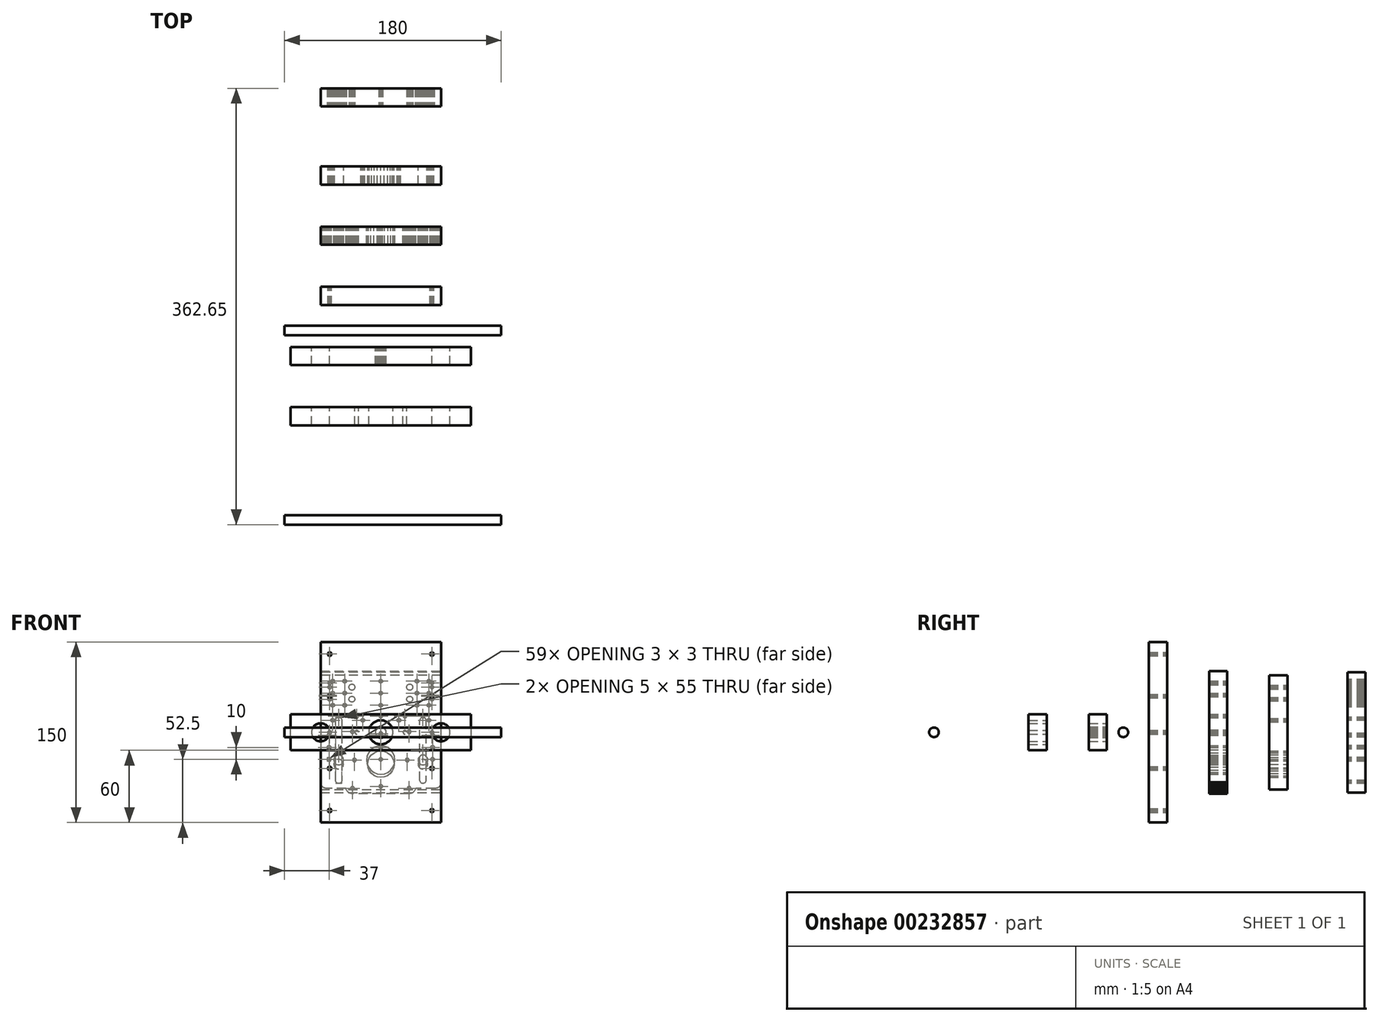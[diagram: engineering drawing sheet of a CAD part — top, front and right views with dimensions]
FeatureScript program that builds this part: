
annotation { "Feature Type Name" : "Feature", "Feature Type Description" : "" }
export const myFeature = defineFeature(function(context is Context, id is Id, definition is map)
    precondition{}
    {
        {
            var Q0;
            Q0=qCreatedBy(makeId("Front.planeOp"),FACE);
            var sketch = newSketch(context, id + "F0", { "sketchPlane" : qUnion([Q0])});
            skLineSegment(sketch, "E0", {"start": v(23.55, -51) * mm, "end": v(-23.55, -51) * mm});
            skLineSegment(sketch, "E1", {"start": v(-23.55, -51) * mm, "end": v(-24.18, -50.96) * mm});
            skLineSegment(sketch, "E2", {"start": v(-24.18, -50.96) * mm, "end": v(-24.8, -50.86) * mm});
            skLineSegment(sketch, "E3", {"start": v(-24.8, -50.86) * mm, "end": v(-25.42, -50.68) * mm});
            skLineSegment(sketch, "E4", {"start": v(-25.42, -50.68) * mm, "end": v(-26, -50.43) * mm});
            skLineSegment(sketch, "E5", {"start": v(-26, -50.43) * mm, "end": v(-26.55, -50.12) * mm});
            skLineSegment(sketch, "E6", {"start": v(-26.55, -50.12) * mm, "end": v(-27.07, -49.75) * mm});
            skLineSegment(sketch, "E7", {"start": v(-27.07, -49.75) * mm, "end": v(-27.54, -49.32) * mm});
            skLineSegment(sketch, "E8", {"start": v(-27.54, -49.32) * mm, "end": v(-27.95, -48.84) * mm});
            skLineSegment(sketch, "E9", {"start": v(-27.95, -48.84) * mm, "end": v(-28.31, -48.32) * mm});
            skLineSegment(sketch, "E10", {"start": v(-28.31, -48.32) * mm, "end": v(-28.6, -47.75) * mm});
            skLineSegment(sketch, "E11", {"start": v(-28.6, -47.75) * mm, "end": v(-28.84, -47.16) * mm});
            skLineSegment(sketch, "E12", {"start": v(-28.84, -47.16) * mm, "end": v(-29, -46.55) * mm});
            skLineSegment(sketch, "E13", {"start": v(-29, -46.55) * mm, "end": v(-45, -46.55) * mm});
            skLineSegment(sketch, "E14", {"start": v(-45, -46.55) * mm, "end": v(-45.65, -46.5) * mm});
            skLineSegment(sketch, "E15", {"start": v(-45.65, -46.5) * mm, "end": v(-46.3, -46.38) * mm});
            skLineSegment(sketch, "E16", {"start": v(-46.3, -46.38) * mm, "end": v(-46.91, -46.17) * mm});
            skLineSegment(sketch, "E17", {"start": v(-46.91, -46.17) * mm, "end": v(-47.5, -45.88) * mm});
            skLineSegment(sketch, "E18", {"start": v(-47.5, -45.88) * mm, "end": v(-48.04, -45.52) * mm});
            skLineSegment(sketch, "E19", {"start": v(-48.04, -45.52) * mm, "end": v(-48.54, -45.09) * mm});
            skLineSegment(sketch, "E20", {"start": v(-48.54, -45.09) * mm, "end": v(-48.97, -44.6) * mm});
            skLineSegment(sketch, "E21", {"start": v(-48.97, -44.6) * mm, "end": v(-49.33, -44.05) * mm});
            skLineSegment(sketch, "E22", {"start": v(-49.33, -44.05) * mm, "end": v(-49.62, -43.46) * mm});
            skLineSegment(sketch, "E23", {"start": v(-49.62, -43.46) * mm, "end": v(-49.83, -42.84) * mm});
            skLineSegment(sketch, "E24", {"start": v(-49.83, -42.84) * mm, "end": v(-49.96, -42.2) * mm});
            skLineSegment(sketch, "E25", {"start": v(-49.96, -42.2) * mm, "end": v(-50, -41.55) * mm});
            skLineSegment(sketch, "E26", {"start": v(-50, -41.55) * mm, "end": v(-50, 51) * mm});
            skLineSegment(sketch, "E27", {"start": v(-50, 51) * mm, "end": v(50, 51) * mm});
            skLineSegment(sketch, "E28", {"start": v(50, 51) * mm, "end": v(50, -41.55) * mm});
            skLineSegment(sketch, "E29", {"start": v(50, -41.55) * mm, "end": v(49.96, -42.2) * mm});
            skLineSegment(sketch, "E30", {"start": v(49.96, -42.2) * mm, "end": v(49.83, -42.84) * mm});
            skLineSegment(sketch, "E31", {"start": v(49.83, -42.84) * mm, "end": v(49.62, -43.46) * mm});
            skLineSegment(sketch, "E32", {"start": v(49.62, -43.46) * mm, "end": v(49.33, -44.05) * mm});
            skLineSegment(sketch, "E33", {"start": v(49.33, -44.05) * mm, "end": v(48.97, -44.6) * mm});
            skLineSegment(sketch, "E34", {"start": v(48.97, -44.6) * mm, "end": v(48.54, -45.09) * mm});
            skLineSegment(sketch, "E35", {"start": v(48.54, -45.09) * mm, "end": v(48.04, -45.52) * mm});
            skLineSegment(sketch, "E36", {"start": v(48.04, -45.52) * mm, "end": v(47.5, -45.88) * mm});
            skLineSegment(sketch, "E37", {"start": v(47.5, -45.88) * mm, "end": v(46.91, -46.17) * mm});
            skLineSegment(sketch, "E38", {"start": v(46.91, -46.17) * mm, "end": v(46.3, -46.38) * mm});
            skLineSegment(sketch, "E39", {"start": v(46.3, -46.38) * mm, "end": v(45.65, -46.5) * mm});
            skLineSegment(sketch, "E40", {"start": v(45.65, -46.5) * mm, "end": v(45, -46.55) * mm});
            skLineSegment(sketch, "E41", {"start": v(45, -46.55) * mm, "end": v(29, -46.55) * mm});
            skLineSegment(sketch, "E42", {"start": v(29, -46.55) * mm, "end": v(28.84, -47.16) * mm});
            skLineSegment(sketch, "E43", {"start": v(28.84, -47.16) * mm, "end": v(28.6, -47.75) * mm});
            skLineSegment(sketch, "E44", {"start": v(28.6, -47.75) * mm, "end": v(28.31, -48.32) * mm});
            skLineSegment(sketch, "E45", {"start": v(28.31, -48.32) * mm, "end": v(27.95, -48.84) * mm});
            skLineSegment(sketch, "E46", {"start": v(27.95, -48.84) * mm, "end": v(27.54, -49.32) * mm});
            skLineSegment(sketch, "E47", {"start": v(27.54, -49.32) * mm, "end": v(27.07, -49.75) * mm});
            skLineSegment(sketch, "E48", {"start": v(27.07, -49.75) * mm, "end": v(26.55, -50.12) * mm});
            skLineSegment(sketch, "E49", {"start": v(26.55, -50.12) * mm, "end": v(26, -50.43) * mm});
            skLineSegment(sketch, "E50", {"start": v(26, -50.43) * mm, "end": v(25.42, -50.68) * mm});
            skLineSegment(sketch, "E51", {"start": v(25.42, -50.68) * mm, "end": v(24.8, -50.86) * mm});
            skLineSegment(sketch, "E52", {"start": v(24.8, -50.86) * mm, "end": v(24.18, -50.96) * mm});
            skLineSegment(sketch, "E53", {"start": v(24.18, -50.96) * mm, "end": v(23.55, -51) * mm});
            skLineSegment(sketch, "E54", {"start": v(3.05, -34.4) * mm, "end": v(5.9, -33.22) * mm});
            skLineSegment(sketch, "E55", {"start": v(5.9, -33.22) * mm, "end": v(8.34, -31.34) * mm});
            skLineSegment(sketch, "E56", {"start": v(8.34, -31.34) * mm, "end": v(10.22, -28.9) * mm});
            skLineSegment(sketch, "E57", {"start": v(10.22, -28.9) * mm, "end": v(11.4, -26.05) * mm});
            skLineSegment(sketch, "E58", {"start": v(11.4, -26.05) * mm, "end": v(11.8, -23) * mm});
            skLineSegment(sketch, "E59", {"start": v(11.8, -23) * mm, "end": v(11.4, -19.95) * mm});
            skLineSegment(sketch, "E60", {"start": v(11.4, -19.95) * mm, "end": v(10.22, -17.1) * mm});
            skLineSegment(sketch, "E61", {"start": v(10.22, -17.1) * mm, "end": v(8.34, -14.66) * mm});
            skLineSegment(sketch, "E62", {"start": v(8.34, -14.66) * mm, "end": v(5.9, -12.78) * mm});
            skLineSegment(sketch, "E63", {"start": v(5.9, -12.78) * mm, "end": v(3.05, -11.6) * mm});
            skLineSegment(sketch, "E64", {"start": v(3.05, -11.6) * mm, "end": v(0, -11.2) * mm});
            skLineSegment(sketch, "E65", {"start": v(0, -11.2) * mm, "end": v(-3.05, -11.6) * mm});
            skLineSegment(sketch, "E66", {"start": v(-3.05, -11.6) * mm, "end": v(-5.9, -12.78) * mm});
            skLineSegment(sketch, "E67", {"start": v(-5.9, -12.78) * mm, "end": v(-8.34, -14.66) * mm});
            skLineSegment(sketch, "E68", {"start": v(-8.34, -14.66) * mm, "end": v(-10.22, -17.1) * mm});
            skLineSegment(sketch, "E69", {"start": v(-10.22, -17.1) * mm, "end": v(-11.4, -19.95) * mm});
            skLineSegment(sketch, "E70", {"start": v(-11.4, -19.95) * mm, "end": v(-11.8, -23) * mm});
            skLineSegment(sketch, "E71", {"start": v(-11.8, -23) * mm, "end": v(-11.4, -26.05) * mm});
            skLineSegment(sketch, "E72", {"start": v(-11.4, -26.05) * mm, "end": v(-10.22, -28.9) * mm});
            skLineSegment(sketch, "E73", {"start": v(-10.22, -28.9) * mm, "end": v(-8.34, -31.34) * mm});
            skLineSegment(sketch, "E74", {"start": v(-8.34, -31.34) * mm, "end": v(-5.9, -33.22) * mm});
            skLineSegment(sketch, "E75", {"start": v(-5.9, -33.22) * mm, "end": v(-3.05, -34.4) * mm});
            skLineSegment(sketch, "E76", {"start": v(-3.05, -34.4) * mm, "end": v(0, -34.8) * mm});
            skLineSegment(sketch, "E77", {"start": v(0, -34.8) * mm, "end": v(3.05, -34.4) * mm});
            skLineSegment(sketch, "E78", {"start": v(-22.25, -47.3) * mm, "end": v(-22.1, -46.94) * mm});
            skLineSegment(sketch, "E79", {"start": v(-22.1, -46.94) * mm, "end": v(-22.05, -46.55) * mm});
            skLineSegment(sketch, "E80", {"start": v(-22.05, -46.55) * mm, "end": v(-22.1, -46.16) * mm});
            skLineSegment(sketch, "E81", {"start": v(-22.1, -46.16) * mm, "end": v(-22.25, -45.8) * mm});
            skLineSegment(sketch, "E82", {"start": v(-22.25, -45.8) * mm, "end": v(-22.49, -45.49) * mm});
            skLineSegment(sketch, "E83", {"start": v(-22.49, -45.49) * mm, "end": v(-22.8, -45.25) * mm});
            skLineSegment(sketch, "E84", {"start": v(-22.8, -45.25) * mm, "end": v(-23.16, -45.1) * mm});
            skLineSegment(sketch, "E85", {"start": v(-23.16, -45.1) * mm, "end": v(-23.55, -45.05) * mm});
            skLineSegment(sketch, "E86", {"start": v(-23.55, -45.05) * mm, "end": v(-23.94, -45.1) * mm});
            skLineSegment(sketch, "E87", {"start": v(-23.94, -45.1) * mm, "end": v(-24.3, -45.25) * mm});
            skLineSegment(sketch, "E88", {"start": v(-24.3, -45.25) * mm, "end": v(-24.61, -45.49) * mm});
            skLineSegment(sketch, "E89", {"start": v(-24.61, -45.49) * mm, "end": v(-24.85, -45.8) * mm});
            skLineSegment(sketch, "E90", {"start": v(-24.85, -45.8) * mm, "end": v(-25, -46.16) * mm});
            skLineSegment(sketch, "E91", {"start": v(-25, -46.16) * mm, "end": v(-25.05, -46.55) * mm});
            skLineSegment(sketch, "E92", {"start": v(-25.05, -46.55) * mm, "end": v(-25, -46.94) * mm});
            skLineSegment(sketch, "E93", {"start": v(-25, -46.94) * mm, "end": v(-24.85, -47.3) * mm});
            skLineSegment(sketch, "E94", {"start": v(-24.85, -47.3) * mm, "end": v(-24.61, -47.61) * mm});
            skLineSegment(sketch, "E95", {"start": v(-24.61, -47.61) * mm, "end": v(-24.3, -47.85) * mm});
            skLineSegment(sketch, "E96", {"start": v(-24.3, -47.85) * mm, "end": v(-23.94, -48) * mm});
            skLineSegment(sketch, "E97", {"start": v(-23.94, -48) * mm, "end": v(-23.55, -48.05) * mm});
            skLineSegment(sketch, "E98", {"start": v(-23.55, -48.05) * mm, "end": v(-23.16, -48) * mm});
            skLineSegment(sketch, "E99", {"start": v(-23.16, -48) * mm, "end": v(-22.8, -47.85) * mm});
            skLineSegment(sketch, "E100", {"start": v(-22.8, -47.85) * mm, "end": v(-22.49, -47.61) * mm});
            skLineSegment(sketch, "E101", {"start": v(-22.49, -47.61) * mm, "end": v(-22.25, -47.3) * mm});
            skLineSegment(sketch, "E102", {"start": v(22.8, -45.25) * mm, "end": v(22.49, -45.49) * mm});
            skLineSegment(sketch, "E103", {"start": v(22.49, -45.49) * mm, "end": v(22.25, -45.8) * mm});
            skLineSegment(sketch, "E104", {"start": v(22.25, -45.8) * mm, "end": v(22.1, -46.16) * mm});
            skLineSegment(sketch, "E105", {"start": v(22.1, -46.16) * mm, "end": v(22.05, -46.55) * mm});
            skLineSegment(sketch, "E106", {"start": v(22.05, -46.55) * mm, "end": v(22.1, -46.94) * mm});
            skLineSegment(sketch, "E107", {"start": v(22.1, -46.94) * mm, "end": v(22.25, -47.3) * mm});
            skLineSegment(sketch, "E108", {"start": v(22.25, -47.3) * mm, "end": v(22.49, -47.61) * mm});
            skLineSegment(sketch, "E109", {"start": v(22.49, -47.61) * mm, "end": v(22.8, -47.85) * mm});
            skLineSegment(sketch, "E110", {"start": v(22.8, -47.85) * mm, "end": v(23.16, -48) * mm});
            skLineSegment(sketch, "E111", {"start": v(23.16, -48) * mm, "end": v(23.55, -48.05) * mm});
            skLineSegment(sketch, "E112", {"start": v(23.55, -48.05) * mm, "end": v(23.94, -48) * mm});
            skLineSegment(sketch, "E113", {"start": v(23.94, -48) * mm, "end": v(24.3, -47.85) * mm});
            skLineSegment(sketch, "E114", {"start": v(24.3, -47.85) * mm, "end": v(24.61, -47.61) * mm});
            skLineSegment(sketch, "E115", {"start": v(24.61, -47.61) * mm, "end": v(24.85, -47.3) * mm});
            skLineSegment(sketch, "E116", {"start": v(24.85, -47.3) * mm, "end": v(25, -46.94) * mm});
            skLineSegment(sketch, "E117", {"start": v(25, -46.94) * mm, "end": v(25.05, -46.55) * mm});
            skLineSegment(sketch, "E118", {"start": v(25.05, -46.55) * mm, "end": v(25, -46.16) * mm});
            skLineSegment(sketch, "E119", {"start": v(25, -46.16) * mm, "end": v(24.85, -45.8) * mm});
            skLineSegment(sketch, "E120", {"start": v(24.85, -45.8) * mm, "end": v(24.61, -45.49) * mm});
            skLineSegment(sketch, "E121", {"start": v(24.61, -45.49) * mm, "end": v(24.3, -45.25) * mm});
            skLineSegment(sketch, "E122", {"start": v(24.3, -45.25) * mm, "end": v(23.94, -45.1) * mm});
            skLineSegment(sketch, "E123", {"start": v(23.94, -45.1) * mm, "end": v(23.55, -45.05) * mm});
            skLineSegment(sketch, "E124", {"start": v(23.55, -45.05) * mm, "end": v(23.16, -45.1) * mm});
            skLineSegment(sketch, "E125", {"start": v(23.16, -45.1) * mm, "end": v(22.8, -45.25) * mm});
            skLineSegment(sketch, "E126", {"start": v(24.85, -0.2) * mm, "end": v(25, 0.16) * mm});
            skLineSegment(sketch, "E127", {"start": v(25, 0.16) * mm, "end": v(25.05, 0.55) * mm});
            skLineSegment(sketch, "E128", {"start": v(25.05, 0.55) * mm, "end": v(25, 0.94) * mm});
            skLineSegment(sketch, "E129", {"start": v(25, 0.94) * mm, "end": v(24.85, 1.3) * mm});
            skLineSegment(sketch, "E130", {"start": v(24.85, 1.3) * mm, "end": v(24.61, 1.61) * mm});
            skLineSegment(sketch, "E131", {"start": v(24.61, 1.61) * mm, "end": v(24.3, 1.85) * mm});
            skLineSegment(sketch, "E132", {"start": v(24.3, 1.85) * mm, "end": v(23.94, 2) * mm});
            skLineSegment(sketch, "E133", {"start": v(23.94, 2) * mm, "end": v(23.55, 2.05) * mm});
            skLineSegment(sketch, "E134", {"start": v(23.55, 2.05) * mm, "end": v(23.16, 2) * mm});
            skLineSegment(sketch, "E135", {"start": v(23.16, 2) * mm, "end": v(22.8, 1.85) * mm});
            skLineSegment(sketch, "E136", {"start": v(22.8, 1.85) * mm, "end": v(22.49, 1.61) * mm});
            skLineSegment(sketch, "E137", {"start": v(22.49, 1.61) * mm, "end": v(22.25, 1.3) * mm});
            skLineSegment(sketch, "E138", {"start": v(22.25, 1.3) * mm, "end": v(22.1, 0.94) * mm});
            skLineSegment(sketch, "E139", {"start": v(22.1, 0.94) * mm, "end": v(22.05, 0.55) * mm});
            skLineSegment(sketch, "E140", {"start": v(22.05, 0.55) * mm, "end": v(22.1, 0.16) * mm});
            skLineSegment(sketch, "E141", {"start": v(22.1, 0.16) * mm, "end": v(22.25, -0.2) * mm});
            skLineSegment(sketch, "E142", {"start": v(22.25, -0.2) * mm, "end": v(22.49, -0.51) * mm});
            skLineSegment(sketch, "E143", {"start": v(22.49, -0.51) * mm, "end": v(22.8, -0.75) * mm});
            skLineSegment(sketch, "E144", {"start": v(22.8, -0.75) * mm, "end": v(23.16, -0.9) * mm});
            skLineSegment(sketch, "E145", {"start": v(23.16, -0.9) * mm, "end": v(23.55, -0.95) * mm});
            skLineSegment(sketch, "E146", {"start": v(23.55, -0.95) * mm, "end": v(23.94, -0.9) * mm});
            skLineSegment(sketch, "E147", {"start": v(23.94, -0.9) * mm, "end": v(24.3, -0.75) * mm});
            skLineSegment(sketch, "E148", {"start": v(24.3, -0.75) * mm, "end": v(24.61, -0.51) * mm});
            skLineSegment(sketch, "E149", {"start": v(24.61, -0.51) * mm, "end": v(24.85, -0.2) * mm});
            skLineSegment(sketch, "E150", {"start": v(-25, 0.16) * mm, "end": v(-24.85, -0.2) * mm});
            skLineSegment(sketch, "E151", {"start": v(-24.85, -0.2) * mm, "end": v(-24.61, -0.51) * mm});
            skLineSegment(sketch, "E152", {"start": v(-24.61, -0.51) * mm, "end": v(-24.3, -0.75) * mm});
            skLineSegment(sketch, "E153", {"start": v(-24.3, -0.75) * mm, "end": v(-23.94, -0.9) * mm});
            skLineSegment(sketch, "E154", {"start": v(-23.94, -0.9) * mm, "end": v(-23.55, -0.95) * mm});
            skLineSegment(sketch, "E155", {"start": v(-23.55, -0.95) * mm, "end": v(-23.16, -0.9) * mm});
            skLineSegment(sketch, "E156", {"start": v(-23.16, -0.9) * mm, "end": v(-22.8, -0.75) * mm});
            skLineSegment(sketch, "E157", {"start": v(-22.8, -0.75) * mm, "end": v(-22.49, -0.51) * mm});
            skLineSegment(sketch, "E158", {"start": v(-22.49, -0.51) * mm, "end": v(-22.25, -0.2) * mm});
            skLineSegment(sketch, "E159", {"start": v(-22.25, -0.2) * mm, "end": v(-22.1, 0.16) * mm});
            skLineSegment(sketch, "E160", {"start": v(-22.1, 0.16) * mm, "end": v(-22.05, 0.55) * mm});
            skLineSegment(sketch, "E161", {"start": v(-22.05, 0.55) * mm, "end": v(-22.1, 0.94) * mm});
            skLineSegment(sketch, "E162", {"start": v(-22.1, 0.94) * mm, "end": v(-22.25, 1.3) * mm});
            skLineSegment(sketch, "E163", {"start": v(-22.25, 1.3) * mm, "end": v(-22.49, 1.61) * mm});
            skLineSegment(sketch, "E164", {"start": v(-22.49, 1.61) * mm, "end": v(-22.8, 1.85) * mm});
            skLineSegment(sketch, "E165", {"start": v(-22.8, 1.85) * mm, "end": v(-23.16, 2) * mm});
            skLineSegment(sketch, "E166", {"start": v(-23.16, 2) * mm, "end": v(-23.55, 2.05) * mm});
            skLineSegment(sketch, "E167", {"start": v(-23.55, 2.05) * mm, "end": v(-23.94, 2) * mm});
            skLineSegment(sketch, "E168", {"start": v(-23.94, 2) * mm, "end": v(-24.3, 1.85) * mm});
            skLineSegment(sketch, "E169", {"start": v(-24.3, 1.85) * mm, "end": v(-24.61, 1.61) * mm});
            skLineSegment(sketch, "E170", {"start": v(-24.61, 1.61) * mm, "end": v(-24.85, 1.3) * mm});
            skLineSegment(sketch, "E171", {"start": v(-24.85, 1.3) * mm, "end": v(-25, 0.94) * mm});
            skLineSegment(sketch, "E172", {"start": v(-25, 0.94) * mm, "end": v(-25.05, 0.55) * mm});
            skLineSegment(sketch, "E173", {"start": v(-25.05, 0.55) * mm, "end": v(-25, 0.16) * mm});
            skLineSegment(sketch, "E174", {"start": v(-1.45, -44.53) * mm, "end": v(-1.5, -44.92) * mm});
            skLineSegment(sketch, "E175", {"start": v(-1.5, -44.92) * mm, "end": v(-1.45, -45.3) * mm});
            skLineSegment(sketch, "E176", {"start": v(-1.45, -45.3) * mm, "end": v(-1.3, -45.67) * mm});
            skLineSegment(sketch, "E177", {"start": v(-1.3, -45.67) * mm, "end": v(-1.06, -45.98) * mm});
            skLineSegment(sketch, "E178", {"start": v(-1.06, -45.98) * mm, "end": v(-0.75, -46.22) * mm});
            skLineSegment(sketch, "E179", {"start": v(-0.75, -46.22) * mm, "end": v(-0.39, -46.37) * mm});
            skLineSegment(sketch, "E180", {"start": v(-0.39, -46.37) * mm, "end": v(0, -46.42) * mm});
            skLineSegment(sketch, "E181", {"start": v(0, -46.42) * mm, "end": v(0.39, -46.37) * mm});
            skLineSegment(sketch, "E182", {"start": v(0.39, -46.37) * mm, "end": v(0.75, -46.22) * mm});
            skLineSegment(sketch, "E183", {"start": v(0.75, -46.22) * mm, "end": v(1.06, -45.98) * mm});
            skLineSegment(sketch, "E184", {"start": v(1.06, -45.98) * mm, "end": v(1.3, -45.67) * mm});
            skLineSegment(sketch, "E185", {"start": v(1.3, -45.67) * mm, "end": v(1.45, -45.3) * mm});
            skLineSegment(sketch, "E186", {"start": v(1.45, -45.3) * mm, "end": v(1.5, -44.92) * mm});
            skLineSegment(sketch, "E187", {"start": v(1.5, -44.92) * mm, "end": v(1.45, -44.53) * mm});
            skLineSegment(sketch, "E188", {"start": v(1.45, -44.53) * mm, "end": v(1.3, -44.17) * mm});
            skLineSegment(sketch, "E189", {"start": v(1.3, -44.17) * mm, "end": v(1.06, -43.86) * mm});
            skLineSegment(sketch, "E190", {"start": v(1.06, -43.86) * mm, "end": v(0.75, -43.62) * mm});
            skLineSegment(sketch, "E191", {"start": v(0.75, -43.62) * mm, "end": v(0.39, -43.47) * mm});
            skLineSegment(sketch, "E192", {"start": v(0.39, -43.47) * mm, "end": v(0, -43.42) * mm});
            skLineSegment(sketch, "E193", {"start": v(0, -43.42) * mm, "end": v(-0.39, -43.47) * mm});
            skLineSegment(sketch, "E194", {"start": v(-0.39, -43.47) * mm, "end": v(-0.75, -43.62) * mm});
            skLineSegment(sketch, "E195", {"start": v(-0.75, -43.62) * mm, "end": v(-1.06, -43.86) * mm});
            skLineSegment(sketch, "E196", {"start": v(-1.06, -43.86) * mm, "end": v(-1.3, -44.17) * mm});
            skLineSegment(sketch, "E197", {"start": v(-1.3, -44.17) * mm, "end": v(-1.45, -44.53) * mm});
            skLineSegment(sketch, "E198", {"start": v(-21.53, -24.45) * mm, "end": v(-21.17, -24.3) * mm});
            skLineSegment(sketch, "E199", {"start": v(-21.17, -24.3) * mm, "end": v(-20.86, -24.06) * mm});
            skLineSegment(sketch, "E200", {"start": v(-20.86, -24.06) * mm, "end": v(-20.62, -23.75) * mm});
            skLineSegment(sketch, "E201", {"start": v(-20.62, -23.75) * mm, "end": v(-20.47, -23.39) * mm});
            skLineSegment(sketch, "E202", {"start": v(-20.47, -23.39) * mm, "end": v(-20.42, -23) * mm});
            skLineSegment(sketch, "E203", {"start": v(-20.42, -23) * mm, "end": v(-20.47, -22.61) * mm});
            skLineSegment(sketch, "E204", {"start": v(-20.47, -22.61) * mm, "end": v(-20.62, -22.25) * mm});
            skLineSegment(sketch, "E205", {"start": v(-20.62, -22.25) * mm, "end": v(-20.86, -21.94) * mm});
            skLineSegment(sketch, "E206", {"start": v(-20.86, -21.94) * mm, "end": v(-21.17, -21.7) * mm});
            skLineSegment(sketch, "E207", {"start": v(-21.17, -21.7) * mm, "end": v(-21.53, -21.55) * mm});
            skLineSegment(sketch, "E208", {"start": v(-21.53, -21.55) * mm, "end": v(-21.92, -21.5) * mm});
            skLineSegment(sketch, "E209", {"start": v(-21.92, -21.5) * mm, "end": v(-22.3, -21.55) * mm});
            skLineSegment(sketch, "E210", {"start": v(-22.3, -21.55) * mm, "end": v(-22.67, -21.7) * mm});
            skLineSegment(sketch, "E211", {"start": v(-22.67, -21.7) * mm, "end": v(-22.98, -21.94) * mm});
            skLineSegment(sketch, "E212", {"start": v(-22.98, -21.94) * mm, "end": v(-23.22, -22.25) * mm});
            skLineSegment(sketch, "E213", {"start": v(-23.22, -22.25) * mm, "end": v(-23.37, -22.61) * mm});
            skLineSegment(sketch, "E214", {"start": v(-23.37, -22.61) * mm, "end": v(-23.42, -23) * mm});
            skLineSegment(sketch, "E215", {"start": v(-23.42, -23) * mm, "end": v(-23.37, -23.39) * mm});
            skLineSegment(sketch, "E216", {"start": v(-23.37, -23.39) * mm, "end": v(-23.22, -23.75) * mm});
            skLineSegment(sketch, "E217", {"start": v(-23.22, -23.75) * mm, "end": v(-22.98, -24.06) * mm});
            skLineSegment(sketch, "E218", {"start": v(-22.98, -24.06) * mm, "end": v(-22.67, -24.3) * mm});
            skLineSegment(sketch, "E219", {"start": v(-22.67, -24.3) * mm, "end": v(-22.3, -24.45) * mm});
            skLineSegment(sketch, "E220", {"start": v(-22.3, -24.45) * mm, "end": v(-21.92, -24.5) * mm});
            skLineSegment(sketch, "E221", {"start": v(-21.92, -24.5) * mm, "end": v(-21.53, -24.45) * mm});
            skLineSegment(sketch, "E222", {"start": v(-1.3, -0.33) * mm, "end": v(-1.45, -0.7) * mm});
            skLineSegment(sketch, "E223", {"start": v(-1.45, -0.7) * mm, "end": v(-1.5, -1.08) * mm});
            skLineSegment(sketch, "E224", {"start": v(-1.5, -1.08) * mm, "end": v(-1.45, -1.47) * mm});
            skLineSegment(sketch, "E225", {"start": v(-1.45, -1.47) * mm, "end": v(-1.3, -1.83) * mm});
            skLineSegment(sketch, "E226", {"start": v(-1.3, -1.83) * mm, "end": v(-1.06, -2.14) * mm});
            skLineSegment(sketch, "E227", {"start": v(-1.06, -2.14) * mm, "end": v(-0.75, -2.38) * mm});
            skLineSegment(sketch, "E228", {"start": v(-0.75, -2.38) * mm, "end": v(-0.39, -2.53) * mm});
            skLineSegment(sketch, "E229", {"start": v(-0.39, -2.53) * mm, "end": v(0, -2.58) * mm});
            skLineSegment(sketch, "E230", {"start": v(0, -2.58) * mm, "end": v(0.39, -2.53) * mm});
            skLineSegment(sketch, "E231", {"start": v(0.39, -2.53) * mm, "end": v(0.75, -2.38) * mm});
            skLineSegment(sketch, "E232", {"start": v(0.75, -2.38) * mm, "end": v(1.06, -2.14) * mm});
            skLineSegment(sketch, "E233", {"start": v(1.06, -2.14) * mm, "end": v(1.3, -1.83) * mm});
            skLineSegment(sketch, "E234", {"start": v(1.3, -1.83) * mm, "end": v(1.45, -1.47) * mm});
            skLineSegment(sketch, "E235", {"start": v(1.45, -1.47) * mm, "end": v(1.5, -1.08) * mm});
            skLineSegment(sketch, "E236", {"start": v(1.5, -1.08) * mm, "end": v(1.45, -0.7) * mm});
            skLineSegment(sketch, "E237", {"start": v(1.45, -0.7) * mm, "end": v(1.3, -0.33) * mm});
            skLineSegment(sketch, "E238", {"start": v(1.3, -0.33) * mm, "end": v(1.06, -0.02) * mm});
            skLineSegment(sketch, "E239", {"start": v(1.06, -0.02) * mm, "end": v(0.75, 0.22) * mm});
            skLineSegment(sketch, "E240", {"start": v(0.75, 0.22) * mm, "end": v(0.39, 0.37) * mm});
            skLineSegment(sketch, "E241", {"start": v(0.39, 0.37) * mm, "end": v(0, 0.42) * mm});
            skLineSegment(sketch, "E242", {"start": v(0, 0.42) * mm, "end": v(-0.39, 0.37) * mm});
            skLineSegment(sketch, "E243", {"start": v(-0.39, 0.37) * mm, "end": v(-0.75, 0.22) * mm});
            skLineSegment(sketch, "E244", {"start": v(-0.75, 0.22) * mm, "end": v(-1.06, -0.02) * mm});
            skLineSegment(sketch, "E245", {"start": v(-1.06, -0.02) * mm, "end": v(-1.3, -0.33) * mm});
            skLineSegment(sketch, "E246", {"start": v(21.17, -21.7) * mm, "end": v(20.86, -21.94) * mm});
            skLineSegment(sketch, "E247", {"start": v(20.86, -21.94) * mm, "end": v(20.62, -22.25) * mm});
            skLineSegment(sketch, "E248", {"start": v(20.62, -22.25) * mm, "end": v(20.47, -22.61) * mm});
            skLineSegment(sketch, "E249", {"start": v(20.47, -22.61) * mm, "end": v(20.42, -23) * mm});
            skLineSegment(sketch, "E250", {"start": v(20.42, -23) * mm, "end": v(20.47, -23.39) * mm});
            skLineSegment(sketch, "E251", {"start": v(20.47, -23.39) * mm, "end": v(20.62, -23.75) * mm});
            skLineSegment(sketch, "E252", {"start": v(20.62, -23.75) * mm, "end": v(20.86, -24.06) * mm});
            skLineSegment(sketch, "E253", {"start": v(20.86, -24.06) * mm, "end": v(21.17, -24.3) * mm});
            skLineSegment(sketch, "E254", {"start": v(21.17, -24.3) * mm, "end": v(21.53, -24.45) * mm});
            skLineSegment(sketch, "E255", {"start": v(21.53, -24.45) * mm, "end": v(21.92, -24.5) * mm});
            skLineSegment(sketch, "E256", {"start": v(21.92, -24.5) * mm, "end": v(22.3, -24.45) * mm});
            skLineSegment(sketch, "E257", {"start": v(22.3, -24.45) * mm, "end": v(22.67, -24.3) * mm});
            skLineSegment(sketch, "E258", {"start": v(22.67, -24.3) * mm, "end": v(22.98, -24.06) * mm});
            skLineSegment(sketch, "E259", {"start": v(22.98, -24.06) * mm, "end": v(23.22, -23.75) * mm});
            skLineSegment(sketch, "E260", {"start": v(23.22, -23.75) * mm, "end": v(23.37, -23.39) * mm});
            skLineSegment(sketch, "E261", {"start": v(23.37, -23.39) * mm, "end": v(23.42, -23) * mm});
            skLineSegment(sketch, "E262", {"start": v(23.42, -23) * mm, "end": v(23.37, -22.61) * mm});
            skLineSegment(sketch, "E263", {"start": v(23.37, -22.61) * mm, "end": v(23.22, -22.25) * mm});
            skLineSegment(sketch, "E264", {"start": v(23.22, -22.25) * mm, "end": v(22.98, -21.94) * mm});
            skLineSegment(sketch, "E265", {"start": v(22.98, -21.94) * mm, "end": v(22.67, -21.7) * mm});
            skLineSegment(sketch, "E266", {"start": v(22.67, -21.7) * mm, "end": v(22.3, -21.55) * mm});
            skLineSegment(sketch, "E267", {"start": v(22.3, -21.55) * mm, "end": v(21.92, -21.5) * mm});
            skLineSegment(sketch, "E268", {"start": v(21.92, -21.5) * mm, "end": v(21.53, -21.55) * mm});
            skLineSegment(sketch, "E269", {"start": v(21.53, -21.55) * mm, "end": v(21.17, -21.7) * mm});
            skLineSegment(sketch, "E270", {"start": v(35.75, 12.2) * mm, "end": v(36.06, 12.44) * mm});
            skLineSegment(sketch, "E271", {"start": v(36.06, 12.44) * mm, "end": v(36.3, 12.75) * mm});
            skLineSegment(sketch, "E272", {"start": v(36.3, 12.75) * mm, "end": v(36.45, 13.11) * mm});
            skLineSegment(sketch, "E273", {"start": v(36.45, 13.11) * mm, "end": v(36.5, 13.5) * mm});
            skLineSegment(sketch, "E274", {"start": v(36.5, 13.5) * mm, "end": v(36.45, 13.89) * mm});
            skLineSegment(sketch, "E275", {"start": v(36.45, 13.89) * mm, "end": v(36.3, 14.25) * mm});
            skLineSegment(sketch, "E276", {"start": v(36.3, 14.25) * mm, "end": v(36.06, 14.56) * mm});
            skLineSegment(sketch, "E277", {"start": v(36.06, 14.56) * mm, "end": v(35.75, 14.8) * mm});
            skLineSegment(sketch, "E278", {"start": v(35.75, 14.8) * mm, "end": v(35.39, 14.95) * mm});
            skLineSegment(sketch, "E279", {"start": v(35.39, 14.95) * mm, "end": v(35, 15) * mm});
            skLineSegment(sketch, "E280", {"start": v(35, 15) * mm, "end": v(34.61, 14.95) * mm});
            skLineSegment(sketch, "E281", {"start": v(34.61, 14.95) * mm, "end": v(34.25, 14.8) * mm});
            skLineSegment(sketch, "E282", {"start": v(34.25, 14.8) * mm, "end": v(33.94, 14.56) * mm});
            skLineSegment(sketch, "E283", {"start": v(33.94, 14.56) * mm, "end": v(33.7, 14.25) * mm});
            skLineSegment(sketch, "E284", {"start": v(33.7, 14.25) * mm, "end": v(33.55, 13.89) * mm});
            skLineSegment(sketch, "E285", {"start": v(33.55, 13.89) * mm, "end": v(33.5, 13.5) * mm});
            skLineSegment(sketch, "E286", {"start": v(33.5, 13.5) * mm, "end": v(33.55, 13.11) * mm});
            skLineSegment(sketch, "E287", {"start": v(33.55, 13.11) * mm, "end": v(33.7, 12.75) * mm});
            skLineSegment(sketch, "E288", {"start": v(33.7, 12.75) * mm, "end": v(33.94, 12.44) * mm});
            skLineSegment(sketch, "E289", {"start": v(33.94, 12.44) * mm, "end": v(34.25, 12.2) * mm});
            skLineSegment(sketch, "E290", {"start": v(34.25, 12.2) * mm, "end": v(34.61, 12.05) * mm});
            skLineSegment(sketch, "E291", {"start": v(34.61, 12.05) * mm, "end": v(35, 12) * mm});
            skLineSegment(sketch, "E292", {"start": v(35, 12) * mm, "end": v(35.39, 12.05) * mm});
            skLineSegment(sketch, "E293", {"start": v(35.39, 12.05) * mm, "end": v(35.75, 12.2) * mm});
            skLineSegment(sketch, "E294", {"start": v(18.7, 14.25) * mm, "end": v(18.55, 13.89) * mm});
            skLineSegment(sketch, "E295", {"start": v(18.55, 13.89) * mm, "end": v(18.5, 13.5) * mm});
            skLineSegment(sketch, "E296", {"start": v(18.5, 13.5) * mm, "end": v(18.55, 13.11) * mm});
            skLineSegment(sketch, "E297", {"start": v(18.55, 13.11) * mm, "end": v(18.7, 12.75) * mm});
            skLineSegment(sketch, "E298", {"start": v(18.7, 12.75) * mm, "end": v(18.94, 12.44) * mm});
            skLineSegment(sketch, "E299", {"start": v(18.94, 12.44) * mm, "end": v(19.25, 12.2) * mm});
            skLineSegment(sketch, "E300", {"start": v(19.25, 12.2) * mm, "end": v(19.61, 12.05) * mm});
            skLineSegment(sketch, "E301", {"start": v(19.61, 12.05) * mm, "end": v(20, 12) * mm});
            skLineSegment(sketch, "E302", {"start": v(20, 12) * mm, "end": v(20.39, 12.05) * mm});
            skLineSegment(sketch, "E303", {"start": v(20.39, 12.05) * mm, "end": v(20.75, 12.2) * mm});
            skLineSegment(sketch, "E304", {"start": v(20.75, 12.2) * mm, "end": v(21.06, 12.44) * mm});
            skLineSegment(sketch, "E305", {"start": v(21.06, 12.44) * mm, "end": v(21.3, 12.75) * mm});
            skLineSegment(sketch, "E306", {"start": v(21.3, 12.75) * mm, "end": v(21.45, 13.11) * mm});
            skLineSegment(sketch, "E307", {"start": v(21.45, 13.11) * mm, "end": v(21.5, 13.5) * mm});
            skLineSegment(sketch, "E308", {"start": v(21.5, 13.5) * mm, "end": v(21.45, 13.89) * mm});
            skLineSegment(sketch, "E309", {"start": v(21.45, 13.89) * mm, "end": v(21.3, 14.25) * mm});
            skLineSegment(sketch, "E310", {"start": v(21.3, 14.25) * mm, "end": v(21.06, 14.56) * mm});
            skLineSegment(sketch, "E311", {"start": v(21.06, 14.56) * mm, "end": v(20.75, 14.8) * mm});
            skLineSegment(sketch, "E312", {"start": v(20.75, 14.8) * mm, "end": v(20.39, 14.95) * mm});
            skLineSegment(sketch, "E313", {"start": v(20.39, 14.95) * mm, "end": v(20, 15) * mm});
            skLineSegment(sketch, "E314", {"start": v(20, 15) * mm, "end": v(19.61, 14.95) * mm});
            skLineSegment(sketch, "E315", {"start": v(19.61, 14.95) * mm, "end": v(19.25, 14.8) * mm});
            skLineSegment(sketch, "E316", {"start": v(19.25, 14.8) * mm, "end": v(18.94, 14.56) * mm});
            skLineSegment(sketch, "E317", {"start": v(18.94, 14.56) * mm, "end": v(18.7, 14.25) * mm});
            skLineSegment(sketch, "E318", {"start": v(1.5, 13.5) * mm, "end": v(1.45, 13.89) * mm});
            skLineSegment(sketch, "E319", {"start": v(1.45, 13.89) * mm, "end": v(1.3, 14.25) * mm});
            skLineSegment(sketch, "E320", {"start": v(1.3, 14.25) * mm, "end": v(1.06, 14.56) * mm});
            skLineSegment(sketch, "E321", {"start": v(1.06, 14.56) * mm, "end": v(0.75, 14.8) * mm});
            skLineSegment(sketch, "E322", {"start": v(0.75, 14.8) * mm, "end": v(0.39, 14.95) * mm});
            skLineSegment(sketch, "E323", {"start": v(0.39, 14.95) * mm, "end": v(0, 15) * mm});
            skLineSegment(sketch, "E324", {"start": v(0, 15) * mm, "end": v(-0.39, 14.95) * mm});
            skLineSegment(sketch, "E325", {"start": v(-0.39, 14.95) * mm, "end": v(-0.75, 14.8) * mm});
            skLineSegment(sketch, "E326", {"start": v(-0.75, 14.8) * mm, "end": v(-1.06, 14.56) * mm});
            skLineSegment(sketch, "E327", {"start": v(-1.06, 14.56) * mm, "end": v(-1.3, 14.25) * mm});
            skLineSegment(sketch, "E328", {"start": v(-1.3, 14.25) * mm, "end": v(-1.45, 13.89) * mm});
            skLineSegment(sketch, "E329", {"start": v(-1.45, 13.89) * mm, "end": v(-1.5, 13.5) * mm});
            skLineSegment(sketch, "E330", {"start": v(-1.5, 13.5) * mm, "end": v(-1.45, 13.11) * mm});
            skLineSegment(sketch, "E331", {"start": v(-1.45, 13.11) * mm, "end": v(-1.3, 12.75) * mm});
            skLineSegment(sketch, "E332", {"start": v(-1.3, 12.75) * mm, "end": v(-1.06, 12.44) * mm});
            skLineSegment(sketch, "E333", {"start": v(-1.06, 12.44) * mm, "end": v(-0.75, 12.2) * mm});
            skLineSegment(sketch, "E334", {"start": v(-0.75, 12.2) * mm, "end": v(-0.39, 12.05) * mm});
            skLineSegment(sketch, "E335", {"start": v(-0.39, 12.05) * mm, "end": v(0, 12) * mm});
            skLineSegment(sketch, "E336", {"start": v(0, 12) * mm, "end": v(0.39, 12.05) * mm});
            skLineSegment(sketch, "E337", {"start": v(0.39, 12.05) * mm, "end": v(0.75, 12.2) * mm});
            skLineSegment(sketch, "E338", {"start": v(0.75, 12.2) * mm, "end": v(1.06, 12.44) * mm});
            skLineSegment(sketch, "E339", {"start": v(1.06, 12.44) * mm, "end": v(1.3, 12.75) * mm});
            skLineSegment(sketch, "E340", {"start": v(1.3, 12.75) * mm, "end": v(1.45, 13.11) * mm});
            skLineSegment(sketch, "E341", {"start": v(1.45, 13.11) * mm, "end": v(1.5, 13.5) * mm});
            skLineSegment(sketch, "E342", {"start": v(-19.25, 14.8) * mm, "end": v(-19.61, 14.95) * mm});
            skLineSegment(sketch, "E343", {"start": v(-19.61, 14.95) * mm, "end": v(-20, 15) * mm});
            skLineSegment(sketch, "E344", {"start": v(-20, 15) * mm, "end": v(-20.39, 14.95) * mm});
            skLineSegment(sketch, "E345", {"start": v(-20.39, 14.95) * mm, "end": v(-20.75, 14.8) * mm});
            skLineSegment(sketch, "E346", {"start": v(-20.75, 14.8) * mm, "end": v(-21.06, 14.56) * mm});
            skLineSegment(sketch, "E347", {"start": v(-21.06, 14.56) * mm, "end": v(-21.3, 14.25) * mm});
            skLineSegment(sketch, "E348", {"start": v(-21.3, 14.25) * mm, "end": v(-21.45, 13.89) * mm});
            skLineSegment(sketch, "E349", {"start": v(-21.45, 13.89) * mm, "end": v(-21.5, 13.5) * mm});
            skLineSegment(sketch, "E350", {"start": v(-21.5, 13.5) * mm, "end": v(-21.45, 13.11) * mm});
            skLineSegment(sketch, "E351", {"start": v(-21.45, 13.11) * mm, "end": v(-21.3, 12.75) * mm});
            skLineSegment(sketch, "E352", {"start": v(-21.3, 12.75) * mm, "end": v(-21.06, 12.44) * mm});
            skLineSegment(sketch, "E353", {"start": v(-21.06, 12.44) * mm, "end": v(-20.75, 12.2) * mm});
            skLineSegment(sketch, "E354", {"start": v(-20.75, 12.2) * mm, "end": v(-20.39, 12.05) * mm});
            skLineSegment(sketch, "E355", {"start": v(-20.39, 12.05) * mm, "end": v(-20, 12) * mm});
            skLineSegment(sketch, "E356", {"start": v(-20, 12) * mm, "end": v(-19.61, 12.05) * mm});
            skLineSegment(sketch, "E357", {"start": v(-19.61, 12.05) * mm, "end": v(-19.25, 12.2) * mm});
            skLineSegment(sketch, "E358", {"start": v(-19.25, 12.2) * mm, "end": v(-18.94, 12.44) * mm});
            skLineSegment(sketch, "E359", {"start": v(-18.94, 12.44) * mm, "end": v(-18.7, 12.75) * mm});
            skLineSegment(sketch, "E360", {"start": v(-18.7, 12.75) * mm, "end": v(-18.55, 13.11) * mm});
            skLineSegment(sketch, "E361", {"start": v(-18.55, 13.11) * mm, "end": v(-18.5, 13.5) * mm});
            skLineSegment(sketch, "E362", {"start": v(-18.5, 13.5) * mm, "end": v(-18.55, 13.89) * mm});
            skLineSegment(sketch, "E363", {"start": v(-18.55, 13.89) * mm, "end": v(-18.7, 14.25) * mm});
            skLineSegment(sketch, "E364", {"start": v(-18.7, 14.25) * mm, "end": v(-18.94, 14.56) * mm});
            skLineSegment(sketch, "E365", {"start": v(-18.94, 14.56) * mm, "end": v(-19.25, 14.8) * mm});
            skLineSegment(sketch, "E366", {"start": v(-35.39, 14.95) * mm, "end": v(-35.75, 14.8) * mm});
            skLineSegment(sketch, "E367", {"start": v(-35.75, 14.8) * mm, "end": v(-36.06, 14.56) * mm});
            skLineSegment(sketch, "E368", {"start": v(-36.06, 14.56) * mm, "end": v(-36.3, 14.25) * mm});
            skLineSegment(sketch, "E369", {"start": v(-36.3, 14.25) * mm, "end": v(-36.45, 13.89) * mm});
            skLineSegment(sketch, "E370", {"start": v(-36.45, 13.89) * mm, "end": v(-36.5, 13.5) * mm});
            skLineSegment(sketch, "E371", {"start": v(-36.5, 13.5) * mm, "end": v(-36.45, 13.11) * mm});
            skLineSegment(sketch, "E372", {"start": v(-36.45, 13.11) * mm, "end": v(-36.3, 12.75) * mm});
            skLineSegment(sketch, "E373", {"start": v(-36.3, 12.75) * mm, "end": v(-36.06, 12.44) * mm});
            skLineSegment(sketch, "E374", {"start": v(-36.06, 12.44) * mm, "end": v(-35.75, 12.2) * mm});
            skLineSegment(sketch, "E375", {"start": v(-35.75, 12.2) * mm, "end": v(-35.39, 12.05) * mm});
            skLineSegment(sketch, "E376", {"start": v(-35.39, 12.05) * mm, "end": v(-35, 12) * mm});
            skLineSegment(sketch, "E377", {"start": v(-35, 12) * mm, "end": v(-34.61, 12.05) * mm});
            skLineSegment(sketch, "E378", {"start": v(-34.61, 12.05) * mm, "end": v(-34.25, 12.2) * mm});
            skLineSegment(sketch, "E379", {"start": v(-34.25, 12.2) * mm, "end": v(-33.94, 12.44) * mm});
            skLineSegment(sketch, "E380", {"start": v(-33.94, 12.44) * mm, "end": v(-33.7, 12.75) * mm});
            skLineSegment(sketch, "E381", {"start": v(-33.7, 12.75) * mm, "end": v(-33.55, 13.11) * mm});
            skLineSegment(sketch, "E382", {"start": v(-33.55, 13.11) * mm, "end": v(-33.5, 13.5) * mm});
            skLineSegment(sketch, "E383", {"start": v(-33.5, 13.5) * mm, "end": v(-33.55, 13.89) * mm});
            skLineSegment(sketch, "E384", {"start": v(-33.55, 13.89) * mm, "end": v(-33.7, 14.25) * mm});
            skLineSegment(sketch, "E385", {"start": v(-33.7, 14.25) * mm, "end": v(-33.94, 14.56) * mm});
            skLineSegment(sketch, "E386", {"start": v(-33.94, 14.56) * mm, "end": v(-34.25, 14.8) * mm});
            skLineSegment(sketch, "E387", {"start": v(-34.25, 14.8) * mm, "end": v(-34.61, 14.95) * mm});
            skLineSegment(sketch, "E388", {"start": v(-34.61, 14.95) * mm, "end": v(-35, 15) * mm});
            skLineSegment(sketch, "E389", {"start": v(-35, 15) * mm, "end": v(-35.39, 14.95) * mm});
            skLineSegment(sketch, "E390", {"start": v(-41.2, 31.75) * mm, "end": v(-41.44, 32.06) * mm});
            skLineSegment(sketch, "E391", {"start": v(-41.44, 32.06) * mm, "end": v(-41.75, 32.3) * mm});
            skLineSegment(sketch, "E392", {"start": v(-41.75, 32.3) * mm, "end": v(-42.11, 32.45) * mm});
            skLineSegment(sketch, "E393", {"start": v(-42.11, 32.45) * mm, "end": v(-42.5, 32.5) * mm});
            skLineSegment(sketch, "E394", {"start": v(-42.5, 32.5) * mm, "end": v(-42.89, 32.45) * mm});
            skLineSegment(sketch, "E395", {"start": v(-42.89, 32.45) * mm, "end": v(-43.25, 32.3) * mm});
            skLineSegment(sketch, "E396", {"start": v(-43.25, 32.3) * mm, "end": v(-43.56, 32.06) * mm});
            skLineSegment(sketch, "E397", {"start": v(-43.56, 32.06) * mm, "end": v(-43.8, 31.75) * mm});
            skLineSegment(sketch, "E398", {"start": v(-43.8, 31.75) * mm, "end": v(-43.95, 31.39) * mm});
            skLineSegment(sketch, "E399", {"start": v(-43.95, 31.39) * mm, "end": v(-44, 31) * mm});
            skLineSegment(sketch, "E400", {"start": v(-44, 31) * mm, "end": v(-43.95, 30.61) * mm});
            skLineSegment(sketch, "E401", {"start": v(-43.95, 30.61) * mm, "end": v(-43.8, 30.25) * mm});
            skLineSegment(sketch, "E402", {"start": v(-43.8, 30.25) * mm, "end": v(-43.56, 29.94) * mm});
            skLineSegment(sketch, "E403", {"start": v(-43.56, 29.94) * mm, "end": v(-43.25, 29.7) * mm});
            skLineSegment(sketch, "E404", {"start": v(-43.25, 29.7) * mm, "end": v(-42.89, 29.55) * mm});
            skLineSegment(sketch, "E405", {"start": v(-42.89, 29.55) * mm, "end": v(-42.5, 29.5) * mm});
            skLineSegment(sketch, "E406", {"start": v(-42.5, 29.5) * mm, "end": v(-42.11, 29.55) * mm});
            skLineSegment(sketch, "E407", {"start": v(-42.11, 29.55) * mm, "end": v(-41.75, 29.7) * mm});
            skLineSegment(sketch, "E408", {"start": v(-41.75, 29.7) * mm, "end": v(-41.44, 29.94) * mm});
            skLineSegment(sketch, "E409", {"start": v(-41.44, 29.94) * mm, "end": v(-41.2, 30.25) * mm});
            skLineSegment(sketch, "E410", {"start": v(-41.2, 30.25) * mm, "end": v(-41.05, 30.61) * mm});
            skLineSegment(sketch, "E411", {"start": v(-41.05, 30.61) * mm, "end": v(-41, 31) * mm});
            skLineSegment(sketch, "E412", {"start": v(-41, 31) * mm, "end": v(-41.05, 31.39) * mm});
            skLineSegment(sketch, "E413", {"start": v(-41.05, 31.39) * mm, "end": v(-41.2, 31.75) * mm});
            skLineSegment(sketch, "E414", {"start": v(-41.83, 39.66) * mm, "end": v(-41.5, 39.88) * mm});
            skLineSegment(sketch, "E415", {"start": v(-41.5, 39.88) * mm, "end": v(-41.25, 40.18) * mm});
            skLineSegment(sketch, "E416", {"start": v(-41.25, 40.18) * mm, "end": v(-41.08, 40.53) * mm});
            skLineSegment(sketch, "E417", {"start": v(-41.08, 40.53) * mm, "end": v(-41, 40.91) * mm});
            skLineSegment(sketch, "E418", {"start": v(-41, 40.91) * mm, "end": v(-41.03, 41.3) * mm});
            skLineSegment(sketch, "E419", {"start": v(-41.03, 41.3) * mm, "end": v(-41.16, 41.67) * mm});
            skLineSegment(sketch, "E420", {"start": v(-41.16, 41.67) * mm, "end": v(-41.38, 42) * mm});
            skLineSegment(sketch, "E421", {"start": v(-41.38, 42) * mm, "end": v(-41.68, 42.25) * mm});
            skLineSegment(sketch, "E422", {"start": v(-41.68, 42.25) * mm, "end": v(-42.03, 42.42) * mm});
            skLineSegment(sketch, "E423", {"start": v(-42.03, 42.42) * mm, "end": v(-42.41, 42.5) * mm});
            skLineSegment(sketch, "E424", {"start": v(-42.41, 42.5) * mm, "end": v(-42.8, 42.47) * mm});
            skLineSegment(sketch, "E425", {"start": v(-42.8, 42.47) * mm, "end": v(-43.17, 42.34) * mm});
            skLineSegment(sketch, "E426", {"start": v(-43.17, 42.34) * mm, "end": v(-43.5, 42.12) * mm});
            skLineSegment(sketch, "E427", {"start": v(-43.5, 42.12) * mm, "end": v(-43.75, 41.82) * mm});
            skLineSegment(sketch, "E428", {"start": v(-43.75, 41.82) * mm, "end": v(-43.92, 41.47) * mm});
            skLineSegment(sketch, "E429", {"start": v(-43.92, 41.47) * mm, "end": v(-44, 41.09) * mm});
            skLineSegment(sketch, "E430", {"start": v(-44, 41.09) * mm, "end": v(-43.97, 40.7) * mm});
            skLineSegment(sketch, "E431", {"start": v(-43.97, 40.7) * mm, "end": v(-43.84, 40.33) * mm});
            skLineSegment(sketch, "E432", {"start": v(-43.84, 40.33) * mm, "end": v(-43.62, 40) * mm});
            skLineSegment(sketch, "E433", {"start": v(-43.62, 40) * mm, "end": v(-43.32, 39.75) * mm});
            skLineSegment(sketch, "E434", {"start": v(-43.32, 39.75) * mm, "end": v(-42.97, 39.58) * mm});
            skLineSegment(sketch, "E435", {"start": v(-42.97, 39.58) * mm, "end": v(-42.59, 39.5) * mm});
            skLineSegment(sketch, "E436", {"start": v(-42.59, 39.5) * mm, "end": v(-42.2, 39.53) * mm});
            skLineSegment(sketch, "E437", {"start": v(-42.2, 39.53) * mm, "end": v(-41.83, 39.66) * mm});
            skLineSegment(sketch, "E438", {"start": v(42.89, 32.45) * mm, "end": v(42.5, 32.5) * mm});
            skLineSegment(sketch, "E439", {"start": v(42.5, 32.5) * mm, "end": v(42.11, 32.45) * mm});
            skLineSegment(sketch, "E440", {"start": v(42.11, 32.45) * mm, "end": v(41.75, 32.3) * mm});
            skLineSegment(sketch, "E441", {"start": v(41.75, 32.3) * mm, "end": v(41.44, 32.06) * mm});
            skLineSegment(sketch, "E442", {"start": v(41.44, 32.06) * mm, "end": v(41.2, 31.75) * mm});
            skLineSegment(sketch, "E443", {"start": v(41.2, 31.75) * mm, "end": v(41.05, 31.39) * mm});
            skLineSegment(sketch, "E444", {"start": v(41.05, 31.39) * mm, "end": v(41, 31) * mm});
            skLineSegment(sketch, "E445", {"start": v(41, 31) * mm, "end": v(41.05, 30.61) * mm});
            skLineSegment(sketch, "E446", {"start": v(41.05, 30.61) * mm, "end": v(41.2, 30.25) * mm});
            skLineSegment(sketch, "E447", {"start": v(41.2, 30.25) * mm, "end": v(41.44, 29.94) * mm});
            skLineSegment(sketch, "E448", {"start": v(41.44, 29.94) * mm, "end": v(41.75, 29.7) * mm});
            skLineSegment(sketch, "E449", {"start": v(41.75, 29.7) * mm, "end": v(42.11, 29.55) * mm});
            skLineSegment(sketch, "E450", {"start": v(42.11, 29.55) * mm, "end": v(42.5, 29.5) * mm});
            skLineSegment(sketch, "E451", {"start": v(42.5, 29.5) * mm, "end": v(42.89, 29.55) * mm});
            skLineSegment(sketch, "E452", {"start": v(42.89, 29.55) * mm, "end": v(43.25, 29.7) * mm});
            skLineSegment(sketch, "E453", {"start": v(43.25, 29.7) * mm, "end": v(43.56, 29.94) * mm});
            skLineSegment(sketch, "E454", {"start": v(43.56, 29.94) * mm, "end": v(43.8, 30.25) * mm});
            skLineSegment(sketch, "E455", {"start": v(43.8, 30.25) * mm, "end": v(43.95, 30.61) * mm});
            skLineSegment(sketch, "E456", {"start": v(43.95, 30.61) * mm, "end": v(44, 31) * mm});
            skLineSegment(sketch, "E457", {"start": v(44, 31) * mm, "end": v(43.95, 31.39) * mm});
            skLineSegment(sketch, "E458", {"start": v(43.95, 31.39) * mm, "end": v(43.8, 31.75) * mm});
            skLineSegment(sketch, "E459", {"start": v(43.8, 31.75) * mm, "end": v(43.56, 32.06) * mm});
            skLineSegment(sketch, "E460", {"start": v(43.56, 32.06) * mm, "end": v(43.25, 32.3) * mm});
            skLineSegment(sketch, "E461", {"start": v(43.25, 32.3) * mm, "end": v(42.89, 32.45) * mm});
            skLineSegment(sketch, "E462", {"start": v(41.75, 42.3) * mm, "end": v(41.44, 42.06) * mm});
            skLineSegment(sketch, "E463", {"start": v(41.44, 42.06) * mm, "end": v(41.2, 41.75) * mm});
            skLineSegment(sketch, "E464", {"start": v(41.2, 41.75) * mm, "end": v(41.05, 41.39) * mm});
            skLineSegment(sketch, "E465", {"start": v(41.05, 41.39) * mm, "end": v(41, 41) * mm});
            skLineSegment(sketch, "E466", {"start": v(41, 41) * mm, "end": v(41.05, 40.61) * mm});
            skLineSegment(sketch, "E467", {"start": v(41.05, 40.61) * mm, "end": v(41.2, 40.25) * mm});
            skLineSegment(sketch, "E468", {"start": v(41.2, 40.25) * mm, "end": v(41.44, 39.94) * mm});
            skLineSegment(sketch, "E469", {"start": v(41.44, 39.94) * mm, "end": v(41.75, 39.7) * mm});
            skLineSegment(sketch, "E470", {"start": v(41.75, 39.7) * mm, "end": v(42.11, 39.55) * mm});
            skLineSegment(sketch, "E471", {"start": v(42.11, 39.55) * mm, "end": v(42.5, 39.5) * mm});
            skLineSegment(sketch, "E472", {"start": v(42.5, 39.5) * mm, "end": v(42.89, 39.55) * mm});
            skLineSegment(sketch, "E473", {"start": v(42.89, 39.55) * mm, "end": v(43.25, 39.7) * mm});
            skLineSegment(sketch, "E474", {"start": v(43.25, 39.7) * mm, "end": v(43.56, 39.94) * mm});
            skLineSegment(sketch, "E475", {"start": v(43.56, 39.94) * mm, "end": v(43.8, 40.25) * mm});
            skLineSegment(sketch, "E476", {"start": v(43.8, 40.25) * mm, "end": v(43.95, 40.61) * mm});
            skLineSegment(sketch, "E477", {"start": v(43.95, 40.61) * mm, "end": v(44, 41) * mm});
            skLineSegment(sketch, "E478", {"start": v(44, 41) * mm, "end": v(43.95, 41.39) * mm});
            skLineSegment(sketch, "E479", {"start": v(43.95, 41.39) * mm, "end": v(43.8, 41.75) * mm});
            skLineSegment(sketch, "E480", {"start": v(43.8, 41.75) * mm, "end": v(43.56, 42.06) * mm});
            skLineSegment(sketch, "E481", {"start": v(43.56, 42.06) * mm, "end": v(43.25, 42.3) * mm});
            skLineSegment(sketch, "E482", {"start": v(43.25, 42.3) * mm, "end": v(42.89, 42.45) * mm});
            skLineSegment(sketch, "E483", {"start": v(42.89, 42.45) * mm, "end": v(42.5, 42.5) * mm});
            skLineSegment(sketch, "E484", {"start": v(42.5, 42.5) * mm, "end": v(42.11, 42.45) * mm});
            skLineSegment(sketch, "E485", {"start": v(42.11, 42.45) * mm, "end": v(41.75, 42.3) * mm});
            skLineSegment(sketch, "E486", {"start": v(-36.04, -26.86) * mm, "end": v(-35, -27) * mm});
            skLineSegment(sketch, "E487", {"start": v(-35, -27) * mm, "end": v(-33.96, -26.86) * mm});
            skLineSegment(sketch, "E488", {"start": v(-33.96, -26.86) * mm, "end": v(-33, -26.46) * mm});
            skLineSegment(sketch, "E489", {"start": v(-33, -26.46) * mm, "end": v(-32.17, -25.83) * mm});
            skLineSegment(sketch, "E490", {"start": v(-32.17, -25.83) * mm, "end": v(-31.54, -25) * mm});
            skLineSegment(sketch, "E491", {"start": v(-31.54, -25) * mm, "end": v(-31.14, -24.04) * mm});
            skLineSegment(sketch, "E492", {"start": v(-31.14, -24.04) * mm, "end": v(-31, -23) * mm});
            skLineSegment(sketch, "E493", {"start": v(-31, -23) * mm, "end": v(-31.14, -21.96) * mm});
            skLineSegment(sketch, "E494", {"start": v(-31.14, -21.96) * mm, "end": v(-31.54, -21) * mm});
            skLineSegment(sketch, "E495", {"start": v(-31.54, -21) * mm, "end": v(-32.17, -20.17) * mm});
            skLineSegment(sketch, "E496", {"start": v(-32.17, -20.17) * mm, "end": v(-33, -19.54) * mm});
            skLineSegment(sketch, "E497", {"start": v(-33, -19.54) * mm, "end": v(-33.96, -19.14) * mm});
            skLineSegment(sketch, "E498", {"start": v(-33.96, -19.14) * mm, "end": v(-35, -19) * mm});
            skLineSegment(sketch, "E499", {"start": v(-35, -19) * mm, "end": v(-36.04, -19.14) * mm});
            skLineSegment(sketch, "E500", {"start": v(-36.04, -19.14) * mm, "end": v(-37, -19.54) * mm});
            skLineSegment(sketch, "E501", {"start": v(-37, -19.54) * mm, "end": v(-37.83, -20.17) * mm});
            skLineSegment(sketch, "E502", {"start": v(-37.83, -20.17) * mm, "end": v(-38.46, -21) * mm});
            skLineSegment(sketch, "E503", {"start": v(-38.46, -21) * mm, "end": v(-38.86, -21.96) * mm});
            skLineSegment(sketch, "E504", {"start": v(-38.86, -21.96) * mm, "end": v(-39, -23) * mm});
            skLineSegment(sketch, "E505", {"start": v(-39, -23) * mm, "end": v(-38.86, -24.04) * mm});
            skLineSegment(sketch, "E506", {"start": v(-38.86, -24.04) * mm, "end": v(-38.46, -25) * mm});
            skLineSegment(sketch, "E507", {"start": v(-38.46, -25) * mm, "end": v(-37.83, -25.83) * mm});
            skLineSegment(sketch, "E508", {"start": v(-37.83, -25.83) * mm, "end": v(-37, -26.46) * mm});
            skLineSegment(sketch, "E509", {"start": v(-37, -26.46) * mm, "end": v(-36.04, -26.86) * mm});
            skLineSegment(sketch, "E510", {"start": v(32.17, -25.83) * mm, "end": v(33, -26.46) * mm});
            skLineSegment(sketch, "E511", {"start": v(33, -26.46) * mm, "end": v(33.96, -26.86) * mm});
            skLineSegment(sketch, "E512", {"start": v(33.96, -26.86) * mm, "end": v(35, -27) * mm});
            skLineSegment(sketch, "E513", {"start": v(35, -27) * mm, "end": v(36.04, -26.86) * mm});
            skLineSegment(sketch, "E514", {"start": v(36.04, -26.86) * mm, "end": v(37, -26.46) * mm});
            skLineSegment(sketch, "E515", {"start": v(37, -26.46) * mm, "end": v(37.83, -25.83) * mm});
            skLineSegment(sketch, "E516", {"start": v(37.83, -25.83) * mm, "end": v(38.46, -25) * mm});
            skLineSegment(sketch, "E517", {"start": v(38.46, -25) * mm, "end": v(38.86, -24.04) * mm});
            skLineSegment(sketch, "E518", {"start": v(38.86, -24.04) * mm, "end": v(39, -23) * mm});
            skLineSegment(sketch, "E519", {"start": v(39, -23) * mm, "end": v(38.86, -21.96) * mm});
            skLineSegment(sketch, "E520", {"start": v(38.86, -21.96) * mm, "end": v(38.46, -21) * mm});
            skLineSegment(sketch, "E521", {"start": v(38.46, -21) * mm, "end": v(37.83, -20.17) * mm});
            skLineSegment(sketch, "E522", {"start": v(37.83, -20.17) * mm, "end": v(37, -19.54) * mm});
            skLineSegment(sketch, "E523", {"start": v(37, -19.54) * mm, "end": v(36.04, -19.14) * mm});
            skLineSegment(sketch, "E524", {"start": v(36.04, -19.14) * mm, "end": v(35, -19) * mm});
            skLineSegment(sketch, "E525", {"start": v(35, -19) * mm, "end": v(33.96, -19.14) * mm});
            skLineSegment(sketch, "E526", {"start": v(33.96, -19.14) * mm, "end": v(33, -19.54) * mm});
            skLineSegment(sketch, "E527", {"start": v(33, -19.54) * mm, "end": v(32.17, -20.17) * mm});
            skLineSegment(sketch, "E528", {"start": v(32.17, -20.17) * mm, "end": v(31.54, -21) * mm});
            skLineSegment(sketch, "E529", {"start": v(31.54, -21) * mm, "end": v(31.14, -21.96) * mm});
            skLineSegment(sketch, "E530", {"start": v(31.14, -21.96) * mm, "end": v(31, -23) * mm});
            skLineSegment(sketch, "E531", {"start": v(31, -23) * mm, "end": v(31.14, -24.04) * mm});
            skLineSegment(sketch, "E532", {"start": v(31.14, -24.04) * mm, "end": v(31.54, -25) * mm});
            skLineSegment(sketch, "E533", {"start": v(31.54, -25) * mm, "end": v(32.17, -25.83) * mm});
            skSolve(sketch);
        }
        {
            var Q0;
            Q0=qCreatedBy(makeId("Front.planeOp"),FACE);
            cPlane(context, id + "F1", {"entities" : qUnion([Q0]), "cplaneType" : CPlaneType.OFFSET, "offset" : 50 * mm, "width" : 150 * mm, "height" : 150 * mm});
        }
        {
            var Q0;
            Q0=qCreatedBy(id+"F1.planeOp",FACE);
            var sketch = newSketch(context, id + "F2", { "sketchPlane" : qUnion([Q0])});
            skLineSegment(sketch, "E534", {"start": v(50, -75) * mm, "end": v(50, 75) * mm});
            skLineSegment(sketch, "E535", {"start": v(50, 75) * mm, "end": v(-50, 75) * mm});
            skLineSegment(sketch, "E536", {"start": v(-50, 75) * mm, "end": v(-50, -75) * mm});
            skLineSegment(sketch, "E537", {"start": v(-50, -75) * mm, "end": v(50, -75) * mm});
            skLineSegment(sketch, "E538", {"start": v(42.5, 31.5) * mm, "end": v(42.89, 31.45) * mm});
            skLineSegment(sketch, "E539", {"start": v(42.89, 31.45) * mm, "end": v(43.25, 31.3) * mm});
            skLineSegment(sketch, "E540", {"start": v(43.25, 31.3) * mm, "end": v(43.56, 31.06) * mm});
            skLineSegment(sketch, "E541", {"start": v(43.56, 31.06) * mm, "end": v(43.8, 30.75) * mm});
            skLineSegment(sketch, "E542", {"start": v(43.8, 30.75) * mm, "end": v(43.95, 30.39) * mm});
            skLineSegment(sketch, "E543", {"start": v(43.95, 30.39) * mm, "end": v(44, 30) * mm});
            skLineSegment(sketch, "E544", {"start": v(44, 30) * mm, "end": v(43.95, 29.61) * mm});
            skLineSegment(sketch, "E545", {"start": v(43.95, 29.61) * mm, "end": v(43.8, 29.25) * mm});
            skLineSegment(sketch, "E546", {"start": v(43.8, 29.25) * mm, "end": v(43.56, 28.94) * mm});
            skLineSegment(sketch, "E547", {"start": v(43.56, 28.94) * mm, "end": v(43.25, 28.7) * mm});
            skLineSegment(sketch, "E548", {"start": v(43.25, 28.7) * mm, "end": v(42.89, 28.55) * mm});
            skLineSegment(sketch, "E549", {"start": v(42.89, 28.55) * mm, "end": v(42.5, 28.5) * mm});
            skLineSegment(sketch, "E550", {"start": v(42.5, 28.5) * mm, "end": v(42.11, 28.55) * mm});
            skLineSegment(sketch, "E551", {"start": v(42.11, 28.55) * mm, "end": v(41.75, 28.7) * mm});
            skLineSegment(sketch, "E552", {"start": v(41.75, 28.7) * mm, "end": v(41.44, 28.94) * mm});
            skLineSegment(sketch, "E553", {"start": v(41.44, 28.94) * mm, "end": v(41.2, 29.25) * mm});
            skLineSegment(sketch, "E554", {"start": v(41.2, 29.25) * mm, "end": v(41.05, 29.61) * mm});
            skLineSegment(sketch, "E555", {"start": v(41.05, 29.61) * mm, "end": v(41, 30) * mm});
            skLineSegment(sketch, "E556", {"start": v(41, 30) * mm, "end": v(41.05, 30.39) * mm});
            skLineSegment(sketch, "E557", {"start": v(41.05, 30.39) * mm, "end": v(41.2, 30.75) * mm});
            skLineSegment(sketch, "E558", {"start": v(41.2, 30.75) * mm, "end": v(41.44, 31.06) * mm});
            skLineSegment(sketch, "E559", {"start": v(41.44, 31.06) * mm, "end": v(41.75, 31.3) * mm});
            skLineSegment(sketch, "E560", {"start": v(41.75, 31.3) * mm, "end": v(42.11, 31.45) * mm});
            skLineSegment(sketch, "E561", {"start": v(42.11, 31.45) * mm, "end": v(42.5, 31.5) * mm});
            skLineSegment(sketch, "E562", {"start": v(42.5, -1.5) * mm, "end": v(42.11, -1.45) * mm});
            skLineSegment(sketch, "E563", {"start": v(42.11, -1.45) * mm, "end": v(41.75, -1.3) * mm});
            skLineSegment(sketch, "E564", {"start": v(41.75, -1.3) * mm, "end": v(41.44, -1.06) * mm});
            skLineSegment(sketch, "E565", {"start": v(41.44, -1.06) * mm, "end": v(41.2, -0.75) * mm});
            skLineSegment(sketch, "E566", {"start": v(41.2, -0.75) * mm, "end": v(41.05, -0.39) * mm});
            skLineSegment(sketch, "E567", {"start": v(41.05, -0.39) * mm, "end": v(41, 0) * mm});
            skLineSegment(sketch, "E568", {"start": v(41, 0) * mm, "end": v(41.05, 0.39) * mm});
            skLineSegment(sketch, "E569", {"start": v(41.05, 0.39) * mm, "end": v(41.2, 0.75) * mm});
            skLineSegment(sketch, "E570", {"start": v(41.2, 0.75) * mm, "end": v(41.44, 1.06) * mm});
            skLineSegment(sketch, "E571", {"start": v(41.44, 1.06) * mm, "end": v(41.75, 1.3) * mm});
            skLineSegment(sketch, "E572", {"start": v(41.75, 1.3) * mm, "end": v(42.11, 1.45) * mm});
            skLineSegment(sketch, "E573", {"start": v(42.11, 1.45) * mm, "end": v(42.5, 1.5) * mm});
            skLineSegment(sketch, "E574", {"start": v(42.5, 1.5) * mm, "end": v(42.89, 1.45) * mm});
            skLineSegment(sketch, "E575", {"start": v(42.89, 1.45) * mm, "end": v(43.25, 1.3) * mm});
            skLineSegment(sketch, "E576", {"start": v(43.25, 1.3) * mm, "end": v(43.56, 1.06) * mm});
            skLineSegment(sketch, "E577", {"start": v(43.56, 1.06) * mm, "end": v(43.8, 0.75) * mm});
            skLineSegment(sketch, "E578", {"start": v(43.8, 0.75) * mm, "end": v(43.95, 0.39) * mm});
            skLineSegment(sketch, "E579", {"start": v(43.95, 0.39) * mm, "end": v(44, 0) * mm});
            skLineSegment(sketch, "E580", {"start": v(44, 0) * mm, "end": v(43.95, -0.39) * mm});
            skLineSegment(sketch, "E581", {"start": v(43.95, -0.39) * mm, "end": v(43.8, -0.75) * mm});
            skLineSegment(sketch, "E582", {"start": v(43.8, -0.75) * mm, "end": v(43.56, -1.06) * mm});
            skLineSegment(sketch, "E583", {"start": v(43.56, -1.06) * mm, "end": v(43.25, -1.3) * mm});
            skLineSegment(sketch, "E584", {"start": v(43.25, -1.3) * mm, "end": v(42.89, -1.45) * mm});
            skLineSegment(sketch, "E585", {"start": v(42.89, -1.45) * mm, "end": v(42.5, -1.5) * mm});
            skLineSegment(sketch, "E586", {"start": v(42.5, -31.5) * mm, "end": v(42.11, -31.45) * mm});
            skLineSegment(sketch, "E587", {"start": v(42.11, -31.45) * mm, "end": v(41.75, -31.3) * mm});
            skLineSegment(sketch, "E588", {"start": v(41.75, -31.3) * mm, "end": v(41.44, -31.06) * mm});
            skLineSegment(sketch, "E589", {"start": v(41.44, -31.06) * mm, "end": v(41.2, -30.75) * mm});
            skLineSegment(sketch, "E590", {"start": v(41.2, -30.75) * mm, "end": v(41.05, -30.39) * mm});
            skLineSegment(sketch, "E591", {"start": v(41.05, -30.39) * mm, "end": v(41, -30) * mm});
            skLineSegment(sketch, "E592", {"start": v(41, -30) * mm, "end": v(41.05, -29.61) * mm});
            skLineSegment(sketch, "E593", {"start": v(41.05, -29.61) * mm, "end": v(41.2, -29.25) * mm});
            skLineSegment(sketch, "E594", {"start": v(41.2, -29.25) * mm, "end": v(41.44, -28.94) * mm});
            skLineSegment(sketch, "E595", {"start": v(41.44, -28.94) * mm, "end": v(41.75, -28.7) * mm});
            skLineSegment(sketch, "E596", {"start": v(41.75, -28.7) * mm, "end": v(42.11, -28.55) * mm});
            skLineSegment(sketch, "E597", {"start": v(42.11, -28.55) * mm, "end": v(42.5, -28.5) * mm});
            skLineSegment(sketch, "E598", {"start": v(42.5, -28.5) * mm, "end": v(42.89, -28.55) * mm});
            skLineSegment(sketch, "E599", {"start": v(42.89, -28.55) * mm, "end": v(43.25, -28.7) * mm});
            skLineSegment(sketch, "E600", {"start": v(43.25, -28.7) * mm, "end": v(43.56, -28.94) * mm});
            skLineSegment(sketch, "E601", {"start": v(43.56, -28.94) * mm, "end": v(43.8, -29.25) * mm});
            skLineSegment(sketch, "E602", {"start": v(43.8, -29.25) * mm, "end": v(43.95, -29.61) * mm});
            skLineSegment(sketch, "E603", {"start": v(43.95, -29.61) * mm, "end": v(44, -30) * mm});
            skLineSegment(sketch, "E604", {"start": v(44, -30) * mm, "end": v(43.95, -30.39) * mm});
            skLineSegment(sketch, "E605", {"start": v(43.95, -30.39) * mm, "end": v(43.8, -30.75) * mm});
            skLineSegment(sketch, "E606", {"start": v(43.8, -30.75) * mm, "end": v(43.56, -31.06) * mm});
            skLineSegment(sketch, "E607", {"start": v(43.56, -31.06) * mm, "end": v(43.25, -31.3) * mm});
            skLineSegment(sketch, "E608", {"start": v(43.25, -31.3) * mm, "end": v(42.89, -31.45) * mm});
            skLineSegment(sketch, "E609", {"start": v(42.89, -31.45) * mm, "end": v(42.5, -31.5) * mm});
            skLineSegment(sketch, "E610", {"start": v(41.75, -66.3) * mm, "end": v(41.44, -66.06) * mm});
            skLineSegment(sketch, "E611", {"start": v(41.44, -66.06) * mm, "end": v(41.2, -65.75) * mm});
            skLineSegment(sketch, "E612", {"start": v(41.2, -65.75) * mm, "end": v(41.05, -65.39) * mm});
            skLineSegment(sketch, "E613", {"start": v(41.05, -65.39) * mm, "end": v(41, -65) * mm});
            skLineSegment(sketch, "E614", {"start": v(41, -65) * mm, "end": v(41.05, -64.61) * mm});
            skLineSegment(sketch, "E615", {"start": v(41.05, -64.61) * mm, "end": v(41.2, -64.25) * mm});
            skLineSegment(sketch, "E616", {"start": v(41.2, -64.25) * mm, "end": v(41.44, -63.94) * mm});
            skLineSegment(sketch, "E617", {"start": v(41.44, -63.94) * mm, "end": v(41.75, -63.7) * mm});
            skLineSegment(sketch, "E618", {"start": v(41.75, -63.7) * mm, "end": v(42.11, -63.55) * mm});
            skLineSegment(sketch, "E619", {"start": v(42.11, -63.55) * mm, "end": v(42.5, -63.5) * mm});
            skLineSegment(sketch, "E620", {"start": v(42.5, -63.5) * mm, "end": v(42.89, -63.55) * mm});
            skLineSegment(sketch, "E621", {"start": v(42.89, -63.55) * mm, "end": v(43.25, -63.7) * mm});
            skLineSegment(sketch, "E622", {"start": v(43.25, -63.7) * mm, "end": v(43.56, -63.94) * mm});
            skLineSegment(sketch, "E623", {"start": v(43.56, -63.94) * mm, "end": v(43.8, -64.25) * mm});
            skLineSegment(sketch, "E624", {"start": v(43.8, -64.25) * mm, "end": v(43.95, -64.61) * mm});
            skLineSegment(sketch, "E625", {"start": v(43.95, -64.61) * mm, "end": v(44, -65) * mm});
            skLineSegment(sketch, "E626", {"start": v(44, -65) * mm, "end": v(43.95, -65.39) * mm});
            skLineSegment(sketch, "E627", {"start": v(43.95, -65.39) * mm, "end": v(43.8, -65.75) * mm});
            skLineSegment(sketch, "E628", {"start": v(43.8, -65.75) * mm, "end": v(43.56, -66.06) * mm});
            skLineSegment(sketch, "E629", {"start": v(43.56, -66.06) * mm, "end": v(43.25, -66.3) * mm});
            skLineSegment(sketch, "E630", {"start": v(43.25, -66.3) * mm, "end": v(42.89, -66.45) * mm});
            skLineSegment(sketch, "E631", {"start": v(42.89, -66.45) * mm, "end": v(42.5, -66.5) * mm});
            skLineSegment(sketch, "E632", {"start": v(42.5, -66.5) * mm, "end": v(42.11, -66.45) * mm});
            skLineSegment(sketch, "E633", {"start": v(42.11, -66.45) * mm, "end": v(41.75, -66.3) * mm});
            skLineSegment(sketch, "E634", {"start": v(41.44, 66.06) * mm, "end": v(41.75, 66.3) * mm});
            skLineSegment(sketch, "E635", {"start": v(41.75, 66.3) * mm, "end": v(42.11, 66.45) * mm});
            skLineSegment(sketch, "E636", {"start": v(42.11, 66.45) * mm, "end": v(42.5, 66.5) * mm});
            skLineSegment(sketch, "E637", {"start": v(42.5, 66.5) * mm, "end": v(42.89, 66.45) * mm});
            skLineSegment(sketch, "E638", {"start": v(42.89, 66.45) * mm, "end": v(43.25, 66.3) * mm});
            skLineSegment(sketch, "E639", {"start": v(43.25, 66.3) * mm, "end": v(43.56, 66.06) * mm});
            skLineSegment(sketch, "E640", {"start": v(43.56, 66.06) * mm, "end": v(43.8, 65.75) * mm});
            skLineSegment(sketch, "E641", {"start": v(43.8, 65.75) * mm, "end": v(43.95, 65.39) * mm});
            skLineSegment(sketch, "E642", {"start": v(43.95, 65.39) * mm, "end": v(44, 65) * mm});
            skLineSegment(sketch, "E643", {"start": v(44, 65) * mm, "end": v(43.95, 64.61) * mm});
            skLineSegment(sketch, "E644", {"start": v(43.95, 64.61) * mm, "end": v(43.8, 64.25) * mm});
            skLineSegment(sketch, "E645", {"start": v(43.8, 64.25) * mm, "end": v(43.56, 63.94) * mm});
            skLineSegment(sketch, "E646", {"start": v(43.56, 63.94) * mm, "end": v(43.25, 63.7) * mm});
            skLineSegment(sketch, "E647", {"start": v(43.25, 63.7) * mm, "end": v(42.89, 63.55) * mm});
            skLineSegment(sketch, "E648", {"start": v(42.89, 63.55) * mm, "end": v(42.5, 63.5) * mm});
            skLineSegment(sketch, "E649", {"start": v(42.5, 63.5) * mm, "end": v(42.11, 63.55) * mm});
            skLineSegment(sketch, "E650", {"start": v(42.11, 63.55) * mm, "end": v(41.75, 63.7) * mm});
            skLineSegment(sketch, "E651", {"start": v(41.75, 63.7) * mm, "end": v(41.44, 63.94) * mm});
            skLineSegment(sketch, "E652", {"start": v(41.44, 63.94) * mm, "end": v(41.2, 64.25) * mm});
            skLineSegment(sketch, "E653", {"start": v(41.2, 64.25) * mm, "end": v(41.05, 64.61) * mm});
            skLineSegment(sketch, "E654", {"start": v(41.05, 64.61) * mm, "end": v(41, 65) * mm});
            skLineSegment(sketch, "E655", {"start": v(41, 65) * mm, "end": v(41.05, 65.39) * mm});
            skLineSegment(sketch, "E656", {"start": v(41.05, 65.39) * mm, "end": v(41.2, 65.75) * mm});
            skLineSegment(sketch, "E657", {"start": v(41.2, 65.75) * mm, "end": v(41.44, 66.06) * mm});
            skLineSegment(sketch, "E658", {"start": v(-43.56, 66.06) * mm, "end": v(-43.25, 66.3) * mm});
            skLineSegment(sketch, "E659", {"start": v(-43.25, 66.3) * mm, "end": v(-42.89, 66.45) * mm});
            skLineSegment(sketch, "E660", {"start": v(-42.89, 66.45) * mm, "end": v(-42.5, 66.5) * mm});
            skLineSegment(sketch, "E661", {"start": v(-42.5, 66.5) * mm, "end": v(-42.11, 66.45) * mm});
            skLineSegment(sketch, "E662", {"start": v(-42.11, 66.45) * mm, "end": v(-41.75, 66.3) * mm});
            skLineSegment(sketch, "E663", {"start": v(-41.75, 66.3) * mm, "end": v(-41.44, 66.06) * mm});
            skLineSegment(sketch, "E664", {"start": v(-41.44, 66.06) * mm, "end": v(-41.2, 65.75) * mm});
            skLineSegment(sketch, "E665", {"start": v(-41.2, 65.75) * mm, "end": v(-41.05, 65.39) * mm});
            skLineSegment(sketch, "E666", {"start": v(-41.05, 65.39) * mm, "end": v(-41, 65) * mm});
            skLineSegment(sketch, "E667", {"start": v(-41, 65) * mm, "end": v(-41.05, 64.61) * mm});
            skLineSegment(sketch, "E668", {"start": v(-41.05, 64.61) * mm, "end": v(-41.2, 64.25) * mm});
            skLineSegment(sketch, "E669", {"start": v(-41.2, 64.25) * mm, "end": v(-41.44, 63.94) * mm});
            skLineSegment(sketch, "E670", {"start": v(-41.44, 63.94) * mm, "end": v(-41.75, 63.7) * mm});
            skLineSegment(sketch, "E671", {"start": v(-41.75, 63.7) * mm, "end": v(-42.11, 63.55) * mm});
            skLineSegment(sketch, "E672", {"start": v(-42.11, 63.55) * mm, "end": v(-42.5, 63.5) * mm});
            skLineSegment(sketch, "E673", {"start": v(-42.5, 63.5) * mm, "end": v(-42.89, 63.55) * mm});
            skLineSegment(sketch, "E674", {"start": v(-42.89, 63.55) * mm, "end": v(-43.25, 63.7) * mm});
            skLineSegment(sketch, "E675", {"start": v(-43.25, 63.7) * mm, "end": v(-43.56, 63.94) * mm});
            skLineSegment(sketch, "E676", {"start": v(-43.56, 63.94) * mm, "end": v(-43.8, 64.25) * mm});
            skLineSegment(sketch, "E677", {"start": v(-43.8, 64.25) * mm, "end": v(-43.95, 64.61) * mm});
            skLineSegment(sketch, "E678", {"start": v(-43.95, 64.61) * mm, "end": v(-44, 65) * mm});
            skLineSegment(sketch, "E679", {"start": v(-44, 65) * mm, "end": v(-43.95, 65.39) * mm});
            skLineSegment(sketch, "E680", {"start": v(-43.95, 65.39) * mm, "end": v(-43.8, 65.75) * mm});
            skLineSegment(sketch, "E681", {"start": v(-43.8, 65.75) * mm, "end": v(-43.56, 66.06) * mm});
            skLineSegment(sketch, "E682", {"start": v(-42.89, 31.45) * mm, "end": v(-42.5, 31.5) * mm});
            skLineSegment(sketch, "E683", {"start": v(-42.5, 31.5) * mm, "end": v(-42.11, 31.45) * mm});
            skLineSegment(sketch, "E684", {"start": v(-42.11, 31.45) * mm, "end": v(-41.75, 31.3) * mm});
            skLineSegment(sketch, "E685", {"start": v(-41.75, 31.3) * mm, "end": v(-41.44, 31.06) * mm});
            skLineSegment(sketch, "E686", {"start": v(-41.44, 31.06) * mm, "end": v(-41.2, 30.75) * mm});
            skLineSegment(sketch, "E687", {"start": v(-41.2, 30.75) * mm, "end": v(-41.05, 30.39) * mm});
            skLineSegment(sketch, "E688", {"start": v(-41.05, 30.39) * mm, "end": v(-41, 30) * mm});
            skLineSegment(sketch, "E689", {"start": v(-41, 30) * mm, "end": v(-41.05, 29.61) * mm});
            skLineSegment(sketch, "E690", {"start": v(-41.05, 29.61) * mm, "end": v(-41.2, 29.25) * mm});
            skLineSegment(sketch, "E691", {"start": v(-41.2, 29.25) * mm, "end": v(-41.44, 28.94) * mm});
            skLineSegment(sketch, "E692", {"start": v(-41.44, 28.94) * mm, "end": v(-41.75, 28.7) * mm});
            skLineSegment(sketch, "E693", {"start": v(-41.75, 28.7) * mm, "end": v(-42.11, 28.55) * mm});
            skLineSegment(sketch, "E694", {"start": v(-42.11, 28.55) * mm, "end": v(-42.5, 28.5) * mm});
            skLineSegment(sketch, "E695", {"start": v(-42.5, 28.5) * mm, "end": v(-42.89, 28.55) * mm});
            skLineSegment(sketch, "E696", {"start": v(-42.89, 28.55) * mm, "end": v(-43.25, 28.7) * mm});
            skLineSegment(sketch, "E697", {"start": v(-43.25, 28.7) * mm, "end": v(-43.56, 28.94) * mm});
            skLineSegment(sketch, "E698", {"start": v(-43.56, 28.94) * mm, "end": v(-43.8, 29.25) * mm});
            skLineSegment(sketch, "E699", {"start": v(-43.8, 29.25) * mm, "end": v(-43.95, 29.61) * mm});
            skLineSegment(sketch, "E700", {"start": v(-43.95, 29.61) * mm, "end": v(-44, 30) * mm});
            skLineSegment(sketch, "E701", {"start": v(-44, 30) * mm, "end": v(-43.95, 30.39) * mm});
            skLineSegment(sketch, "E702", {"start": v(-43.95, 30.39) * mm, "end": v(-43.8, 30.75) * mm});
            skLineSegment(sketch, "E703", {"start": v(-43.8, 30.75) * mm, "end": v(-43.56, 31.06) * mm});
            skLineSegment(sketch, "E704", {"start": v(-43.56, 31.06) * mm, "end": v(-43.25, 31.3) * mm});
            skLineSegment(sketch, "E705", {"start": v(-43.25, 31.3) * mm, "end": v(-42.89, 31.45) * mm});
            skLineSegment(sketch, "E706", {"start": v(-43.95, -30.39) * mm, "end": v(-44, -30) * mm});
            skLineSegment(sketch, "E707", {"start": v(-44, -30) * mm, "end": v(-43.95, -29.61) * mm});
            skLineSegment(sketch, "E708", {"start": v(-43.95, -29.61) * mm, "end": v(-43.8, -29.25) * mm});
            skLineSegment(sketch, "E709", {"start": v(-43.8, -29.25) * mm, "end": v(-43.56, -28.94) * mm});
            skLineSegment(sketch, "E710", {"start": v(-43.56, -28.94) * mm, "end": v(-43.25, -28.7) * mm});
            skLineSegment(sketch, "E711", {"start": v(-43.25, -28.7) * mm, "end": v(-42.89, -28.55) * mm});
            skLineSegment(sketch, "E712", {"start": v(-42.89, -28.55) * mm, "end": v(-42.5, -28.5) * mm});
            skLineSegment(sketch, "E713", {"start": v(-42.5, -28.5) * mm, "end": v(-42.11, -28.55) * mm});
            skLineSegment(sketch, "E714", {"start": v(-42.11, -28.55) * mm, "end": v(-41.75, -28.7) * mm});
            skLineSegment(sketch, "E715", {"start": v(-41.75, -28.7) * mm, "end": v(-41.44, -28.94) * mm});
            skLineSegment(sketch, "E716", {"start": v(-41.44, -28.94) * mm, "end": v(-41.2, -29.25) * mm});
            skLineSegment(sketch, "E717", {"start": v(-41.2, -29.25) * mm, "end": v(-41.05, -29.61) * mm});
            skLineSegment(sketch, "E718", {"start": v(-41.05, -29.61) * mm, "end": v(-41, -30) * mm});
            skLineSegment(sketch, "E719", {"start": v(-41, -30) * mm, "end": v(-41.05, -30.39) * mm});
            skLineSegment(sketch, "E720", {"start": v(-41.05, -30.39) * mm, "end": v(-41.2, -30.75) * mm});
            skLineSegment(sketch, "E721", {"start": v(-41.2, -30.75) * mm, "end": v(-41.44, -31.06) * mm});
            skLineSegment(sketch, "E722", {"start": v(-41.44, -31.06) * mm, "end": v(-41.75, -31.3) * mm});
            skLineSegment(sketch, "E723", {"start": v(-41.75, -31.3) * mm, "end": v(-42.11, -31.45) * mm});
            skLineSegment(sketch, "E724", {"start": v(-42.11, -31.45) * mm, "end": v(-42.5, -31.5) * mm});
            skLineSegment(sketch, "E725", {"start": v(-42.5, -31.5) * mm, "end": v(-42.89, -31.45) * mm});
            skLineSegment(sketch, "E726", {"start": v(-42.89, -31.45) * mm, "end": v(-43.25, -31.3) * mm});
            skLineSegment(sketch, "E727", {"start": v(-43.25, -31.3) * mm, "end": v(-43.56, -31.06) * mm});
            skLineSegment(sketch, "E728", {"start": v(-43.56, -31.06) * mm, "end": v(-43.8, -30.75) * mm});
            skLineSegment(sketch, "E729", {"start": v(-43.8, -30.75) * mm, "end": v(-43.95, -30.39) * mm});
            skLineSegment(sketch, "E730", {"start": v(-42.11, -66.45) * mm, "end": v(-42.5, -66.5) * mm});
            skLineSegment(sketch, "E731", {"start": v(-42.5, -66.5) * mm, "end": v(-42.89, -66.45) * mm});
            skLineSegment(sketch, "E732", {"start": v(-42.89, -66.45) * mm, "end": v(-43.25, -66.3) * mm});
            skLineSegment(sketch, "E733", {"start": v(-43.25, -66.3) * mm, "end": v(-43.56, -66.06) * mm});
            skLineSegment(sketch, "E734", {"start": v(-43.56, -66.06) * mm, "end": v(-43.8, -65.75) * mm});
            skLineSegment(sketch, "E735", {"start": v(-43.8, -65.75) * mm, "end": v(-43.95, -65.39) * mm});
            skLineSegment(sketch, "E736", {"start": v(-43.95, -65.39) * mm, "end": v(-44, -65) * mm});
            skLineSegment(sketch, "E737", {"start": v(-44, -65) * mm, "end": v(-43.95, -64.61) * mm});
            skLineSegment(sketch, "E738", {"start": v(-43.95, -64.61) * mm, "end": v(-43.8, -64.25) * mm});
            skLineSegment(sketch, "E739", {"start": v(-43.8, -64.25) * mm, "end": v(-43.56, -63.94) * mm});
            skLineSegment(sketch, "E740", {"start": v(-43.56, -63.94) * mm, "end": v(-43.25, -63.7) * mm});
            skLineSegment(sketch, "E741", {"start": v(-43.25, -63.7) * mm, "end": v(-42.89, -63.55) * mm});
            skLineSegment(sketch, "E742", {"start": v(-42.89, -63.55) * mm, "end": v(-42.5, -63.5) * mm});
            skLineSegment(sketch, "E743", {"start": v(-42.5, -63.5) * mm, "end": v(-42.11, -63.55) * mm});
            skLineSegment(sketch, "E744", {"start": v(-42.11, -63.55) * mm, "end": v(-41.75, -63.7) * mm});
            skLineSegment(sketch, "E745", {"start": v(-41.75, -63.7) * mm, "end": v(-41.44, -63.94) * mm});
            skLineSegment(sketch, "E746", {"start": v(-41.44, -63.94) * mm, "end": v(-41.2, -64.25) * mm});
            skLineSegment(sketch, "E747", {"start": v(-41.2, -64.25) * mm, "end": v(-41.05, -64.61) * mm});
            skLineSegment(sketch, "E748", {"start": v(-41.05, -64.61) * mm, "end": v(-41, -65) * mm});
            skLineSegment(sketch, "E749", {"start": v(-41, -65) * mm, "end": v(-41.05, -65.39) * mm});
            skLineSegment(sketch, "E750", {"start": v(-41.05, -65.39) * mm, "end": v(-41.2, -65.75) * mm});
            skLineSegment(sketch, "E751", {"start": v(-41.2, -65.75) * mm, "end": v(-41.44, -66.06) * mm});
            skLineSegment(sketch, "E752", {"start": v(-41.44, -66.06) * mm, "end": v(-41.75, -66.3) * mm});
            skLineSegment(sketch, "E753", {"start": v(-41.75, -66.3) * mm, "end": v(-42.11, -66.45) * mm});
            skLineSegment(sketch, "E754", {"start": v(-42.11, -1.45) * mm, "end": v(-42.5, -1.5) * mm});
            skLineSegment(sketch, "E755", {"start": v(-42.5, -1.5) * mm, "end": v(-42.89, -1.45) * mm});
            skLineSegment(sketch, "E756", {"start": v(-42.89, -1.45) * mm, "end": v(-43.25, -1.3) * mm});
            skLineSegment(sketch, "E757", {"start": v(-43.25, -1.3) * mm, "end": v(-43.56, -1.06) * mm});
            skLineSegment(sketch, "E758", {"start": v(-43.56, -1.06) * mm, "end": v(-43.8, -0.75) * mm});
            skLineSegment(sketch, "E759", {"start": v(-43.8, -0.75) * mm, "end": v(-43.95, -0.39) * mm});
            skLineSegment(sketch, "E760", {"start": v(-43.95, -0.39) * mm, "end": v(-44, 0) * mm});
            skLineSegment(sketch, "E761", {"start": v(-44, 0) * mm, "end": v(-43.95, 0.39) * mm});
            skLineSegment(sketch, "E762", {"start": v(-43.95, 0.39) * mm, "end": v(-43.8, 0.75) * mm});
            skLineSegment(sketch, "E763", {"start": v(-43.8, 0.75) * mm, "end": v(-43.56, 1.06) * mm});
            skLineSegment(sketch, "E764", {"start": v(-43.56, 1.06) * mm, "end": v(-43.25, 1.3) * mm});
            skLineSegment(sketch, "E765", {"start": v(-43.25, 1.3) * mm, "end": v(-42.89, 1.45) * mm});
            skLineSegment(sketch, "E766", {"start": v(-42.89, 1.45) * mm, "end": v(-42.5, 1.5) * mm});
            skLineSegment(sketch, "E767", {"start": v(-42.5, 1.5) * mm, "end": v(-42.11, 1.45) * mm});
            skLineSegment(sketch, "E768", {"start": v(-42.11, 1.45) * mm, "end": v(-41.75, 1.3) * mm});
            skLineSegment(sketch, "E769", {"start": v(-41.75, 1.3) * mm, "end": v(-41.44, 1.06) * mm});
            skLineSegment(sketch, "E770", {"start": v(-41.44, 1.06) * mm, "end": v(-41.2, 0.75) * mm});
            skLineSegment(sketch, "E771", {"start": v(-41.2, 0.75) * mm, "end": v(-41.05, 0.39) * mm});
            skLineSegment(sketch, "E772", {"start": v(-41.05, 0.39) * mm, "end": v(-41, 0) * mm});
            skLineSegment(sketch, "E773", {"start": v(-41, 0) * mm, "end": v(-41.05, -0.39) * mm});
            skLineSegment(sketch, "E774", {"start": v(-41.05, -0.39) * mm, "end": v(-41.2, -0.75) * mm});
            skLineSegment(sketch, "E775", {"start": v(-41.2, -0.75) * mm, "end": v(-41.44, -1.06) * mm});
            skLineSegment(sketch, "E776", {"start": v(-41.44, -1.06) * mm, "end": v(-41.75, -1.3) * mm});
            skLineSegment(sketch, "E777", {"start": v(-41.75, -1.3) * mm, "end": v(-42.11, -1.45) * mm});
            skSolve(sketch);
        }
        {
            var Q0;
            Q0=qCreatedBy(id+"F1.planeOp",FACE);
            cPlane(context, id + "F3", {"entities" : qUnion([Q0]), "cplaneType" : CPlaneType.OFFSET, "offset" : 50 * mm, "width" : 150 * mm, "height" : 150 * mm});
        }
        {
            var Q0;
            Q0=qCreatedBy(id+"F3.planeOp",FACE);
            var sketch = newSketch(context, id + "F4", { "sketchPlane" : qUnion([Q0])});
            skLineSegment(sketch, "E778", {"start": v(75, 15) * mm, "end": v(75, -15) * mm});
            skLineSegment(sketch, "E779", {"start": v(75, -15) * mm, "end": v(-75, -15) * mm});
            skLineSegment(sketch, "E780", {"start": v(-75, -15) * mm, "end": v(-75, 15) * mm});
            skLineSegment(sketch, "E781", {"start": v(-75, 15) * mm, "end": v(75, 15) * mm});
            skLineSegment(sketch, "E782", {"start": v(4.5, 0) * mm, "end": v(4.35, 1.16) * mm});
            skLineSegment(sketch, "E783", {"start": v(4.35, 1.16) * mm, "end": v(3.9, 2.25) * mm});
            skLineSegment(sketch, "E784", {"start": v(3.9, 2.25) * mm, "end": v(3.18, 3.18) * mm});
            skLineSegment(sketch, "E785", {"start": v(3.18, 3.18) * mm, "end": v(2.25, 3.9) * mm});
            skLineSegment(sketch, "E786", {"start": v(2.25, 3.9) * mm, "end": v(1.16, 4.35) * mm});
            skLineSegment(sketch, "E787", {"start": v(1.16, 4.35) * mm, "end": v(0, 4.5) * mm});
            skLineSegment(sketch, "E788", {"start": v(0, 4.5) * mm, "end": v(-1.16, 4.35) * mm});
            skLineSegment(sketch, "E789", {"start": v(-1.16, 4.35) * mm, "end": v(-2.25, 3.9) * mm});
            skLineSegment(sketch, "E790", {"start": v(-2.25, 3.9) * mm, "end": v(-3.18, 3.18) * mm});
            skLineSegment(sketch, "E791", {"start": v(-3.18, 3.18) * mm, "end": v(-3.9, 2.25) * mm});
            skLineSegment(sketch, "E792", {"start": v(-3.9, 2.25) * mm, "end": v(-4.35, 1.16) * mm});
            skLineSegment(sketch, "E793", {"start": v(-4.35, 1.16) * mm, "end": v(-4.5, 0) * mm});
            skLineSegment(sketch, "E794", {"start": v(-4.5, 0) * mm, "end": v(-4.35, -1.16) * mm});
            skLineSegment(sketch, "E795", {"start": v(-4.35, -1.16) * mm, "end": v(-3.9, -2.25) * mm});
            skLineSegment(sketch, "E796", {"start": v(-3.9, -2.25) * mm, "end": v(-3.18, -3.18) * mm});
            skLineSegment(sketch, "E797", {"start": v(-3.18, -3.18) * mm, "end": v(-2.25, -3.9) * mm});
            skLineSegment(sketch, "E798", {"start": v(-2.25, -3.9) * mm, "end": v(-1.16, -4.35) * mm});
            skLineSegment(sketch, "E799", {"start": v(-1.16, -4.35) * mm, "end": v(0, -4.5) * mm});
            skLineSegment(sketch, "E800", {"start": v(0, -4.5) * mm, "end": v(1.16, -4.35) * mm});
            skLineSegment(sketch, "E801", {"start": v(1.16, -4.35) * mm, "end": v(2.25, -3.9) * mm});
            skLineSegment(sketch, "E802", {"start": v(2.25, -3.9) * mm, "end": v(3.18, -3.18) * mm});
            skLineSegment(sketch, "E803", {"start": v(3.18, -3.18) * mm, "end": v(3.9, -2.25) * mm});
            skLineSegment(sketch, "E804", {"start": v(3.9, -2.25) * mm, "end": v(4.35, -1.16) * mm});
            skLineSegment(sketch, "E805", {"start": v(4.35, -1.16) * mm, "end": v(4.5, 0) * mm});
            skCircle(sketch, "E806", {"center": v(-50, 0) * mm, "radius": 7.5 * mm});
            skCircle(sketch, "E807", {"center": v(50, 0) * mm, "radius": 7.5 * mm});
            skSolve(sketch);
        }
        {
            var Q0;
            Q0=qCreatedBy(id+"F3.planeOp",FACE);
            cPlane(context, id + "F5", {"entities" : qUnion([Q0]), "cplaneType" : CPlaneType.OFFSET, "offset" : 50 * mm, "width" : 150 * mm, "height" : 150 * mm});
        }
        {
            var Q0;
            Q0=qCreatedBy(id+"F5.planeOp",FACE);
            var sketch = newSketch(context, id + "F6", { "sketchPlane" : qUnion([Q0])});
            skLineSegment(sketch, "E808", {"start": v(-75, -15) * mm, "end": v(-75, 15) * mm});
            skLineSegment(sketch, "E809", {"start": v(-75, 15) * mm, "end": v(75, 15) * mm});
            skLineSegment(sketch, "E810", {"start": v(75, 15) * mm, "end": v(75, -15) * mm});
            skLineSegment(sketch, "E811", {"start": v(75, -15) * mm, "end": v(-75, -15) * mm});
            skCircle(sketch, "E812", {"center": v(50, 0) * mm, "radius": 7.5 * mm});
            skCircle(sketch, "E813", {"center": v(0, 0) * mm, "radius": 10 * mm});
            skCircle(sketch, "E814", {"center": v(-50, 0) * mm, "radius": 7.5 * mm});
            skCircle(sketch, "E815", {"center": v(-20, 0) * mm, "radius": 1.5 * mm});
            skCircle(sketch, "E816", {"center": v(20, 0) * mm, "radius": 1.5 * mm});
            skSolve(sketch);
        }
        {
            var Q0;
            Q0=qCreatedBy(makeId("Front.planeOp"),FACE);
            cPlane(context, id + "F7", {"entities" : qUnion([Q0]), "cplaneType" : CPlaneType.OFFSET, "offset" : 50 * mm, "oppositeDirection" : true, "width" : 150 * mm, "height" : 150 * mm});
        }
        {
            var Q0;
            Q0=qCreatedBy(id+"F7.planeOp",FACE);
            var sketch = newSketch(context, id + "F8", { "sketchPlane" : qUnion([Q0])});
            skLineSegment(sketch, "E817", {"start": v(-50, -47.5) * mm, "end": v(50, -47.5) * mm});
            skLineSegment(sketch, "E818", {"start": v(50, -47.5) * mm, "end": v(50, 47.5) * mm});
            skLineSegment(sketch, "E819", {"start": v(50, 47.5) * mm, "end": v(-50, 47.5) * mm});
            skLineSegment(sketch, "E820", {"start": v(-50, 47.5) * mm, "end": v(-50, -47.5) * mm});
            skLineSegment(sketch, "E821", {"start": v(-2.85, -15.87) * mm, "end": v(0, -15.5) * mm});
            skLineSegment(sketch, "E822", {"start": v(0, -15.5) * mm, "end": v(2.85, -15.87) * mm});
            skLineSegment(sketch, "E823", {"start": v(2.85, -15.87) * mm, "end": v(5.5, -16.97) * mm});
            skLineSegment(sketch, "E824", {"start": v(5.5, -16.97) * mm, "end": v(7.78, -18.72) * mm});
            skLineSegment(sketch, "E825", {"start": v(7.78, -18.72) * mm, "end": v(9.53, -21) * mm});
            skLineSegment(sketch, "E826", {"start": v(9.53, -21) * mm, "end": v(10.63, -23.65) * mm});
            skLineSegment(sketch, "E827", {"start": v(10.63, -23.65) * mm, "end": v(11, -26.5) * mm});
            skLineSegment(sketch, "E828", {"start": v(11, -26.5) * mm, "end": v(10.63, -29.35) * mm});
            skLineSegment(sketch, "E829", {"start": v(10.63, -29.35) * mm, "end": v(9.53, -32) * mm});
            skLineSegment(sketch, "E830", {"start": v(9.53, -32) * mm, "end": v(7.78, -34.28) * mm});
            skLineSegment(sketch, "E831", {"start": v(7.78, -34.28) * mm, "end": v(5.5, -36.03) * mm});
            skLineSegment(sketch, "E832", {"start": v(5.5, -36.03) * mm, "end": v(2.85, -37.13) * mm});
            skLineSegment(sketch, "E833", {"start": v(2.85, -37.13) * mm, "end": v(0, -37.5) * mm});
            skLineSegment(sketch, "E834", {"start": v(0, -37.5) * mm, "end": v(-2.85, -37.13) * mm});
            skLineSegment(sketch, "E835", {"start": v(-2.85, -37.13) * mm, "end": v(-5.5, -36.03) * mm});
            skLineSegment(sketch, "E836", {"start": v(-5.5, -36.03) * mm, "end": v(-7.78, -34.28) * mm});
            skLineSegment(sketch, "E837", {"start": v(-7.78, -34.28) * mm, "end": v(-9.53, -32) * mm});
            skLineSegment(sketch, "E838", {"start": v(-9.53, -32) * mm, "end": v(-10.63, -29.35) * mm});
            skLineSegment(sketch, "E839", {"start": v(-10.63, -29.35) * mm, "end": v(-11, -26.5) * mm});
            skLineSegment(sketch, "E840", {"start": v(-11, -26.5) * mm, "end": v(-10.63, -23.65) * mm});
            skLineSegment(sketch, "E841", {"start": v(-10.63, -23.65) * mm, "end": v(-9.53, -21) * mm});
            skLineSegment(sketch, "E842", {"start": v(-9.53, -21) * mm, "end": v(-7.78, -18.72) * mm});
            skLineSegment(sketch, "E843", {"start": v(-7.78, -18.72) * mm, "end": v(-5.5, -16.97) * mm});
            skLineSegment(sketch, "E844", {"start": v(-5.5, -16.97) * mm, "end": v(-2.85, -15.87) * mm});
            skLineSegment(sketch, "E845", {"start": v(-41.05, 37.89) * mm, "end": v(-41, 37.5) * mm});
            skLineSegment(sketch, "E846", {"start": v(-41, 37.5) * mm, "end": v(-41.05, 37.11) * mm});
            skLineSegment(sketch, "E847", {"start": v(-41.05, 37.11) * mm, "end": v(-41.2, 36.75) * mm});
            skLineSegment(sketch, "E848", {"start": v(-41.2, 36.75) * mm, "end": v(-41.44, 36.44) * mm});
            skLineSegment(sketch, "E849", {"start": v(-41.44, 36.44) * mm, "end": v(-41.75, 36.2) * mm});
            skLineSegment(sketch, "E850", {"start": v(-41.75, 36.2) * mm, "end": v(-42.11, 36.05) * mm});
            skLineSegment(sketch, "E851", {"start": v(-42.11, 36.05) * mm, "end": v(-42.5, 36) * mm});
            skLineSegment(sketch, "E852", {"start": v(-42.5, 36) * mm, "end": v(-42.89, 36.05) * mm});
            skLineSegment(sketch, "E853", {"start": v(-42.89, 36.05) * mm, "end": v(-43.25, 36.2) * mm});
            skLineSegment(sketch, "E854", {"start": v(-43.25, 36.2) * mm, "end": v(-43.56, 36.44) * mm});
            skLineSegment(sketch, "E855", {"start": v(-43.56, 36.44) * mm, "end": v(-43.8, 36.75) * mm});
            skLineSegment(sketch, "E856", {"start": v(-43.8, 36.75) * mm, "end": v(-43.95, 37.11) * mm});
            skLineSegment(sketch, "E857", {"start": v(-43.95, 37.11) * mm, "end": v(-44, 37.5) * mm});
            skLineSegment(sketch, "E858", {"start": v(-44, 37.5) * mm, "end": v(-43.95, 37.89) * mm});
            skLineSegment(sketch, "E859", {"start": v(-43.95, 37.89) * mm, "end": v(-43.8, 38.25) * mm});
            skLineSegment(sketch, "E860", {"start": v(-43.8, 38.25) * mm, "end": v(-43.56, 38.56) * mm});
            skLineSegment(sketch, "E861", {"start": v(-43.56, 38.56) * mm, "end": v(-43.25, 38.8) * mm});
            skLineSegment(sketch, "E862", {"start": v(-43.25, 38.8) * mm, "end": v(-42.89, 38.95) * mm});
            skLineSegment(sketch, "E863", {"start": v(-42.89, 38.95) * mm, "end": v(-42.5, 39) * mm});
            skLineSegment(sketch, "E864", {"start": v(-42.5, 39) * mm, "end": v(-42.11, 38.95) * mm});
            skLineSegment(sketch, "E865", {"start": v(-42.11, 38.95) * mm, "end": v(-41.75, 38.8) * mm});
            skLineSegment(sketch, "E866", {"start": v(-41.75, 38.8) * mm, "end": v(-41.44, 38.56) * mm});
            skLineSegment(sketch, "E867", {"start": v(-41.44, 38.56) * mm, "end": v(-41.2, 38.25) * mm});
            skLineSegment(sketch, "E868", {"start": v(-41.2, 38.25) * mm, "end": v(-41.05, 37.89) * mm});
            skLineSegment(sketch, "E869", {"start": v(-41.05, 27.11) * mm, "end": v(-41.2, 26.75) * mm});
            skLineSegment(sketch, "E870", {"start": v(-41.2, 26.75) * mm, "end": v(-41.44, 26.44) * mm});
            skLineSegment(sketch, "E871", {"start": v(-41.44, 26.44) * mm, "end": v(-41.75, 26.2) * mm});
            skLineSegment(sketch, "E872", {"start": v(-41.75, 26.2) * mm, "end": v(-42.11, 26.05) * mm});
            skLineSegment(sketch, "E873", {"start": v(-42.11, 26.05) * mm, "end": v(-42.5, 26) * mm});
            skLineSegment(sketch, "E874", {"start": v(-42.5, 26) * mm, "end": v(-42.89, 26.05) * mm});
            skLineSegment(sketch, "E875", {"start": v(-42.89, 26.05) * mm, "end": v(-43.25, 26.2) * mm});
            skLineSegment(sketch, "E876", {"start": v(-43.25, 26.2) * mm, "end": v(-43.56, 26.44) * mm});
            skLineSegment(sketch, "E877", {"start": v(-43.56, 26.44) * mm, "end": v(-43.8, 26.75) * mm});
            skLineSegment(sketch, "E878", {"start": v(-43.8, 26.75) * mm, "end": v(-43.95, 27.11) * mm});
            skLineSegment(sketch, "E879", {"start": v(-43.95, 27.11) * mm, "end": v(-44, 27.5) * mm});
            skLineSegment(sketch, "E880", {"start": v(-44, 27.5) * mm, "end": v(-43.95, 27.89) * mm});
            skLineSegment(sketch, "E881", {"start": v(-43.95, 27.89) * mm, "end": v(-43.8, 28.25) * mm});
            skLineSegment(sketch, "E882", {"start": v(-43.8, 28.25) * mm, "end": v(-43.56, 28.56) * mm});
            skLineSegment(sketch, "E883", {"start": v(-43.56, 28.56) * mm, "end": v(-43.25, 28.8) * mm});
            skLineSegment(sketch, "E884", {"start": v(-43.25, 28.8) * mm, "end": v(-42.89, 28.95) * mm});
            skLineSegment(sketch, "E885", {"start": v(-42.89, 28.95) * mm, "end": v(-42.5, 29) * mm});
            skLineSegment(sketch, "E886", {"start": v(-42.5, 29) * mm, "end": v(-42.11, 28.95) * mm});
            skLineSegment(sketch, "E887", {"start": v(-42.11, 28.95) * mm, "end": v(-41.75, 28.8) * mm});
            skLineSegment(sketch, "E888", {"start": v(-41.75, 28.8) * mm, "end": v(-41.44, 28.56) * mm});
            skLineSegment(sketch, "E889", {"start": v(-41.44, 28.56) * mm, "end": v(-41.2, 28.25) * mm});
            skLineSegment(sketch, "E890", {"start": v(-41.2, 28.25) * mm, "end": v(-41.05, 27.89) * mm});
            skLineSegment(sketch, "E891", {"start": v(-41.05, 27.89) * mm, "end": v(-41, 27.5) * mm});
            skLineSegment(sketch, "E892", {"start": v(-41, 27.5) * mm, "end": v(-41.05, 27.11) * mm});
            skLineSegment(sketch, "E893", {"start": v(43.95, 37.11) * mm, "end": v(43.8, 36.75) * mm});
            skLineSegment(sketch, "E894", {"start": v(43.8, 36.75) * mm, "end": v(43.56, 36.44) * mm});
            skLineSegment(sketch, "E895", {"start": v(43.56, 36.44) * mm, "end": v(43.25, 36.2) * mm});
            skLineSegment(sketch, "E896", {"start": v(43.25, 36.2) * mm, "end": v(42.89, 36.05) * mm});
            skLineSegment(sketch, "E897", {"start": v(42.89, 36.05) * mm, "end": v(42.5, 36) * mm});
            skLineSegment(sketch, "E898", {"start": v(42.5, 36) * mm, "end": v(42.11, 36.05) * mm});
            skLineSegment(sketch, "E899", {"start": v(42.11, 36.05) * mm, "end": v(41.75, 36.2) * mm});
            skLineSegment(sketch, "E900", {"start": v(41.75, 36.2) * mm, "end": v(41.44, 36.44) * mm});
            skLineSegment(sketch, "E901", {"start": v(41.44, 36.44) * mm, "end": v(41.2, 36.75) * mm});
            skLineSegment(sketch, "E902", {"start": v(41.2, 36.75) * mm, "end": v(41.05, 37.11) * mm});
            skLineSegment(sketch, "E903", {"start": v(41.05, 37.11) * mm, "end": v(41, 37.5) * mm});
            skLineSegment(sketch, "E904", {"start": v(41, 37.5) * mm, "end": v(41.05, 37.89) * mm});
            skLineSegment(sketch, "E905", {"start": v(41.05, 37.89) * mm, "end": v(41.2, 38.25) * mm});
            skLineSegment(sketch, "E906", {"start": v(41.2, 38.25) * mm, "end": v(41.44, 38.56) * mm});
            skLineSegment(sketch, "E907", {"start": v(41.44, 38.56) * mm, "end": v(41.75, 38.8) * mm});
            skLineSegment(sketch, "E908", {"start": v(41.75, 38.8) * mm, "end": v(42.11, 38.95) * mm});
            skLineSegment(sketch, "E909", {"start": v(42.11, 38.95) * mm, "end": v(42.5, 39) * mm});
            skLineSegment(sketch, "E910", {"start": v(42.5, 39) * mm, "end": v(42.89, 38.95) * mm});
            skLineSegment(sketch, "E911", {"start": v(42.89, 38.95) * mm, "end": v(43.25, 38.8) * mm});
            skLineSegment(sketch, "E912", {"start": v(43.25, 38.8) * mm, "end": v(43.56, 38.56) * mm});
            skLineSegment(sketch, "E913", {"start": v(43.56, 38.56) * mm, "end": v(43.8, 38.25) * mm});
            skLineSegment(sketch, "E914", {"start": v(43.8, 38.25) * mm, "end": v(43.95, 37.89) * mm});
            skLineSegment(sketch, "E915", {"start": v(43.95, 37.89) * mm, "end": v(44, 37.5) * mm});
            skLineSegment(sketch, "E916", {"start": v(44, 37.5) * mm, "end": v(43.95, 37.11) * mm});
            skLineSegment(sketch, "E917", {"start": v(43.8, 26.75) * mm, "end": v(43.56, 26.44) * mm});
            skLineSegment(sketch, "E918", {"start": v(43.56, 26.44) * mm, "end": v(43.25, 26.2) * mm});
            skLineSegment(sketch, "E919", {"start": v(43.25, 26.2) * mm, "end": v(42.89, 26.05) * mm});
            skLineSegment(sketch, "E920", {"start": v(42.89, 26.05) * mm, "end": v(42.5, 26) * mm});
            skLineSegment(sketch, "E921", {"start": v(42.5, 26) * mm, "end": v(42.11, 26.05) * mm});
            skLineSegment(sketch, "E922", {"start": v(42.11, 26.05) * mm, "end": v(41.75, 26.2) * mm});
            skLineSegment(sketch, "E923", {"start": v(41.75, 26.2) * mm, "end": v(41.44, 26.44) * mm});
            skLineSegment(sketch, "E924", {"start": v(41.44, 26.44) * mm, "end": v(41.2, 26.75) * mm});
            skLineSegment(sketch, "E925", {"start": v(41.2, 26.75) * mm, "end": v(41.05, 27.11) * mm});
            skLineSegment(sketch, "E926", {"start": v(41.05, 27.11) * mm, "end": v(41, 27.5) * mm});
            skLineSegment(sketch, "E927", {"start": v(41, 27.5) * mm, "end": v(41.05, 27.89) * mm});
            skLineSegment(sketch, "E928", {"start": v(41.05, 27.89) * mm, "end": v(41.2, 28.25) * mm});
            skLineSegment(sketch, "E929", {"start": v(41.2, 28.25) * mm, "end": v(41.44, 28.56) * mm});
            skLineSegment(sketch, "E930", {"start": v(41.44, 28.56) * mm, "end": v(41.75, 28.8) * mm});
            skLineSegment(sketch, "E931", {"start": v(41.75, 28.8) * mm, "end": v(42.11, 28.95) * mm});
            skLineSegment(sketch, "E932", {"start": v(42.11, 28.95) * mm, "end": v(42.5, 29) * mm});
            skLineSegment(sketch, "E933", {"start": v(42.5, 29) * mm, "end": v(42.89, 28.95) * mm});
            skLineSegment(sketch, "E934", {"start": v(42.89, 28.95) * mm, "end": v(43.25, 28.8) * mm});
            skLineSegment(sketch, "E935", {"start": v(43.25, 28.8) * mm, "end": v(43.56, 28.56) * mm});
            skLineSegment(sketch, "E936", {"start": v(43.56, 28.56) * mm, "end": v(43.8, 28.25) * mm});
            skLineSegment(sketch, "E937", {"start": v(43.8, 28.25) * mm, "end": v(43.95, 27.89) * mm});
            skLineSegment(sketch, "E938", {"start": v(43.95, 27.89) * mm, "end": v(44, 27.5) * mm});
            skLineSegment(sketch, "E939", {"start": v(44, 27.5) * mm, "end": v(43.95, 27.11) * mm});
            skLineSegment(sketch, "E940", {"start": v(43.95, 27.11) * mm, "end": v(43.8, 26.75) * mm});
            skLineSegment(sketch, "E941", {"start": v(38.55, 10.39) * mm, "end": v(38.7, 10.75) * mm});
            skLineSegment(sketch, "E942", {"start": v(38.7, 10.75) * mm, "end": v(38.94, 11.06) * mm});
            skLineSegment(sketch, "E943", {"start": v(38.94, 11.06) * mm, "end": v(39.25, 11.3) * mm});
            skLineSegment(sketch, "E944", {"start": v(39.25, 11.3) * mm, "end": v(39.61, 11.45) * mm});
            skLineSegment(sketch, "E945", {"start": v(39.61, 11.45) * mm, "end": v(40, 11.5) * mm});
            skLineSegment(sketch, "E946", {"start": v(40, 11.5) * mm, "end": v(40.39, 11.45) * mm});
            skLineSegment(sketch, "E947", {"start": v(40.39, 11.45) * mm, "end": v(40.75, 11.3) * mm});
            skLineSegment(sketch, "E948", {"start": v(40.75, 11.3) * mm, "end": v(41.06, 11.06) * mm});
            skLineSegment(sketch, "E949", {"start": v(41.06, 11.06) * mm, "end": v(41.3, 10.75) * mm});
            skLineSegment(sketch, "E950", {"start": v(41.3, 10.75) * mm, "end": v(41.45, 10.39) * mm});
            skLineSegment(sketch, "E951", {"start": v(41.45, 10.39) * mm, "end": v(41.5, 10) * mm});
            skLineSegment(sketch, "E952", {"start": v(41.5, 10) * mm, "end": v(41.45, 9.61) * mm});
            skLineSegment(sketch, "E953", {"start": v(41.45, 9.61) * mm, "end": v(41.3, 9.25) * mm});
            skLineSegment(sketch, "E954", {"start": v(41.3, 9.25) * mm, "end": v(41.06, 8.94) * mm});
            skLineSegment(sketch, "E955", {"start": v(41.06, 8.94) * mm, "end": v(40.75, 8.7) * mm});
            skLineSegment(sketch, "E956", {"start": v(40.75, 8.7) * mm, "end": v(40.39, 8.55) * mm});
            skLineSegment(sketch, "E957", {"start": v(40.39, 8.55) * mm, "end": v(40, 8.5) * mm});
            skLineSegment(sketch, "E958", {"start": v(40, 8.5) * mm, "end": v(39.61, 8.55) * mm});
            skLineSegment(sketch, "E959", {"start": v(39.61, 8.55) * mm, "end": v(39.25, 8.7) * mm});
            skLineSegment(sketch, "E960", {"start": v(39.25, 8.7) * mm, "end": v(38.94, 8.94) * mm});
            skLineSegment(sketch, "E961", {"start": v(38.94, 8.94) * mm, "end": v(38.7, 9.25) * mm});
            skLineSegment(sketch, "E962", {"start": v(38.7, 9.25) * mm, "end": v(38.55, 9.61) * mm});
            skLineSegment(sketch, "E963", {"start": v(38.55, 9.61) * mm, "end": v(38.5, 10) * mm});
            skLineSegment(sketch, "E964", {"start": v(38.5, 10) * mm, "end": v(38.55, 10.39) * mm});
            skLineSegment(sketch, "E965", {"start": v(15.39, 11.45) * mm, "end": v(15.75, 11.3) * mm});
            skLineSegment(sketch, "E966", {"start": v(15.75, 11.3) * mm, "end": v(16.06, 11.06) * mm});
            skLineSegment(sketch, "E967", {"start": v(16.06, 11.06) * mm, "end": v(16.3, 10.75) * mm});
            skLineSegment(sketch, "E968", {"start": v(16.3, 10.75) * mm, "end": v(16.45, 10.39) * mm});
            skLineSegment(sketch, "E969", {"start": v(16.45, 10.39) * mm, "end": v(16.5, 10) * mm});
            skLineSegment(sketch, "E970", {"start": v(16.5, 10) * mm, "end": v(16.45, 9.61) * mm});
            skLineSegment(sketch, "E971", {"start": v(16.45, 9.61) * mm, "end": v(16.3, 9.25) * mm});
            skLineSegment(sketch, "E972", {"start": v(16.3, 9.25) * mm, "end": v(16.06, 8.94) * mm});
            skLineSegment(sketch, "E973", {"start": v(16.06, 8.94) * mm, "end": v(15.75, 8.7) * mm});
            skLineSegment(sketch, "E974", {"start": v(15.75, 8.7) * mm, "end": v(15.39, 8.55) * mm});
            skLineSegment(sketch, "E975", {"start": v(15.39, 8.55) * mm, "end": v(15, 8.5) * mm});
            skLineSegment(sketch, "E976", {"start": v(15, 8.5) * mm, "end": v(14.61, 8.55) * mm});
            skLineSegment(sketch, "E977", {"start": v(14.61, 8.55) * mm, "end": v(14.25, 8.7) * mm});
            skLineSegment(sketch, "E978", {"start": v(14.25, 8.7) * mm, "end": v(13.94, 8.94) * mm});
            skLineSegment(sketch, "E979", {"start": v(13.94, 8.94) * mm, "end": v(13.7, 9.25) * mm});
            skLineSegment(sketch, "E980", {"start": v(13.7, 9.25) * mm, "end": v(13.55, 9.61) * mm});
            skLineSegment(sketch, "E981", {"start": v(13.55, 9.61) * mm, "end": v(13.5, 10) * mm});
            skLineSegment(sketch, "E982", {"start": v(13.5, 10) * mm, "end": v(13.55, 10.39) * mm});
            skLineSegment(sketch, "E983", {"start": v(13.55, 10.39) * mm, "end": v(13.7, 10.75) * mm});
            skLineSegment(sketch, "E984", {"start": v(13.7, 10.75) * mm, "end": v(13.94, 11.06) * mm});
            skLineSegment(sketch, "E985", {"start": v(13.94, 11.06) * mm, "end": v(14.25, 11.3) * mm});
            skLineSegment(sketch, "E986", {"start": v(14.25, 11.3) * mm, "end": v(14.61, 11.45) * mm});
            skLineSegment(sketch, "E987", {"start": v(14.61, 11.45) * mm, "end": v(15, 11.5) * mm});
            skLineSegment(sketch, "E988", {"start": v(15, 11.5) * mm, "end": v(15.39, 11.45) * mm});
            skLineSegment(sketch, "E989", {"start": v(-15, 8.5) * mm, "end": v(-15.39, 8.55) * mm});
            skLineSegment(sketch, "E990", {"start": v(-15.39, 8.55) * mm, "end": v(-15.75, 8.7) * mm});
            skLineSegment(sketch, "E991", {"start": v(-15.75, 8.7) * mm, "end": v(-16.06, 8.94) * mm});
            skLineSegment(sketch, "E992", {"start": v(-16.06, 8.94) * mm, "end": v(-16.3, 9.25) * mm});
            skLineSegment(sketch, "E993", {"start": v(-16.3, 9.25) * mm, "end": v(-16.45, 9.61) * mm});
            skLineSegment(sketch, "E994", {"start": v(-16.45, 9.61) * mm, "end": v(-16.5, 10) * mm});
            skLineSegment(sketch, "E995", {"start": v(-16.5, 10) * mm, "end": v(-16.45, 10.39) * mm});
            skLineSegment(sketch, "E996", {"start": v(-16.45, 10.39) * mm, "end": v(-16.3, 10.75) * mm});
            skLineSegment(sketch, "E997", {"start": v(-16.3, 10.75) * mm, "end": v(-16.06, 11.06) * mm});
            skLineSegment(sketch, "E998", {"start": v(-16.06, 11.06) * mm, "end": v(-15.75, 11.3) * mm});
            skLineSegment(sketch, "E999", {"start": v(-15.75, 11.3) * mm, "end": v(-15.39, 11.45) * mm});
            skLineSegment(sketch, "E1000", {"start": v(-15.39, 11.45) * mm, "end": v(-15, 11.5) * mm});
            skLineSegment(sketch, "E1001", {"start": v(-15, 11.5) * mm, "end": v(-14.61, 11.45) * mm});
            skLineSegment(sketch, "E1002", {"start": v(-14.61, 11.45) * mm, "end": v(-14.25, 11.3) * mm});
            skLineSegment(sketch, "E1003", {"start": v(-14.25, 11.3) * mm, "end": v(-13.94, 11.06) * mm});
            skLineSegment(sketch, "E1004", {"start": v(-13.94, 11.06) * mm, "end": v(-13.7, 10.75) * mm});
            skLineSegment(sketch, "E1005", {"start": v(-13.7, 10.75) * mm, "end": v(-13.55, 10.39) * mm});
            skLineSegment(sketch, "E1006", {"start": v(-13.55, 10.39) * mm, "end": v(-13.5, 10) * mm});
            skLineSegment(sketch, "E1007", {"start": v(-13.5, 10) * mm, "end": v(-13.55, 9.61) * mm});
            skLineSegment(sketch, "E1008", {"start": v(-13.55, 9.61) * mm, "end": v(-13.7, 9.25) * mm});
            skLineSegment(sketch, "E1009", {"start": v(-13.7, 9.25) * mm, "end": v(-13.94, 8.94) * mm});
            skLineSegment(sketch, "E1010", {"start": v(-13.94, 8.94) * mm, "end": v(-14.25, 8.7) * mm});
            skLineSegment(sketch, "E1011", {"start": v(-14.25, 8.7) * mm, "end": v(-14.61, 8.55) * mm});
            skLineSegment(sketch, "E1012", {"start": v(-14.61, 8.55) * mm, "end": v(-15, 8.5) * mm});
            skLineSegment(sketch, "E1013", {"start": v(-39.25, 8.7) * mm, "end": v(-39.61, 8.55) * mm});
            skLineSegment(sketch, "E1014", {"start": v(-39.61, 8.55) * mm, "end": v(-40, 8.5) * mm});
            skLineSegment(sketch, "E1015", {"start": v(-40, 8.5) * mm, "end": v(-40.39, 8.55) * mm});
            skLineSegment(sketch, "E1016", {"start": v(-40.39, 8.55) * mm, "end": v(-40.75, 8.7) * mm});
            skLineSegment(sketch, "E1017", {"start": v(-40.75, 8.7) * mm, "end": v(-41.06, 8.94) * mm});
            skLineSegment(sketch, "E1018", {"start": v(-41.06, 8.94) * mm, "end": v(-41.3, 9.25) * mm});
            skLineSegment(sketch, "E1019", {"start": v(-41.3, 9.25) * mm, "end": v(-41.45, 9.61) * mm});
            skLineSegment(sketch, "E1020", {"start": v(-41.45, 9.61) * mm, "end": v(-41.5, 10) * mm});
            skLineSegment(sketch, "E1021", {"start": v(-41.5, 10) * mm, "end": v(-41.45, 10.39) * mm});
            skLineSegment(sketch, "E1022", {"start": v(-41.45, 10.39) * mm, "end": v(-41.3, 10.75) * mm});
            skLineSegment(sketch, "E1023", {"start": v(-41.3, 10.75) * mm, "end": v(-41.06, 11.06) * mm});
            skLineSegment(sketch, "E1024", {"start": v(-41.06, 11.06) * mm, "end": v(-40.75, 11.3) * mm});
            skLineSegment(sketch, "E1025", {"start": v(-40.75, 11.3) * mm, "end": v(-40.39, 11.45) * mm});
            skLineSegment(sketch, "E1026", {"start": v(-40.39, 11.45) * mm, "end": v(-40, 11.5) * mm});
            skLineSegment(sketch, "E1027", {"start": v(-40, 11.5) * mm, "end": v(-39.61, 11.45) * mm});
            skLineSegment(sketch, "E1028", {"start": v(-39.61, 11.45) * mm, "end": v(-39.25, 11.3) * mm});
            skLineSegment(sketch, "E1029", {"start": v(-39.25, 11.3) * mm, "end": v(-38.94, 11.06) * mm});
            skLineSegment(sketch, "E1030", {"start": v(-38.94, 11.06) * mm, "end": v(-38.7, 10.75) * mm});
            skLineSegment(sketch, "E1031", {"start": v(-38.7, 10.75) * mm, "end": v(-38.55, 10.39) * mm});
            skLineSegment(sketch, "E1032", {"start": v(-38.55, 10.39) * mm, "end": v(-38.5, 10) * mm});
            skLineSegment(sketch, "E1033", {"start": v(-38.5, 10) * mm, "end": v(-38.55, 9.61) * mm});
            skLineSegment(sketch, "E1034", {"start": v(-38.55, 9.61) * mm, "end": v(-38.7, 9.25) * mm});
            skLineSegment(sketch, "E1035", {"start": v(-38.7, 9.25) * mm, "end": v(-38.94, 8.94) * mm});
            skLineSegment(sketch, "E1036", {"start": v(-38.94, 8.94) * mm, "end": v(-39.25, 8.7) * mm});
            skLineSegment(sketch, "E1037", {"start": v(0, -15.5) * mm, "end": v(-2.85, -15.87) * mm});
            skLineSegment(sketch, "E1038", {"start": v(-2.85, -15.87) * mm, "end": v(-5.5, -16.97) * mm});
            skLineSegment(sketch, "E1039", {"start": v(-5.5, -16.97) * mm, "end": v(-7.78, -18.72) * mm});
            skLineSegment(sketch, "E1040", {"start": v(-7.78, -18.72) * mm, "end": v(-9.53, -21) * mm});
            skLineSegment(sketch, "E1041", {"start": v(-9.53, -21) * mm, "end": v(-10.63, -23.65) * mm});
            skLineSegment(sketch, "E1042", {"start": v(-10.63, -23.65) * mm, "end": v(-11, -26.5) * mm});
            skLineSegment(sketch, "E1043", {"start": v(-11, -26.5) * mm, "end": v(-10.63, -29.35) * mm});
            skLineSegment(sketch, "E1044", {"start": v(-10.63, -29.35) * mm, "end": v(-9.53, -32) * mm});
            skLineSegment(sketch, "E1045", {"start": v(-9.53, -32) * mm, "end": v(-7.78, -34.28) * mm});
            skLineSegment(sketch, "E1046", {"start": v(-7.78, -34.28) * mm, "end": v(-5.5, -36.03) * mm});
            skLineSegment(sketch, "E1047", {"start": v(-5.5, -36.03) * mm, "end": v(-2.85, -37.13) * mm});
            skLineSegment(sketch, "E1048", {"start": v(-2.85, -37.13) * mm, "end": v(0, -37.5) * mm});
            skLineSegment(sketch, "E1049", {"start": v(0, -37.5) * mm, "end": v(2.85, -37.13) * mm});
            skLineSegment(sketch, "E1050", {"start": v(2.85, -37.13) * mm, "end": v(5.5, -36.03) * mm});
            skLineSegment(sketch, "E1051", {"start": v(5.5, -36.03) * mm, "end": v(7.78, -34.28) * mm});
            skLineSegment(sketch, "E1052", {"start": v(7.78, -34.28) * mm, "end": v(9.53, -32) * mm});
            skLineSegment(sketch, "E1053", {"start": v(9.53, -32) * mm, "end": v(10.63, -29.35) * mm});
            skLineSegment(sketch, "E1054", {"start": v(10.63, -29.35) * mm, "end": v(11, -26.5) * mm});
            skLineSegment(sketch, "E1055", {"start": v(11, -26.5) * mm, "end": v(10.63, -23.65) * mm});
            skLineSegment(sketch, "E1056", {"start": v(10.63, -23.65) * mm, "end": v(9.53, -21) * mm});
            skLineSegment(sketch, "E1057", {"start": v(9.53, -21) * mm, "end": v(7.78, -18.72) * mm});
            skLineSegment(sketch, "E1058", {"start": v(7.78, -18.72) * mm, "end": v(5.5, -16.97) * mm});
            skLineSegment(sketch, "E1059", {"start": v(5.5, -16.97) * mm, "end": v(2.85, -15.87) * mm});
            skLineSegment(sketch, "E1060", {"start": v(2.85, -15.87) * mm, "end": v(0, -15.5) * mm});
            skLineSegment(sketch, "E1061", {"start": v(-3.46, -24.5) * mm, "end": v(-2.83, -23.67) * mm});
            skLineSegment(sketch, "E1062", {"start": v(-2.83, -23.67) * mm, "end": v(-2, -23.04) * mm});
            skLineSegment(sketch, "E1063", {"start": v(-2, -23.04) * mm, "end": v(-1.04, -22.64) * mm});
            skLineSegment(sketch, "E1064", {"start": v(-1.04, -22.64) * mm, "end": v(0, -22.5) * mm});
            skLineSegment(sketch, "E1065", {"start": v(0, -22.5) * mm, "end": v(1.04, -22.64) * mm});
            skLineSegment(sketch, "E1066", {"start": v(1.04, -22.64) * mm, "end": v(2, -23.04) * mm});
            skLineSegment(sketch, "E1067", {"start": v(2, -23.04) * mm, "end": v(2.83, -23.67) * mm});
            skLineSegment(sketch, "E1068", {"start": v(2.83, -23.67) * mm, "end": v(3.46, -24.5) * mm});
            skLineSegment(sketch, "E1069", {"start": v(3.46, -24.5) * mm, "end": v(3.86, -25.46) * mm});
            skLineSegment(sketch, "E1070", {"start": v(3.86, -25.46) * mm, "end": v(4, -26.5) * mm});
            skLineSegment(sketch, "E1071", {"start": v(4, -26.5) * mm, "end": v(3.86, -27.54) * mm});
            skLineSegment(sketch, "E1072", {"start": v(3.86, -27.54) * mm, "end": v(3.46, -28.5) * mm});
            skLineSegment(sketch, "E1073", {"start": v(3.46, -28.5) * mm, "end": v(2.83, -29.33) * mm});
            skLineSegment(sketch, "E1074", {"start": v(2.83, -29.33) * mm, "end": v(2, -29.96) * mm});
            skLineSegment(sketch, "E1075", {"start": v(2, -29.96) * mm, "end": v(1.04, -30.36) * mm});
            skLineSegment(sketch, "E1076", {"start": v(1.04, -30.36) * mm, "end": v(0, -30.5) * mm});
            skLineSegment(sketch, "E1077", {"start": v(0, -30.5) * mm, "end": v(-1.04, -30.36) * mm});
            skLineSegment(sketch, "E1078", {"start": v(-1.04, -30.36) * mm, "end": v(-2, -29.96) * mm});
            skLineSegment(sketch, "E1079", {"start": v(-2, -29.96) * mm, "end": v(-2.83, -29.33) * mm});
            skLineSegment(sketch, "E1080", {"start": v(-2.83, -29.33) * mm, "end": v(-3.46, -28.5) * mm});
            skLineSegment(sketch, "E1081", {"start": v(-3.46, -28.5) * mm, "end": v(-3.86, -27.54) * mm});
            skLineSegment(sketch, "E1082", {"start": v(-3.86, -27.54) * mm, "end": v(-4, -26.5) * mm});
            skLineSegment(sketch, "E1083", {"start": v(-4, -26.5) * mm, "end": v(-3.86, -25.46) * mm});
            skLineSegment(sketch, "E1084", {"start": v(-3.86, -25.46) * mm, "end": v(-3.46, -24.5) * mm});
            skCircle(sketch, "E1085", {"center": v(-35, -26.5) * mm, "radius": 4 * mm});
            skCircle(sketch, "E1086", {"center": v(35, -26.5) * mm, "radius": 4 * mm});
            skSolve(sketch);
        }
        {
            var Q0;
            Q0=makeQuery(id+"F0.imprint","IMPRINT",FACE,{"disambiguationData":[TD([[makeQuery(id+"F0.imprint","IMPRINT",EDGE,{"derivedFrom":sQuery(id+"F0.wireOp",EDGE,"E0")}),-1.0]])]});
            extrude(context, id + "F9", {"entities" : qUnion([Q0]), "depth" : 15 * mm});
        }
        {
            var Q0;
            Q0=makeQuery(id+"F2.imprint","IMPRINT",FACE,{"disambiguationData":[TD([[makeQuery(id+"F2.imprint","IMPRINT",EDGE,{"derivedFrom":sQuery(id+"F2.wireOp",EDGE,"E534")}),1.0]])]});
            extrude(context, id + "F10", {"entities" : qUnion([Q0]), "depth" : 15 * mm});
        }
        {
            var Q0;
            Q0=makeQuery(id+"F4.imprint","IMPRINT",FACE,{"disambiguationData":[TD([[makeQuery(id+"F4.imprint","IMPRINT",EDGE,{"derivedFrom":sQuery(id+"F4.wireOp",EDGE,"E778")}),-1.0]])]});
            extrude(context, id + "F11", {"entities" : qUnion([Q0]), "depth" : 15 * mm});
        }
        {
            var Q0;
            Q0 = qSketchRegion(id + "F6", true);
            extrude(context, id + "F12", {"entities" : qUnion([Q0]), "depth" : 15 * mm});
        }
        {
            var Q0;
            Q0 = qSketchRegion(id + "F8", true);
            extrude(context, id + "F13", {"entities" : qUnion([Q0]), "depth" : 15 * mm});
        }
        {
            var Q0;
            Q0=makeQuery(id+"F13.opExtrude","CAP_FACE",FACE,{"disambiguationData":[OSD([sQuery(id+"F8.wireOp",EDGE,"E817"),sQuery(id+"F8.wireOp",EDGE,"E818"),sQuery(id+"F8.wireOp",EDGE,"E819"),sQuery(id+"F8.wireOp",EDGE,"E820"),sQuery(id+"F8.wireOp",EDGE,"E845"),sQuery(id+"F8.wireOp",EDGE,"E846"),sQuery(id+"F8.wireOp",EDGE,"E847"),sQuery(id+"F8.wireOp",EDGE,"E848"),sQuery(id+"F8.wireOp",EDGE,"E849"),sQuery(id+"F8.wireOp",EDGE,"E850"),sQuery(id+"F8.wireOp",EDGE,"E851"),sQuery(id+"F8.wireOp",EDGE,"E852"),sQuery(id+"F8.wireOp",EDGE,"E853"),sQuery(id+"F8.wireOp",EDGE,"E854"),sQuery(id+"F8.wireOp",EDGE,"E855"),sQuery(id+"F8.wireOp",EDGE,"E856"),sQuery(id+"F8.wireOp",EDGE,"E857"),sQuery(id+"F8.wireOp",EDGE,"E858"),sQuery(id+"F8.wireOp",EDGE,"E859"),sQuery(id+"F8.wireOp",EDGE,"E860"),sQuery(id+"F8.wireOp",EDGE,"E861"),sQuery(id+"F8.wireOp",EDGE,"E862"),sQuery(id+"F8.wireOp",EDGE,"E863"),sQuery(id+"F8.wireOp",EDGE,"E864"),sQuery(id+"F8.wireOp",EDGE,"E865"),sQuery(id+"F8.wireOp",EDGE,"E866"),sQuery(id+"F8.wireOp",EDGE,"E867"),sQuery(id+"F8.wireOp",EDGE,"E868"),sQuery(id+"F8.wireOp",EDGE,"E869"),sQuery(id+"F8.wireOp",EDGE,"E870"),sQuery(id+"F8.wireOp",EDGE,"E871"),sQuery(id+"F8.wireOp",EDGE,"E872"),sQuery(id+"F8.wireOp",EDGE,"E873"),sQuery(id+"F8.wireOp",EDGE,"E874"),sQuery(id+"F8.wireOp",EDGE,"E875"),sQuery(id+"F8.wireOp",EDGE,"E876"),sQuery(id+"F8.wireOp",EDGE,"E877"),sQuery(id+"F8.wireOp",EDGE,"E878"),sQuery(id+"F8.wireOp",EDGE,"E879"),sQuery(id+"F8.wireOp",EDGE,"E880"),sQuery(id+"F8.wireOp",EDGE,"E881"),sQuery(id+"F8.wireOp",EDGE,"E882"),sQuery(id+"F8.wireOp",EDGE,"E883"),sQuery(id+"F8.wireOp",EDGE,"E884"),sQuery(id+"F8.wireOp",EDGE,"E885"),sQuery(id+"F8.wireOp",EDGE,"E886"),sQuery(id+"F8.wireOp",EDGE,"E887"),sQuery(id+"F8.wireOp",EDGE,"E888"),sQuery(id+"F8.wireOp",EDGE,"E889"),sQuery(id+"F8.wireOp",EDGE,"E890"),sQuery(id+"F8.wireOp",EDGE,"E891"),sQuery(id+"F8.wireOp",EDGE,"E892"),sQuery(id+"F8.wireOp",EDGE,"E893"),sQuery(id+"F8.wireOp",EDGE,"E894"),sQuery(id+"F8.wireOp",EDGE,"E895"),sQuery(id+"F8.wireOp",EDGE,"E896"),sQuery(id+"F8.wireOp",EDGE,"E897"),sQuery(id+"F8.wireOp",EDGE,"E898"),sQuery(id+"F8.wireOp",EDGE,"E899"),sQuery(id+"F8.wireOp",EDGE,"E900"),sQuery(id+"F8.wireOp",EDGE,"E901"),sQuery(id+"F8.wireOp",EDGE,"E902"),sQuery(id+"F8.wireOp",EDGE,"E903"),sQuery(id+"F8.wireOp",EDGE,"E904"),sQuery(id+"F8.wireOp",EDGE,"E905"),sQuery(id+"F8.wireOp",EDGE,"E906"),sQuery(id+"F8.wireOp",EDGE,"E907"),sQuery(id+"F8.wireOp",EDGE,"E908"),sQuery(id+"F8.wireOp",EDGE,"E909"),sQuery(id+"F8.wireOp",EDGE,"E910"),sQuery(id+"F8.wireOp",EDGE,"E911"),sQuery(id+"F8.wireOp",EDGE,"E912"),sQuery(id+"F8.wireOp",EDGE,"E913"),sQuery(id+"F8.wireOp",EDGE,"E914"),sQuery(id+"F8.wireOp",EDGE,"E915"),sQuery(id+"F8.wireOp",EDGE,"E916"),sQuery(id+"F8.wireOp",EDGE,"E917"),sQuery(id+"F8.wireOp",EDGE,"E918"),sQuery(id+"F8.wireOp",EDGE,"E919"),sQuery(id+"F8.wireOp",EDGE,"E920"),sQuery(id+"F8.wireOp",EDGE,"E921"),sQuery(id+"F8.wireOp",EDGE,"E922"),sQuery(id+"F8.wireOp",EDGE,"E923"),sQuery(id+"F8.wireOp",EDGE,"E924"),sQuery(id+"F8.wireOp",EDGE,"E925"),sQuery(id+"F8.wireOp",EDGE,"E926"),sQuery(id+"F8.wireOp",EDGE,"E927"),sQuery(id+"F8.wireOp",EDGE,"E928"),sQuery(id+"F8.wireOp",EDGE,"E929"),sQuery(id+"F8.wireOp",EDGE,"E930"),sQuery(id+"F8.wireOp",EDGE,"E931"),sQuery(id+"F8.wireOp",EDGE,"E932"),sQuery(id+"F8.wireOp",EDGE,"E933"),sQuery(id+"F8.wireOp",EDGE,"E934"),sQuery(id+"F8.wireOp",EDGE,"E935"),sQuery(id+"F8.wireOp",EDGE,"E936"),sQuery(id+"F8.wireOp",EDGE,"E937"),sQuery(id+"F8.wireOp",EDGE,"E938"),sQuery(id+"F8.wireOp",EDGE,"E939"),sQuery(id+"F8.wireOp",EDGE,"E940"),sQuery(id+"F8.wireOp",EDGE,"E941"),sQuery(id+"F8.wireOp",EDGE,"E942"),sQuery(id+"F8.wireOp",EDGE,"E943"),sQuery(id+"F8.wireOp",EDGE,"E944"),sQuery(id+"F8.wireOp",EDGE,"E945"),sQuery(id+"F8.wireOp",EDGE,"E946"),sQuery(id+"F8.wireOp",EDGE,"E947"),sQuery(id+"F8.wireOp",EDGE,"E948"),sQuery(id+"F8.wireOp",EDGE,"E949"),sQuery(id+"F8.wireOp",EDGE,"E950"),sQuery(id+"F8.wireOp",EDGE,"E951"),sQuery(id+"F8.wireOp",EDGE,"E952"),sQuery(id+"F8.wireOp",EDGE,"E953"),sQuery(id+"F8.wireOp",EDGE,"E954"),sQuery(id+"F8.wireOp",EDGE,"E955"),sQuery(id+"F8.wireOp",EDGE,"E956"),sQuery(id+"F8.wireOp",EDGE,"E957"),sQuery(id+"F8.wireOp",EDGE,"E958"),sQuery(id+"F8.wireOp",EDGE,"E959"),sQuery(id+"F8.wireOp",EDGE,"E960"),sQuery(id+"F8.wireOp",EDGE,"E961"),sQuery(id+"F8.wireOp",EDGE,"E962"),sQuery(id+"F8.wireOp",EDGE,"E963"),sQuery(id+"F8.wireOp",EDGE,"E964"),sQuery(id+"F8.wireOp",EDGE,"E965"),sQuery(id+"F8.wireOp",EDGE,"E966"),sQuery(id+"F8.wireOp",EDGE,"E967"),sQuery(id+"F8.wireOp",EDGE,"E968"),sQuery(id+"F8.wireOp",EDGE,"E969"),sQuery(id+"F8.wireOp",EDGE,"E970"),sQuery(id+"F8.wireOp",EDGE,"E971"),sQuery(id+"F8.wireOp",EDGE,"E972"),sQuery(id+"F8.wireOp",EDGE,"E973"),sQuery(id+"F8.wireOp",EDGE,"E974"),sQuery(id+"F8.wireOp",EDGE,"E975"),sQuery(id+"F8.wireOp",EDGE,"E976"),sQuery(id+"F8.wireOp",EDGE,"E977"),sQuery(id+"F8.wireOp",EDGE,"E978"),sQuery(id+"F8.wireOp",EDGE,"E979"),sQuery(id+"F8.wireOp",EDGE,"E980"),sQuery(id+"F8.wireOp",EDGE,"E981"),sQuery(id+"F8.wireOp",EDGE,"E982"),sQuery(id+"F8.wireOp",EDGE,"E983"),sQuery(id+"F8.wireOp",EDGE,"E984"),sQuery(id+"F8.wireOp",EDGE,"E985"),sQuery(id+"F8.wireOp",EDGE,"E986"),sQuery(id+"F8.wireOp",EDGE,"E987"),sQuery(id+"F8.wireOp",EDGE,"E988"),sQuery(id+"F8.wireOp",EDGE,"E989"),sQuery(id+"F8.wireOp",EDGE,"E990"),sQuery(id+"F8.wireOp",EDGE,"E991"),sQuery(id+"F8.wireOp",EDGE,"E992"),sQuery(id+"F8.wireOp",EDGE,"E993"),sQuery(id+"F8.wireOp",EDGE,"E994"),sQuery(id+"F8.wireOp",EDGE,"E995"),sQuery(id+"F8.wireOp",EDGE,"E996"),sQuery(id+"F8.wireOp",EDGE,"E997"),sQuery(id+"F8.wireOp",EDGE,"E998"),sQuery(id+"F8.wireOp",EDGE,"E999"),sQuery(id+"F8.wireOp",EDGE,"E1000"),sQuery(id+"F8.wireOp",EDGE,"E1001"),sQuery(id+"F8.wireOp",EDGE,"E1002"),sQuery(id+"F8.wireOp",EDGE,"E1003"),sQuery(id+"F8.wireOp",EDGE,"E1004"),sQuery(id+"F8.wireOp",EDGE,"E1005"),sQuery(id+"F8.wireOp",EDGE,"E1006"),sQuery(id+"F8.wireOp",EDGE,"E1007"),sQuery(id+"F8.wireOp",EDGE,"E1008"),sQuery(id+"F8.wireOp",EDGE,"E1009"),sQuery(id+"F8.wireOp",EDGE,"E1010"),sQuery(id+"F8.wireOp",EDGE,"E1011"),sQuery(id+"F8.wireOp",EDGE,"E1012"),sQuery(id+"F8.wireOp",EDGE,"E1013"),sQuery(id+"F8.wireOp",EDGE,"E1014"),sQuery(id+"F8.wireOp",EDGE,"E1015"),sQuery(id+"F8.wireOp",EDGE,"E1016"),sQuery(id+"F8.wireOp",EDGE,"E1017"),sQuery(id+"F8.wireOp",EDGE,"E1018"),sQuery(id+"F8.wireOp",EDGE,"E1019"),sQuery(id+"F8.wireOp",EDGE,"E1020"),sQuery(id+"F8.wireOp",EDGE,"E1021"),sQuery(id+"F8.wireOp",EDGE,"E1022"),sQuery(id+"F8.wireOp",EDGE,"E1023"),sQuery(id+"F8.wireOp",EDGE,"E1024"),sQuery(id+"F8.wireOp",EDGE,"E1025"),sQuery(id+"F8.wireOp",EDGE,"E1026"),sQuery(id+"F8.wireOp",EDGE,"E1027"),sQuery(id+"F8.wireOp",EDGE,"E1028"),sQuery(id+"F8.wireOp",EDGE,"E1029"),sQuery(id+"F8.wireOp",EDGE,"E1030"),sQuery(id+"F8.wireOp",EDGE,"E1031"),sQuery(id+"F8.wireOp",EDGE,"E1032"),sQuery(id+"F8.wireOp",EDGE,"E1033"),sQuery(id+"F8.wireOp",EDGE,"E1034"),sQuery(id+"F8.wireOp",EDGE,"E1035"),sQuery(id+"F8.wireOp",EDGE,"E1036"),sQuery(id+"F8.wireOp",EDGE,"5940f4f9-8053-40e0-b9f8-df2bd4dd714a"),sQuery(id+"F8.wireOp",EDGE,"0ec317e1-7bde-406d-8e37-b692e67ce572"),sQuery(id+"F8.wireOp",EDGE,"10283698-b105-4272-ae0e-b40b5444b7e2"),sQuery(id+"F8.wireOp",EDGE,"2d1b1a56-4447-4509-943e-74e2c6545418"),sQuery(id+"F8.wireOp",EDGE,"f74ce244-fc31-493f-880f-7eb162584e80"),sQuery(id+"F8.wireOp",EDGE,"a7e2ad9e-ede3-45ca-b48e-e2193eb82840"),sQuery(id+"F8.wireOp",EDGE,"122b9492-1201-4a42-aaa1-0471d14b2dc4"),sQuery(id+"F8.wireOp",EDGE,"e5bff28d-96f2-468a-af3d-23bdf37ba861"),sQuery(id+"F8.wireOp",EDGE,"1ba43f30-a641-4398-9979-75c6d653234a"),sQuery(id+"F8.wireOp",EDGE,"69b3b88a-0e8e-4302-b7ec-ccf4c05b827d"),sQuery(id+"F8.wireOp",EDGE,"35f21f84-2580-4ee2-ac0b-d24d994ec7ae"),sQuery(id+"F8.wireOp",EDGE,"c50dc557-ed6c-4e68-a26e-5cfac26b5604"),sQuery(id+"F8.wireOp",EDGE,"21aab268-c427-4641-bf1f-5d90f555438b"),sQuery(id+"F8.wireOp",EDGE,"74c92970-2f70-48a9-9bad-24fac6a61a3d"),sQuery(id+"F8.wireOp",EDGE,"9f654c5c-d71e-4ad6-8b6b-00aa805ed93a"),sQuery(id+"F8.wireOp",EDGE,"54913d02-2ee9-496b-9b90-623226082b28"),sQuery(id+"F8.wireOp",EDGE,"e99af606-050a-48e7-a8a4-a9775c2a0eb2"),sQuery(id+"F8.wireOp",EDGE,"b9d52d30-b605-439b-99ba-378b7fd2762f"),sQuery(id+"F8.wireOp",EDGE,"f329a30d-006b-4ae5-8cbf-6a1b09218d83"),sQuery(id+"F8.wireOp",EDGE,"dd7b8c1c-e3ae-4d03-8be9-f57dd24d2f0b"),sQuery(id+"F8.wireOp",EDGE,"46bfc011-a117-4c41-bfcd-e457596cd4d9"),sQuery(id+"F8.wireOp",EDGE,"6600ac44-2123-45c8-812d-733445cfa9db"),sQuery(id+"F8.wireOp",EDGE,"27268a7f-8bee-4e82-835d-cb25348db130"),sQuery(id+"F8.wireOp",EDGE,"86ebb21e-ed19-4d2b-a4fd-6c6ffebed1b8"),sQuery(id+"F8.wireOp",EDGE,"7cca7813-f0e1-4f51-9fdf-dad795188660"),sQuery(id+"F8.wireOp",EDGE,"1dbc05d7-2243-4f66-aeaf-20431f42a1ee"),sQuery(id+"F8.wireOp",EDGE,"ca0cce8d-3416-4790-bb3e-041637dc07ff"),sQuery(id+"F8.wireOp",EDGE,"12870aea-8d4a-43c5-9976-f373bf1b6e25"),sQuery(id+"F8.wireOp",EDGE,"11d8e0f7-3a68-479a-a03a-1966e2fefdbf"),sQuery(id+"F8.wireOp",EDGE,"d36237ac-1d33-48cb-9d6d-eb775a672cd3"),sQuery(id+"F8.wireOp",EDGE,"159dd2e4-e221-4ead-97e1-555e17f9a3fe"),sQuery(id+"F8.wireOp",EDGE,"925d5a80-3709-4a0b-bca8-b9b5383c7f84"),sQuery(id+"F8.wireOp",EDGE,"ddb5fa77-ccdc-42c6-b80c-3089895e0a9a"),sQuery(id+"F8.wireOp",EDGE,"055d4f96-99b0-4192-8726-099a86a655db"),sQuery(id+"F8.wireOp",EDGE,"ddb7f43f-986f-4b29-89e7-b9f390dd7839"),sQuery(id+"F8.wireOp",EDGE,"631fbb6b-849d-4a7c-9c07-eaec2733591a"),sQuery(id+"F8.wireOp",EDGE,"316a86f4-c8c9-404a-8ddd-36c468b85efb"),sQuery(id+"F8.wireOp",EDGE,"bcb9aef4-4c08-454e-bd09-48bfdbf1118a"),sQuery(id+"F8.wireOp",EDGE,"cb968dff-7d8a-4d18-a2a4-006ce488b08d"),sQuery(id+"F8.wireOp",EDGE,"bda976b6-f62e-42dc-8ff9-8432803c7c90"),sQuery(id+"F8.wireOp",EDGE,"2c3b1d82-f70f-41c4-8453-e6ddc61e1cad"),sQuery(id+"F8.wireOp",EDGE,"c9b8b99b-26f1-4f3e-9e7b-3a5e40e3cb76"),sQuery(id+"F8.wireOp",EDGE,"e008f9f9-464b-4935-b076-15c7db0c9645"),sQuery(id+"F8.wireOp",EDGE,"3093864c-1765-4219-bb0b-fcf6003f7271"),sQuery(id+"F8.wireOp",EDGE,"92c48e1c-e416-4e8d-bd61-d049c761251f"),sQuery(id+"F8.wireOp",EDGE,"8965ebff-202e-4ccf-bd90-51536d00854e"),sQuery(id+"F8.wireOp",EDGE,"b3724e1e-f39f-4e74-ac42-72ffae54ceec"),sQuery(id+"F8.wireOp",EDGE,"e253634c-c2c7-47bf-9e4f-d6ccd5cafe0a"),sQuery(id+"F8.wireOp",EDGE,"E1037"),sQuery(id+"F8.wireOp",EDGE,"E1038"),sQuery(id+"F8.wireOp",EDGE,"E1039"),sQuery(id+"F8.wireOp",EDGE,"E1040"),sQuery(id+"F8.wireOp",EDGE,"E1041"),sQuery(id+"F8.wireOp",EDGE,"E1042"),sQuery(id+"F8.wireOp",EDGE,"E1043"),sQuery(id+"F8.wireOp",EDGE,"E1044"),sQuery(id+"F8.wireOp",EDGE,"E1045"),sQuery(id+"F8.wireOp",EDGE,"E1046"),sQuery(id+"F8.wireOp",EDGE,"E1047"),sQuery(id+"F8.wireOp",EDGE,"E1048"),sQuery(id+"F8.wireOp",EDGE,"E1049"),sQuery(id+"F8.wireOp",EDGE,"E1050"),sQuery(id+"F8.wireOp",EDGE,"E1051"),sQuery(id+"F8.wireOp",EDGE,"E1052"),sQuery(id+"F8.wireOp",EDGE,"E1053"),sQuery(id+"F8.wireOp",EDGE,"E1054"),sQuery(id+"F8.wireOp",EDGE,"E1055"),sQuery(id+"F8.wireOp",EDGE,"E1056"),sQuery(id+"F8.wireOp",EDGE,"E1057"),sQuery(id+"F8.wireOp",EDGE,"E1058"),sQuery(id+"F8.wireOp",EDGE,"E1059"),sQuery(id+"F8.wireOp",EDGE,"E1060")])],"isStart":true});
            cPlane(context, id + "F14", {"entities" : qUnion([Q0]), "cplaneType" : CPlaneType.OFFSET, "offset" : 50 * mm, "width" : 150 * mm, "height" : 150 * mm});
        }
        {
            var Q0;
            Q0=qCreatedBy(id+"F14.planeOp",FACE);
            var sketch = newSketch(context, id + "F15", { "sketchPlane" : qUnion([Q0])});
            skLineSegment(sketch, "E1087", {"start": v(-50, 50) * mm, "end": v(50, 50) * mm});
            skLineSegment(sketch, "E1088", {"start": v(50, 50) * mm, "end": v(50, -50) * mm});
            skLineSegment(sketch, "E1089", {"start": v(50, -50) * mm, "end": v(-50, -50) * mm});
            skLineSegment(sketch, "E1090", {"start": v(-50, -50) * mm, "end": v(-50, 50) * mm});
            skLineSegment(sketch, "E1091", {"start": v(-40.39, 43.95) * mm, "end": v(-40.75, 43.8) * mm});
            skLineSegment(sketch, "E1092", {"start": v(-40.75, 43.8) * mm, "end": v(-41.06, 43.56) * mm});
            skLineSegment(sketch, "E1093", {"start": v(-41.06, 43.56) * mm, "end": v(-41.3, 43.25) * mm});
            skLineSegment(sketch, "E1094", {"start": v(-41.3, 43.25) * mm, "end": v(-41.45, 42.89) * mm});
            skLineSegment(sketch, "E1095", {"start": v(-41.45, 42.89) * mm, "end": v(-41.5, 42.5) * mm});
            skLineSegment(sketch, "E1096", {"start": v(-41.5, 42.5) * mm, "end": v(-41.45, 42.11) * mm});
            skLineSegment(sketch, "E1097", {"start": v(-41.45, 42.11) * mm, "end": v(-41.3, 41.75) * mm});
            skLineSegment(sketch, "E1098", {"start": v(-41.3, 41.75) * mm, "end": v(-41.06, 41.44) * mm});
            skLineSegment(sketch, "E1099", {"start": v(-41.06, 41.44) * mm, "end": v(-40.75, 41.2) * mm});
            skLineSegment(sketch, "E1100", {"start": v(-40.75, 41.2) * mm, "end": v(-40.39, 41.05) * mm});
            skLineSegment(sketch, "E1101", {"start": v(-40.39, 41.05) * mm, "end": v(-40, 41) * mm});
            skLineSegment(sketch, "E1102", {"start": v(-40, 41) * mm, "end": v(-39.61, 41.05) * mm});
            skLineSegment(sketch, "E1103", {"start": v(-39.61, 41.05) * mm, "end": v(-39.25, 41.2) * mm});
            skLineSegment(sketch, "E1104", {"start": v(-39.25, 41.2) * mm, "end": v(-38.94, 41.44) * mm});
            skLineSegment(sketch, "E1105", {"start": v(-38.94, 41.44) * mm, "end": v(-38.7, 41.75) * mm});
            skLineSegment(sketch, "E1106", {"start": v(-38.7, 41.75) * mm, "end": v(-38.55, 42.11) * mm});
            skLineSegment(sketch, "E1107", {"start": v(-38.55, 42.11) * mm, "end": v(-38.5, 42.5) * mm});
            skLineSegment(sketch, "E1108", {"start": v(-38.5, 42.5) * mm, "end": v(-38.55, 42.89) * mm});
            skLineSegment(sketch, "E1109", {"start": v(-38.55, 42.89) * mm, "end": v(-38.7, 43.25) * mm});
            skLineSegment(sketch, "E1110", {"start": v(-38.7, 43.25) * mm, "end": v(-38.94, 43.56) * mm});
            skLineSegment(sketch, "E1111", {"start": v(-38.94, 43.56) * mm, "end": v(-39.25, 43.8) * mm});
            skLineSegment(sketch, "E1112", {"start": v(-39.25, 43.8) * mm, "end": v(-39.61, 43.95) * mm});
            skLineSegment(sketch, "E1113", {"start": v(-39.61, 43.95) * mm, "end": v(-40, 44) * mm});
            skLineSegment(sketch, "E1114", {"start": v(-40, 44) * mm, "end": v(-40.39, 43.95) * mm});
            skLineSegment(sketch, "E1115", {"start": v(-30.39, 41.05) * mm, "end": v(-30, 41) * mm});
            skLineSegment(sketch, "E1116", {"start": v(-30, 41) * mm, "end": v(-29.61, 41.05) * mm});
            skLineSegment(sketch, "E1117", {"start": v(-29.61, 41.05) * mm, "end": v(-29.25, 41.2) * mm});
            skLineSegment(sketch, "E1118", {"start": v(-29.25, 41.2) * mm, "end": v(-28.94, 41.44) * mm});
            skLineSegment(sketch, "E1119", {"start": v(-28.94, 41.44) * mm, "end": v(-28.7, 41.75) * mm});
            skLineSegment(sketch, "E1120", {"start": v(-28.7, 41.75) * mm, "end": v(-28.55, 42.11) * mm});
            skLineSegment(sketch, "E1121", {"start": v(-28.55, 42.11) * mm, "end": v(-28.5, 42.5) * mm});
            skLineSegment(sketch, "E1122", {"start": v(-28.5, 42.5) * mm, "end": v(-28.55, 42.89) * mm});
            skLineSegment(sketch, "E1123", {"start": v(-28.55, 42.89) * mm, "end": v(-28.7, 43.25) * mm});
            skLineSegment(sketch, "E1124", {"start": v(-28.7, 43.25) * mm, "end": v(-28.94, 43.56) * mm});
            skLineSegment(sketch, "E1125", {"start": v(-28.94, 43.56) * mm, "end": v(-29.25, 43.8) * mm});
            skLineSegment(sketch, "E1126", {"start": v(-29.25, 43.8) * mm, "end": v(-29.61, 43.95) * mm});
            skLineSegment(sketch, "E1127", {"start": v(-29.61, 43.95) * mm, "end": v(-30, 44) * mm});
            skLineSegment(sketch, "E1128", {"start": v(-30, 44) * mm, "end": v(-30.39, 43.95) * mm});
            skLineSegment(sketch, "E1129", {"start": v(-30.39, 43.95) * mm, "end": v(-30.75, 43.8) * mm});
            skLineSegment(sketch, "E1130", {"start": v(-30.75, 43.8) * mm, "end": v(-31.06, 43.56) * mm});
            skLineSegment(sketch, "E1131", {"start": v(-31.06, 43.56) * mm, "end": v(-31.3, 43.25) * mm});
            skLineSegment(sketch, "E1132", {"start": v(-31.3, 43.25) * mm, "end": v(-31.45, 42.89) * mm});
            skLineSegment(sketch, "E1133", {"start": v(-31.45, 42.89) * mm, "end": v(-31.5, 42.5) * mm});
            skLineSegment(sketch, "E1134", {"start": v(-31.5, 42.5) * mm, "end": v(-31.45, 42.11) * mm});
            skLineSegment(sketch, "E1135", {"start": v(-31.45, 42.11) * mm, "end": v(-31.3, 41.75) * mm});
            skLineSegment(sketch, "E1136", {"start": v(-31.3, 41.75) * mm, "end": v(-31.06, 41.44) * mm});
            skLineSegment(sketch, "E1137", {"start": v(-31.06, 41.44) * mm, "end": v(-30.75, 41.2) * mm});
            skLineSegment(sketch, "E1138", {"start": v(-30.75, 41.2) * mm, "end": v(-30.39, 41.05) * mm});
            skLineSegment(sketch, "E1139", {"start": v(30, 44) * mm, "end": v(29.61, 43.95) * mm});
            skLineSegment(sketch, "E1140", {"start": v(29.61, 43.95) * mm, "end": v(29.25, 43.8) * mm});
            skLineSegment(sketch, "E1141", {"start": v(29.25, 43.8) * mm, "end": v(28.94, 43.56) * mm});
            skLineSegment(sketch, "E1142", {"start": v(28.94, 43.56) * mm, "end": v(28.7, 43.25) * mm});
            skLineSegment(sketch, "E1143", {"start": v(28.7, 43.25) * mm, "end": v(28.55, 42.89) * mm});
            skLineSegment(sketch, "E1144", {"start": v(28.55, 42.89) * mm, "end": v(28.5, 42.5) * mm});
            skLineSegment(sketch, "E1145", {"start": v(28.5, 42.5) * mm, "end": v(28.55, 42.11) * mm});
            skLineSegment(sketch, "E1146", {"start": v(28.55, 42.11) * mm, "end": v(28.7, 41.75) * mm});
            skLineSegment(sketch, "E1147", {"start": v(28.7, 41.75) * mm, "end": v(28.94, 41.44) * mm});
            skLineSegment(sketch, "E1148", {"start": v(28.94, 41.44) * mm, "end": v(29.25, 41.2) * mm});
            skLineSegment(sketch, "E1149", {"start": v(29.25, 41.2) * mm, "end": v(29.61, 41.05) * mm});
            skLineSegment(sketch, "E1150", {"start": v(29.61, 41.05) * mm, "end": v(30, 41) * mm});
            skLineSegment(sketch, "E1151", {"start": v(30, 41) * mm, "end": v(30.39, 41.05) * mm});
            skLineSegment(sketch, "E1152", {"start": v(30.39, 41.05) * mm, "end": v(30.75, 41.2) * mm});
            skLineSegment(sketch, "E1153", {"start": v(30.75, 41.2) * mm, "end": v(31.06, 41.44) * mm});
            skLineSegment(sketch, "E1154", {"start": v(31.06, 41.44) * mm, "end": v(31.3, 41.75) * mm});
            skLineSegment(sketch, "E1155", {"start": v(31.3, 41.75) * mm, "end": v(31.45, 42.11) * mm});
            skLineSegment(sketch, "E1156", {"start": v(31.45, 42.11) * mm, "end": v(31.5, 42.5) * mm});
            skLineSegment(sketch, "E1157", {"start": v(31.5, 42.5) * mm, "end": v(31.45, 42.89) * mm});
            skLineSegment(sketch, "E1158", {"start": v(31.45, 42.89) * mm, "end": v(31.3, 43.25) * mm});
            skLineSegment(sketch, "E1159", {"start": v(31.3, 43.25) * mm, "end": v(31.06, 43.56) * mm});
            skLineSegment(sketch, "E1160", {"start": v(31.06, 43.56) * mm, "end": v(30.75, 43.8) * mm});
            skLineSegment(sketch, "E1161", {"start": v(30.75, 43.8) * mm, "end": v(30.39, 43.95) * mm});
            skLineSegment(sketch, "E1162", {"start": v(30.39, 43.95) * mm, "end": v(30, 44) * mm});
            skLineSegment(sketch, "E1163", {"start": v(40.39, 41.05) * mm, "end": v(40.75, 41.2) * mm});
            skLineSegment(sketch, "E1164", {"start": v(40.75, 41.2) * mm, "end": v(41.06, 41.44) * mm});
            skLineSegment(sketch, "E1165", {"start": v(41.06, 41.44) * mm, "end": v(41.3, 41.75) * mm});
            skLineSegment(sketch, "E1166", {"start": v(41.3, 41.75) * mm, "end": v(41.45, 42.11) * mm});
            skLineSegment(sketch, "E1167", {"start": v(41.45, 42.11) * mm, "end": v(41.5, 42.5) * mm});
            skLineSegment(sketch, "E1168", {"start": v(41.5, 42.5) * mm, "end": v(41.45, 42.89) * mm});
            skLineSegment(sketch, "E1169", {"start": v(41.45, 42.89) * mm, "end": v(41.3, 43.25) * mm});
            skLineSegment(sketch, "E1170", {"start": v(41.3, 43.25) * mm, "end": v(41.06, 43.56) * mm});
            skLineSegment(sketch, "E1171", {"start": v(41.06, 43.56) * mm, "end": v(40.75, 43.8) * mm});
            skLineSegment(sketch, "E1172", {"start": v(40.75, 43.8) * mm, "end": v(40.39, 43.95) * mm});
            skLineSegment(sketch, "E1173", {"start": v(40.39, 43.95) * mm, "end": v(40, 44) * mm});
            skLineSegment(sketch, "E1174", {"start": v(40, 44) * mm, "end": v(39.61, 43.95) * mm});
            skLineSegment(sketch, "E1175", {"start": v(39.61, 43.95) * mm, "end": v(39.25, 43.8) * mm});
            skLineSegment(sketch, "E1176", {"start": v(39.25, 43.8) * mm, "end": v(38.94, 43.56) * mm});
            skLineSegment(sketch, "E1177", {"start": v(38.94, 43.56) * mm, "end": v(38.7, 43.25) * mm});
            skLineSegment(sketch, "E1178", {"start": v(38.7, 43.25) * mm, "end": v(38.55, 42.89) * mm});
            skLineSegment(sketch, "E1179", {"start": v(38.55, 42.89) * mm, "end": v(38.5, 42.5) * mm});
            skLineSegment(sketch, "E1180", {"start": v(38.5, 42.5) * mm, "end": v(38.55, 42.11) * mm});
            skLineSegment(sketch, "E1181", {"start": v(38.55, 42.11) * mm, "end": v(38.7, 41.75) * mm});
            skLineSegment(sketch, "E1182", {"start": v(38.7, 41.75) * mm, "end": v(38.94, 41.44) * mm});
            skLineSegment(sketch, "E1183", {"start": v(38.94, 41.44) * mm, "end": v(39.25, 41.2) * mm});
            skLineSegment(sketch, "E1184", {"start": v(39.25, 41.2) * mm, "end": v(39.61, 41.05) * mm});
            skLineSegment(sketch, "E1185", {"start": v(39.61, 41.05) * mm, "end": v(40, 41) * mm});
            skLineSegment(sketch, "E1186", {"start": v(40, 41) * mm, "end": v(40.39, 41.05) * mm});
            skLineSegment(sketch, "E1187", {"start": v(31.06, 33.56) * mm, "end": v(30.75, 33.8) * mm});
            skLineSegment(sketch, "E1188", {"start": v(30.75, 33.8) * mm, "end": v(30.39, 33.95) * mm});
            skLineSegment(sketch, "E1189", {"start": v(30.39, 33.95) * mm, "end": v(30, 34) * mm});
            skLineSegment(sketch, "E1190", {"start": v(30, 34) * mm, "end": v(29.61, 33.95) * mm});
            skLineSegment(sketch, "E1191", {"start": v(29.61, 33.95) * mm, "end": v(29.25, 33.8) * mm});
            skLineSegment(sketch, "E1192", {"start": v(29.25, 33.8) * mm, "end": v(28.94, 33.56) * mm});
            skLineSegment(sketch, "E1193", {"start": v(28.94, 33.56) * mm, "end": v(28.7, 33.25) * mm});
            skLineSegment(sketch, "E1194", {"start": v(28.7, 33.25) * mm, "end": v(28.55, 32.89) * mm});
            skLineSegment(sketch, "E1195", {"start": v(28.55, 32.89) * mm, "end": v(28.5, 32.5) * mm});
            skLineSegment(sketch, "E1196", {"start": v(28.5, 32.5) * mm, "end": v(28.55, 32.11) * mm});
            skLineSegment(sketch, "E1197", {"start": v(28.55, 32.11) * mm, "end": v(28.7, 31.75) * mm});
            skLineSegment(sketch, "E1198", {"start": v(28.7, 31.75) * mm, "end": v(28.94, 31.44) * mm});
            skLineSegment(sketch, "E1199", {"start": v(28.94, 31.44) * mm, "end": v(29.25, 31.2) * mm});
            skLineSegment(sketch, "E1200", {"start": v(29.25, 31.2) * mm, "end": v(29.61, 31.05) * mm});
            skLineSegment(sketch, "E1201", {"start": v(29.61, 31.05) * mm, "end": v(30, 31) * mm});
            skLineSegment(sketch, "E1202", {"start": v(30, 31) * mm, "end": v(30.39, 31.05) * mm});
            skLineSegment(sketch, "E1203", {"start": v(30.39, 31.05) * mm, "end": v(30.75, 31.2) * mm});
            skLineSegment(sketch, "E1204", {"start": v(30.75, 31.2) * mm, "end": v(31.06, 31.44) * mm});
            skLineSegment(sketch, "E1205", {"start": v(31.06, 31.44) * mm, "end": v(31.3, 31.75) * mm});
            skLineSegment(sketch, "E1206", {"start": v(31.3, 31.75) * mm, "end": v(31.45, 32.11) * mm});
            skLineSegment(sketch, "E1207", {"start": v(31.45, 32.11) * mm, "end": v(31.5, 32.5) * mm});
            skLineSegment(sketch, "E1208", {"start": v(31.5, 32.5) * mm, "end": v(31.45, 32.89) * mm});
            skLineSegment(sketch, "E1209", {"start": v(31.45, 32.89) * mm, "end": v(31.3, 33.25) * mm});
            skLineSegment(sketch, "E1210", {"start": v(31.3, 33.25) * mm, "end": v(31.06, 33.56) * mm});
            skLineSegment(sketch, "E1211", {"start": v(40.39, 31.05) * mm, "end": v(40.75, 31.2) * mm});
            skLineSegment(sketch, "E1212", {"start": v(40.75, 31.2) * mm, "end": v(41.06, 31.44) * mm});
            skLineSegment(sketch, "E1213", {"start": v(41.06, 31.44) * mm, "end": v(41.3, 31.75) * mm});
            skLineSegment(sketch, "E1214", {"start": v(41.3, 31.75) * mm, "end": v(41.45, 32.11) * mm});
            skLineSegment(sketch, "E1215", {"start": v(41.45, 32.11) * mm, "end": v(41.5, 32.5) * mm});
            skLineSegment(sketch, "E1216", {"start": v(41.5, 32.5) * mm, "end": v(41.45, 32.89) * mm});
            skLineSegment(sketch, "E1217", {"start": v(41.45, 32.89) * mm, "end": v(41.3, 33.25) * mm});
            skLineSegment(sketch, "E1218", {"start": v(41.3, 33.25) * mm, "end": v(41.06, 33.56) * mm});
            skLineSegment(sketch, "E1219", {"start": v(41.06, 33.56) * mm, "end": v(40.75, 33.8) * mm});
            skLineSegment(sketch, "E1220", {"start": v(40.75, 33.8) * mm, "end": v(40.39, 33.95) * mm});
            skLineSegment(sketch, "E1221", {"start": v(40.39, 33.95) * mm, "end": v(40, 34) * mm});
            skLineSegment(sketch, "E1222", {"start": v(40, 34) * mm, "end": v(39.61, 33.95) * mm});
            skLineSegment(sketch, "E1223", {"start": v(39.61, 33.95) * mm, "end": v(39.25, 33.8) * mm});
            skLineSegment(sketch, "E1224", {"start": v(39.25, 33.8) * mm, "end": v(38.94, 33.56) * mm});
            skLineSegment(sketch, "E1225", {"start": v(38.94, 33.56) * mm, "end": v(38.7, 33.25) * mm});
            skLineSegment(sketch, "E1226", {"start": v(38.7, 33.25) * mm, "end": v(38.55, 32.89) * mm});
            skLineSegment(sketch, "E1227", {"start": v(38.55, 32.89) * mm, "end": v(38.5, 32.5) * mm});
            skLineSegment(sketch, "E1228", {"start": v(38.5, 32.5) * mm, "end": v(38.55, 32.11) * mm});
            skLineSegment(sketch, "E1229", {"start": v(38.55, 32.11) * mm, "end": v(38.7, 31.75) * mm});
            skLineSegment(sketch, "E1230", {"start": v(38.7, 31.75) * mm, "end": v(38.94, 31.44) * mm});
            skLineSegment(sketch, "E1231", {"start": v(38.94, 31.44) * mm, "end": v(39.25, 31.2) * mm});
            skLineSegment(sketch, "E1232", {"start": v(39.25, 31.2) * mm, "end": v(39.61, 31.05) * mm});
            skLineSegment(sketch, "E1233", {"start": v(39.61, 31.05) * mm, "end": v(40, 31) * mm});
            skLineSegment(sketch, "E1234", {"start": v(40, 31) * mm, "end": v(40.39, 31.05) * mm});
            skLineSegment(sketch, "E1235", {"start": v(-30.75, 33.8) * mm, "end": v(-31.06, 33.56) * mm});
            skLineSegment(sketch, "E1236", {"start": v(-31.06, 33.56) * mm, "end": v(-31.3, 33.25) * mm});
            skLineSegment(sketch, "E1237", {"start": v(-31.3, 33.25) * mm, "end": v(-31.45, 32.89) * mm});
            skLineSegment(sketch, "E1238", {"start": v(-31.45, 32.89) * mm, "end": v(-31.5, 32.5) * mm});
            skLineSegment(sketch, "E1239", {"start": v(-31.5, 32.5) * mm, "end": v(-31.45, 32.11) * mm});
            skLineSegment(sketch, "E1240", {"start": v(-31.45, 32.11) * mm, "end": v(-31.3, 31.75) * mm});
            skLineSegment(sketch, "E1241", {"start": v(-31.3, 31.75) * mm, "end": v(-31.06, 31.44) * mm});
            skLineSegment(sketch, "E1242", {"start": v(-31.06, 31.44) * mm, "end": v(-30.75, 31.2) * mm});
            skLineSegment(sketch, "E1243", {"start": v(-30.75, 31.2) * mm, "end": v(-30.39, 31.05) * mm});
            skLineSegment(sketch, "E1244", {"start": v(-30.39, 31.05) * mm, "end": v(-30, 31) * mm});
            skLineSegment(sketch, "E1245", {"start": v(-30, 31) * mm, "end": v(-29.61, 31.05) * mm});
            skLineSegment(sketch, "E1246", {"start": v(-29.61, 31.05) * mm, "end": v(-29.25, 31.2) * mm});
            skLineSegment(sketch, "E1247", {"start": v(-29.25, 31.2) * mm, "end": v(-28.94, 31.44) * mm});
            skLineSegment(sketch, "E1248", {"start": v(-28.94, 31.44) * mm, "end": v(-28.7, 31.75) * mm});
            skLineSegment(sketch, "E1249", {"start": v(-28.7, 31.75) * mm, "end": v(-28.55, 32.11) * mm});
            skLineSegment(sketch, "E1250", {"start": v(-28.55, 32.11) * mm, "end": v(-28.5, 32.5) * mm});
            skLineSegment(sketch, "E1251", {"start": v(-28.5, 32.5) * mm, "end": v(-28.55, 32.89) * mm});
            skLineSegment(sketch, "E1252", {"start": v(-28.55, 32.89) * mm, "end": v(-28.7, 33.25) * mm});
            skLineSegment(sketch, "E1253", {"start": v(-28.7, 33.25) * mm, "end": v(-28.94, 33.56) * mm});
            skLineSegment(sketch, "E1254", {"start": v(-28.94, 33.56) * mm, "end": v(-29.25, 33.8) * mm});
            skLineSegment(sketch, "E1255", {"start": v(-29.25, 33.8) * mm, "end": v(-29.61, 33.95) * mm});
            skLineSegment(sketch, "E1256", {"start": v(-29.61, 33.95) * mm, "end": v(-30, 34) * mm});
            skLineSegment(sketch, "E1257", {"start": v(-30, 34) * mm, "end": v(-30.39, 33.95) * mm});
            skLineSegment(sketch, "E1258", {"start": v(-30.39, 33.95) * mm, "end": v(-30.75, 33.8) * mm});
            skLineSegment(sketch, "E1259", {"start": v(-38.5, 32.5) * mm, "end": v(-38.55, 32.89) * mm});
            skLineSegment(sketch, "E1260", {"start": v(-38.55, 32.89) * mm, "end": v(-38.7, 33.25) * mm});
            skLineSegment(sketch, "E1261", {"start": v(-38.7, 33.25) * mm, "end": v(-38.94, 33.56) * mm});
            skLineSegment(sketch, "E1262", {"start": v(-38.94, 33.56) * mm, "end": v(-39.25, 33.8) * mm});
            skLineSegment(sketch, "E1263", {"start": v(-39.25, 33.8) * mm, "end": v(-39.61, 33.95) * mm});
            skLineSegment(sketch, "E1264", {"start": v(-39.61, 33.95) * mm, "end": v(-40, 34) * mm});
            skLineSegment(sketch, "E1265", {"start": v(-40, 34) * mm, "end": v(-40.39, 33.95) * mm});
            skLineSegment(sketch, "E1266", {"start": v(-40.39, 33.95) * mm, "end": v(-40.75, 33.8) * mm});
            skLineSegment(sketch, "E1267", {"start": v(-40.75, 33.8) * mm, "end": v(-41.06, 33.56) * mm});
            skLineSegment(sketch, "E1268", {"start": v(-41.06, 33.56) * mm, "end": v(-41.3, 33.25) * mm});
            skLineSegment(sketch, "E1269", {"start": v(-41.3, 33.25) * mm, "end": v(-41.45, 32.89) * mm});
            skLineSegment(sketch, "E1270", {"start": v(-41.45, 32.89) * mm, "end": v(-41.5, 32.5) * mm});
            skLineSegment(sketch, "E1271", {"start": v(-41.5, 32.5) * mm, "end": v(-41.45, 32.11) * mm});
            skLineSegment(sketch, "E1272", {"start": v(-41.45, 32.11) * mm, "end": v(-41.3, 31.75) * mm});
            skLineSegment(sketch, "E1273", {"start": v(-41.3, 31.75) * mm, "end": v(-41.06, 31.44) * mm});
            skLineSegment(sketch, "E1274", {"start": v(-41.06, 31.44) * mm, "end": v(-40.75, 31.2) * mm});
            skLineSegment(sketch, "E1275", {"start": v(-40.75, 31.2) * mm, "end": v(-40.39, 31.05) * mm});
            skLineSegment(sketch, "E1276", {"start": v(-40.39, 31.05) * mm, "end": v(-40, 31) * mm});
            skLineSegment(sketch, "E1277", {"start": v(-40, 31) * mm, "end": v(-39.61, 31.05) * mm});
            skLineSegment(sketch, "E1278", {"start": v(-39.61, 31.05) * mm, "end": v(-39.25, 31.2) * mm});
            skLineSegment(sketch, "E1279", {"start": v(-39.25, 31.2) * mm, "end": v(-38.94, 31.44) * mm});
            skLineSegment(sketch, "E1280", {"start": v(-38.94, 31.44) * mm, "end": v(-38.7, 31.75) * mm});
            skLineSegment(sketch, "E1281", {"start": v(-38.7, 31.75) * mm, "end": v(-38.55, 32.11) * mm});
            skLineSegment(sketch, "E1282", {"start": v(-38.55, 32.11) * mm, "end": v(-38.5, 32.5) * mm});
            skLineSegment(sketch, "E1283", {"start": v(1.45, 42.89) * mm, "end": v(1.3, 43.25) * mm});
            skLineSegment(sketch, "E1284", {"start": v(1.3, 43.25) * mm, "end": v(1.06, 43.56) * mm});
            skLineSegment(sketch, "E1285", {"start": v(1.06, 43.56) * mm, "end": v(0.75, 43.8) * mm});
            skLineSegment(sketch, "E1286", {"start": v(0.75, 43.8) * mm, "end": v(0.39, 43.95) * mm});
            skLineSegment(sketch, "E1287", {"start": v(0.39, 43.95) * mm, "end": v(0, 44) * mm});
            skLineSegment(sketch, "E1288", {"start": v(0, 44) * mm, "end": v(-0.39, 43.95) * mm});
            skLineSegment(sketch, "E1289", {"start": v(-0.39, 43.95) * mm, "end": v(-0.75, 43.8) * mm});
            skLineSegment(sketch, "E1290", {"start": v(-0.75, 43.8) * mm, "end": v(-1.06, 43.56) * mm});
            skLineSegment(sketch, "E1291", {"start": v(-1.06, 43.56) * mm, "end": v(-1.3, 43.25) * mm});
            skLineSegment(sketch, "E1292", {"start": v(-1.3, 43.25) * mm, "end": v(-1.45, 42.89) * mm});
            skLineSegment(sketch, "E1293", {"start": v(-1.45, 42.89) * mm, "end": v(-1.5, 42.5) * mm});
            skLineSegment(sketch, "E1294", {"start": v(-1.5, 42.5) * mm, "end": v(-1.45, 42.11) * mm});
            skLineSegment(sketch, "E1295", {"start": v(-1.45, 42.11) * mm, "end": v(-1.3, 41.75) * mm});
            skLineSegment(sketch, "E1296", {"start": v(-1.3, 41.75) * mm, "end": v(-1.06, 41.44) * mm});
            skLineSegment(sketch, "E1297", {"start": v(-1.06, 41.44) * mm, "end": v(-0.75, 41.2) * mm});
            skLineSegment(sketch, "E1298", {"start": v(-0.75, 41.2) * mm, "end": v(-0.39, 41.05) * mm});
            skLineSegment(sketch, "E1299", {"start": v(-0.39, 41.05) * mm, "end": v(0, 41) * mm});
            skLineSegment(sketch, "E1300", {"start": v(0, 41) * mm, "end": v(0.39, 41.05) * mm});
            skLineSegment(sketch, "E1301", {"start": v(0.39, 41.05) * mm, "end": v(0.75, 41.2) * mm});
            skLineSegment(sketch, "E1302", {"start": v(0.75, 41.2) * mm, "end": v(1.06, 41.44) * mm});
            skLineSegment(sketch, "E1303", {"start": v(1.06, 41.44) * mm, "end": v(1.3, 41.75) * mm});
            skLineSegment(sketch, "E1304", {"start": v(1.3, 41.75) * mm, "end": v(1.45, 42.11) * mm});
            skLineSegment(sketch, "E1305", {"start": v(1.45, 42.11) * mm, "end": v(1.5, 42.5) * mm});
            skLineSegment(sketch, "E1306", {"start": v(1.5, 42.5) * mm, "end": v(1.45, 42.89) * mm});
            skLineSegment(sketch, "E1307", {"start": v(1.45, 32.11) * mm, "end": v(1.5, 32.5) * mm});
            skLineSegment(sketch, "E1308", {"start": v(1.5, 32.5) * mm, "end": v(1.45, 32.89) * mm});
            skLineSegment(sketch, "E1309", {"start": v(1.45, 32.89) * mm, "end": v(1.3, 33.25) * mm});
            skLineSegment(sketch, "E1310", {"start": v(1.3, 33.25) * mm, "end": v(1.06, 33.56) * mm});
            skLineSegment(sketch, "E1311", {"start": v(1.06, 33.56) * mm, "end": v(0.75, 33.8) * mm});
            skLineSegment(sketch, "E1312", {"start": v(0.75, 33.8) * mm, "end": v(0.39, 33.95) * mm});
            skLineSegment(sketch, "E1313", {"start": v(0.39, 33.95) * mm, "end": v(0, 34) * mm});
            skLineSegment(sketch, "E1314", {"start": v(0, 34) * mm, "end": v(-0.39, 33.95) * mm});
            skLineSegment(sketch, "E1315", {"start": v(-0.39, 33.95) * mm, "end": v(-0.75, 33.8) * mm});
            skLineSegment(sketch, "E1316", {"start": v(-0.75, 33.8) * mm, "end": v(-1.06, 33.56) * mm});
            skLineSegment(sketch, "E1317", {"start": v(-1.06, 33.56) * mm, "end": v(-1.3, 33.25) * mm});
            skLineSegment(sketch, "E1318", {"start": v(-1.3, 33.25) * mm, "end": v(-1.45, 32.89) * mm});
            skLineSegment(sketch, "E1319", {"start": v(-1.45, 32.89) * mm, "end": v(-1.5, 32.5) * mm});
            skLineSegment(sketch, "E1320", {"start": v(-1.5, 32.5) * mm, "end": v(-1.45, 32.11) * mm});
            skLineSegment(sketch, "E1321", {"start": v(-1.45, 32.11) * mm, "end": v(-1.3, 31.75) * mm});
            skLineSegment(sketch, "E1322", {"start": v(-1.3, 31.75) * mm, "end": v(-1.06, 31.44) * mm});
            skLineSegment(sketch, "E1323", {"start": v(-1.06, 31.44) * mm, "end": v(-0.75, 31.2) * mm});
            skLineSegment(sketch, "E1324", {"start": v(-0.75, 31.2) * mm, "end": v(-0.39, 31.05) * mm});
            skLineSegment(sketch, "E1325", {"start": v(-0.39, 31.05) * mm, "end": v(0, 31) * mm});
            skLineSegment(sketch, "E1326", {"start": v(0, 31) * mm, "end": v(0.39, 31.05) * mm});
            skLineSegment(sketch, "E1327", {"start": v(0.39, 31.05) * mm, "end": v(0.75, 31.2) * mm});
            skLineSegment(sketch, "E1328", {"start": v(0.75, 31.2) * mm, "end": v(1.06, 31.44) * mm});
            skLineSegment(sketch, "E1329", {"start": v(1.06, 31.44) * mm, "end": v(1.3, 31.75) * mm});
            skLineSegment(sketch, "E1330", {"start": v(1.3, 31.75) * mm, "end": v(1.45, 32.11) * mm});
            skLineSegment(sketch, "E1331", {"start": v(-0.39, -11.05) * mm, "end": v(-0.75, -11.2) * mm});
            skLineSegment(sketch, "E1332", {"start": v(-0.75, -11.2) * mm, "end": v(-1.06, -11.44) * mm});
            skLineSegment(sketch, "E1333", {"start": v(-1.06, -11.44) * mm, "end": v(-1.3, -11.75) * mm});
            skLineSegment(sketch, "E1334", {"start": v(-1.3, -11.75) * mm, "end": v(-1.45, -12.11) * mm});
            skLineSegment(sketch, "E1335", {"start": v(-1.45, -12.11) * mm, "end": v(-1.5, -12.5) * mm});
            skLineSegment(sketch, "E1336", {"start": v(-1.5, -12.5) * mm, "end": v(-1.45, -12.89) * mm});
            skLineSegment(sketch, "E1337", {"start": v(-1.45, -12.89) * mm, "end": v(-1.3, -13.25) * mm});
            skLineSegment(sketch, "E1338", {"start": v(-1.3, -13.25) * mm, "end": v(-1.06, -13.56) * mm});
            skLineSegment(sketch, "E1339", {"start": v(-1.06, -13.56) * mm, "end": v(-0.75, -13.8) * mm});
            skLineSegment(sketch, "E1340", {"start": v(-0.75, -13.8) * mm, "end": v(-0.39, -13.95) * mm});
            skLineSegment(sketch, "E1341", {"start": v(-0.39, -13.95) * mm, "end": v(0, -14) * mm});
            skLineSegment(sketch, "E1342", {"start": v(0, -14) * mm, "end": v(0.39, -13.95) * mm});
            skLineSegment(sketch, "E1343", {"start": v(0.39, -13.95) * mm, "end": v(0.75, -13.8) * mm});
            skLineSegment(sketch, "E1344", {"start": v(0.75, -13.8) * mm, "end": v(1.06, -13.56) * mm});
            skLineSegment(sketch, "E1345", {"start": v(1.06, -13.56) * mm, "end": v(1.3, -13.25) * mm});
            skLineSegment(sketch, "E1346", {"start": v(1.3, -13.25) * mm, "end": v(1.45, -12.89) * mm});
            skLineSegment(sketch, "E1347", {"start": v(1.45, -12.89) * mm, "end": v(1.5, -12.5) * mm});
            skLineSegment(sketch, "E1348", {"start": v(1.5, -12.5) * mm, "end": v(1.45, -12.11) * mm});
            skLineSegment(sketch, "E1349", {"start": v(1.45, -12.11) * mm, "end": v(1.3, -11.75) * mm});
            skLineSegment(sketch, "E1350", {"start": v(1.3, -11.75) * mm, "end": v(1.06, -11.44) * mm});
            skLineSegment(sketch, "E1351", {"start": v(1.06, -11.44) * mm, "end": v(0.75, -11.2) * mm});
            skLineSegment(sketch, "E1352", {"start": v(0.75, -11.2) * mm, "end": v(0.39, -11.05) * mm});
            skLineSegment(sketch, "E1353", {"start": v(0.39, -11.05) * mm, "end": v(0, -11) * mm});
            skLineSegment(sketch, "E1354", {"start": v(0, -11) * mm, "end": v(-0.39, -11.05) * mm});
            skLineSegment(sketch, "E1355", {"start": v(0.75, -3.8) * mm, "end": v(1.06, -3.56) * mm});
            skLineSegment(sketch, "E1356", {"start": v(1.06, -3.56) * mm, "end": v(1.3, -3.25) * mm});
            skLineSegment(sketch, "E1357", {"start": v(1.3, -3.25) * mm, "end": v(1.45, -2.89) * mm});
            skLineSegment(sketch, "E1358", {"start": v(1.45, -2.89) * mm, "end": v(1.5, -2.5) * mm});
            skLineSegment(sketch, "E1359", {"start": v(1.5, -2.5) * mm, "end": v(1.45, -2.11) * mm});
            skLineSegment(sketch, "E1360", {"start": v(1.45, -2.11) * mm, "end": v(1.3, -1.75) * mm});
            skLineSegment(sketch, "E1361", {"start": v(1.3, -1.75) * mm, "end": v(1.06, -1.44) * mm});
            skLineSegment(sketch, "E1362", {"start": v(1.06, -1.44) * mm, "end": v(0.75, -1.2) * mm});
            skLineSegment(sketch, "E1363", {"start": v(0.75, -1.2) * mm, "end": v(0.39, -1.05) * mm});
            skLineSegment(sketch, "E1364", {"start": v(0.39, -1.05) * mm, "end": v(0, -1) * mm});
            skLineSegment(sketch, "E1365", {"start": v(0, -1) * mm, "end": v(-0.39, -1.05) * mm});
            skLineSegment(sketch, "E1366", {"start": v(-0.39, -1.05) * mm, "end": v(-0.75, -1.2) * mm});
            skLineSegment(sketch, "E1367", {"start": v(-0.75, -1.2) * mm, "end": v(-1.06, -1.44) * mm});
            skLineSegment(sketch, "E1368", {"start": v(-1.06, -1.44) * mm, "end": v(-1.3, -1.75) * mm});
            skLineSegment(sketch, "E1369", {"start": v(-1.3, -1.75) * mm, "end": v(-1.45, -2.11) * mm});
            skLineSegment(sketch, "E1370", {"start": v(-1.45, -2.11) * mm, "end": v(-1.5, -2.5) * mm});
            skLineSegment(sketch, "E1371", {"start": v(-1.5, -2.5) * mm, "end": v(-1.45, -2.89) * mm});
            skLineSegment(sketch, "E1372", {"start": v(-1.45, -2.89) * mm, "end": v(-1.3, -3.25) * mm});
            skLineSegment(sketch, "E1373", {"start": v(-1.3, -3.25) * mm, "end": v(-1.06, -3.56) * mm});
            skLineSegment(sketch, "E1374", {"start": v(-1.06, -3.56) * mm, "end": v(-0.75, -3.8) * mm});
            skLineSegment(sketch, "E1375", {"start": v(-0.75, -3.8) * mm, "end": v(-0.39, -3.95) * mm});
            skLineSegment(sketch, "E1376", {"start": v(-0.39, -3.95) * mm, "end": v(0, -4) * mm});
            skLineSegment(sketch, "E1377", {"start": v(0, -4) * mm, "end": v(0.39, -3.95) * mm});
            skLineSegment(sketch, "E1378", {"start": v(0.39, -3.95) * mm, "end": v(0.75, -3.8) * mm});
            skLineSegment(sketch, "E1379", {"start": v(-1.06, -23.56) * mm, "end": v(-0.75, -23.8) * mm});
            skLineSegment(sketch, "E1380", {"start": v(-0.75, -23.8) * mm, "end": v(-0.39, -23.95) * mm});
            skLineSegment(sketch, "E1381", {"start": v(-0.39, -23.95) * mm, "end": v(0, -24) * mm});
            skLineSegment(sketch, "E1382", {"start": v(0, -24) * mm, "end": v(0.39, -23.95) * mm});
            skLineSegment(sketch, "E1383", {"start": v(0.39, -23.95) * mm, "end": v(0.75, -23.8) * mm});
            skLineSegment(sketch, "E1384", {"start": v(0.75, -23.8) * mm, "end": v(1.06, -23.56) * mm});
            skLineSegment(sketch, "E1385", {"start": v(1.06, -23.56) * mm, "end": v(1.3, -23.25) * mm});
            skLineSegment(sketch, "E1386", {"start": v(1.3, -23.25) * mm, "end": v(1.45, -22.89) * mm});
            skLineSegment(sketch, "E1387", {"start": v(1.45, -22.89) * mm, "end": v(1.5, -22.5) * mm});
            skLineSegment(sketch, "E1388", {"start": v(1.5, -22.5) * mm, "end": v(1.45, -22.11) * mm});
            skLineSegment(sketch, "E1389", {"start": v(1.45, -22.11) * mm, "end": v(1.3, -21.75) * mm});
            skLineSegment(sketch, "E1390", {"start": v(1.3, -21.75) * mm, "end": v(1.06, -21.44) * mm});
            skLineSegment(sketch, "E1391", {"start": v(1.06, -21.44) * mm, "end": v(0.75, -21.2) * mm});
            skLineSegment(sketch, "E1392", {"start": v(0.75, -21.2) * mm, "end": v(0.39, -21.05) * mm});
            skLineSegment(sketch, "E1393", {"start": v(0.39, -21.05) * mm, "end": v(0, -21) * mm});
            skLineSegment(sketch, "E1394", {"start": v(0, -21) * mm, "end": v(-0.39, -21.05) * mm});
            skLineSegment(sketch, "E1395", {"start": v(-0.39, -21.05) * mm, "end": v(-0.75, -21.2) * mm});
            skLineSegment(sketch, "E1396", {"start": v(-0.75, -21.2) * mm, "end": v(-1.06, -21.44) * mm});
            skLineSegment(sketch, "E1397", {"start": v(-1.06, -21.44) * mm, "end": v(-1.3, -21.75) * mm});
            skLineSegment(sketch, "E1398", {"start": v(-1.3, -21.75) * mm, "end": v(-1.45, -22.11) * mm});
            skLineSegment(sketch, "E1399", {"start": v(-1.45, -22.11) * mm, "end": v(-1.5, -22.5) * mm});
            skLineSegment(sketch, "E1400", {"start": v(-1.5, -22.5) * mm, "end": v(-1.45, -22.89) * mm});
            skLineSegment(sketch, "E1401", {"start": v(-1.45, -22.89) * mm, "end": v(-1.3, -23.25) * mm});
            skLineSegment(sketch, "E1402", {"start": v(-1.3, -23.25) * mm, "end": v(-1.06, -23.56) * mm});
            skLineSegment(sketch, "E1403", {"start": v(38.94, 23.56) * mm, "end": v(38.7, 23.25) * mm});
            skLineSegment(sketch, "E1404", {"start": v(38.7, 23.25) * mm, "end": v(38.55, 22.89) * mm});
            skLineSegment(sketch, "E1405", {"start": v(38.55, 22.89) * mm, "end": v(38.5, 22.5) * mm});
            skLineSegment(sketch, "E1406", {"start": v(38.5, 22.5) * mm, "end": v(38.55, 22.11) * mm});
            skLineSegment(sketch, "E1407", {"start": v(38.55, 22.11) * mm, "end": v(38.7, 21.75) * mm});
            skLineSegment(sketch, "E1408", {"start": v(38.7, 21.75) * mm, "end": v(38.94, 21.44) * mm});
            skLineSegment(sketch, "E1409", {"start": v(38.94, 21.44) * mm, "end": v(39.25, 21.2) * mm});
            skLineSegment(sketch, "E1410", {"start": v(39.25, 21.2) * mm, "end": v(39.61, 21.05) * mm});
            skLineSegment(sketch, "E1411", {"start": v(39.61, 21.05) * mm, "end": v(40, 21) * mm});
            skLineSegment(sketch, "E1412", {"start": v(40, 21) * mm, "end": v(40.39, 21.05) * mm});
            skLineSegment(sketch, "E1413", {"start": v(40.39, 21.05) * mm, "end": v(40.75, 21.2) * mm});
            skLineSegment(sketch, "E1414", {"start": v(40.75, 21.2) * mm, "end": v(41.06, 21.44) * mm});
            skLineSegment(sketch, "E1415", {"start": v(41.06, 21.44) * mm, "end": v(41.3, 21.75) * mm});
            skLineSegment(sketch, "E1416", {"start": v(41.3, 21.75) * mm, "end": v(41.45, 22.11) * mm});
            skLineSegment(sketch, "E1417", {"start": v(41.45, 22.11) * mm, "end": v(41.5, 22.5) * mm});
            skLineSegment(sketch, "E1418", {"start": v(41.5, 22.5) * mm, "end": v(41.45, 22.89) * mm});
            skLineSegment(sketch, "E1419", {"start": v(41.45, 22.89) * mm, "end": v(41.3, 23.25) * mm});
            skLineSegment(sketch, "E1420", {"start": v(41.3, 23.25) * mm, "end": v(41.06, 23.56) * mm});
            skLineSegment(sketch, "E1421", {"start": v(41.06, 23.56) * mm, "end": v(40.75, 23.8) * mm});
            skLineSegment(sketch, "E1422", {"start": v(40.75, 23.8) * mm, "end": v(40.39, 23.95) * mm});
            skLineSegment(sketch, "E1423", {"start": v(40.39, 23.95) * mm, "end": v(40, 24) * mm});
            skLineSegment(sketch, "E1424", {"start": v(40, 24) * mm, "end": v(39.61, 23.95) * mm});
            skLineSegment(sketch, "E1425", {"start": v(39.61, 23.95) * mm, "end": v(39.25, 23.8) * mm});
            skLineSegment(sketch, "E1426", {"start": v(39.25, 23.8) * mm, "end": v(38.94, 23.56) * mm});
            skLineSegment(sketch, "E1427", {"start": v(31.06, 21.44) * mm, "end": v(31.3, 21.75) * mm});
            skLineSegment(sketch, "E1428", {"start": v(31.3, 21.75) * mm, "end": v(31.45, 22.11) * mm});
            skLineSegment(sketch, "E1429", {"start": v(31.45, 22.11) * mm, "end": v(31.5, 22.5) * mm});
            skLineSegment(sketch, "E1430", {"start": v(31.5, 22.5) * mm, "end": v(31.45, 22.89) * mm});
            skLineSegment(sketch, "E1431", {"start": v(31.45, 22.89) * mm, "end": v(31.3, 23.25) * mm});
            skLineSegment(sketch, "E1432", {"start": v(31.3, 23.25) * mm, "end": v(31.06, 23.56) * mm});
            skLineSegment(sketch, "E1433", {"start": v(31.06, 23.56) * mm, "end": v(30.75, 23.8) * mm});
            skLineSegment(sketch, "E1434", {"start": v(30.75, 23.8) * mm, "end": v(30.39, 23.95) * mm});
            skLineSegment(sketch, "E1435", {"start": v(30.39, 23.95) * mm, "end": v(30, 24) * mm});
            skLineSegment(sketch, "E1436", {"start": v(30, 24) * mm, "end": v(29.61, 23.95) * mm});
            skLineSegment(sketch, "E1437", {"start": v(29.61, 23.95) * mm, "end": v(29.25, 23.8) * mm});
            skLineSegment(sketch, "E1438", {"start": v(29.25, 23.8) * mm, "end": v(28.94, 23.56) * mm});
            skLineSegment(sketch, "E1439", {"start": v(28.94, 23.56) * mm, "end": v(28.7, 23.25) * mm});
            skLineSegment(sketch, "E1440", {"start": v(28.7, 23.25) * mm, "end": v(28.55, 22.89) * mm});
            skLineSegment(sketch, "E1441", {"start": v(28.55, 22.89) * mm, "end": v(28.5, 22.5) * mm});
            skLineSegment(sketch, "E1442", {"start": v(28.5, 22.5) * mm, "end": v(28.55, 22.11) * mm});
            skLineSegment(sketch, "E1443", {"start": v(28.55, 22.11) * mm, "end": v(28.7, 21.75) * mm});
            skLineSegment(sketch, "E1444", {"start": v(28.7, 21.75) * mm, "end": v(28.94, 21.44) * mm});
            skLineSegment(sketch, "E1445", {"start": v(28.94, 21.44) * mm, "end": v(29.25, 21.2) * mm});
            skLineSegment(sketch, "E1446", {"start": v(29.25, 21.2) * mm, "end": v(29.61, 21.05) * mm});
            skLineSegment(sketch, "E1447", {"start": v(29.61, 21.05) * mm, "end": v(30, 21) * mm});
            skLineSegment(sketch, "E1448", {"start": v(30, 21) * mm, "end": v(30.39, 21.05) * mm});
            skLineSegment(sketch, "E1449", {"start": v(30.39, 21.05) * mm, "end": v(30.75, 21.2) * mm});
            skLineSegment(sketch, "E1450", {"start": v(30.75, 21.2) * mm, "end": v(31.06, 21.44) * mm});
            skLineSegment(sketch, "E1451", {"start": v(-0.39, 23.95) * mm, "end": v(-0.75, 23.8) * mm});
            skLineSegment(sketch, "E1452", {"start": v(-0.75, 23.8) * mm, "end": v(-1.06, 23.56) * mm});
            skLineSegment(sketch, "E1453", {"start": v(-1.06, 23.56) * mm, "end": v(-1.3, 23.25) * mm});
            skLineSegment(sketch, "E1454", {"start": v(-1.3, 23.25) * mm, "end": v(-1.45, 22.89) * mm});
            skLineSegment(sketch, "E1455", {"start": v(-1.45, 22.89) * mm, "end": v(-1.5, 22.5) * mm});
            skLineSegment(sketch, "E1456", {"start": v(-1.5, 22.5) * mm, "end": v(-1.45, 22.11) * mm});
            skLineSegment(sketch, "E1457", {"start": v(-1.45, 22.11) * mm, "end": v(-1.3, 21.75) * mm});
            skLineSegment(sketch, "E1458", {"start": v(-1.3, 21.75) * mm, "end": v(-1.06, 21.44) * mm});
            skLineSegment(sketch, "E1459", {"start": v(-1.06, 21.44) * mm, "end": v(-0.75, 21.2) * mm});
            skLineSegment(sketch, "E1460", {"start": v(-0.75, 21.2) * mm, "end": v(-0.39, 21.05) * mm});
            skLineSegment(sketch, "E1461", {"start": v(-0.39, 21.05) * mm, "end": v(0, 21) * mm});
            skLineSegment(sketch, "E1462", {"start": v(0, 21) * mm, "end": v(0.39, 21.05) * mm});
            skLineSegment(sketch, "E1463", {"start": v(0.39, 21.05) * mm, "end": v(0.75, 21.2) * mm});
            skLineSegment(sketch, "E1464", {"start": v(0.75, 21.2) * mm, "end": v(1.06, 21.44) * mm});
            skLineSegment(sketch, "E1465", {"start": v(1.06, 21.44) * mm, "end": v(1.3, 21.75) * mm});
            skLineSegment(sketch, "E1466", {"start": v(1.3, 21.75) * mm, "end": v(1.45, 22.11) * mm});
            skLineSegment(sketch, "E1467", {"start": v(1.45, 22.11) * mm, "end": v(1.5, 22.5) * mm});
            skLineSegment(sketch, "E1468", {"start": v(1.5, 22.5) * mm, "end": v(1.45, 22.89) * mm});
            skLineSegment(sketch, "E1469", {"start": v(1.45, 22.89) * mm, "end": v(1.3, 23.25) * mm});
            skLineSegment(sketch, "E1470", {"start": v(1.3, 23.25) * mm, "end": v(1.06, 23.56) * mm});
            skLineSegment(sketch, "E1471", {"start": v(1.06, 23.56) * mm, "end": v(0.75, 23.8) * mm});
            skLineSegment(sketch, "E1472", {"start": v(0.75, 23.8) * mm, "end": v(0.39, 23.95) * mm});
            skLineSegment(sketch, "E1473", {"start": v(0.39, 23.95) * mm, "end": v(0, 24) * mm});
            skLineSegment(sketch, "E1474", {"start": v(0, 24) * mm, "end": v(-0.39, 23.95) * mm});
            skLineSegment(sketch, "E1475", {"start": v(-29.25, 23.8) * mm, "end": v(-29.61, 23.95) * mm});
            skLineSegment(sketch, "E1476", {"start": v(-29.61, 23.95) * mm, "end": v(-30, 24) * mm});
            skLineSegment(sketch, "E1477", {"start": v(-30, 24) * mm, "end": v(-30.39, 23.95) * mm});
            skLineSegment(sketch, "E1478", {"start": v(-30.39, 23.95) * mm, "end": v(-30.75, 23.8) * mm});
            skLineSegment(sketch, "E1479", {"start": v(-30.75, 23.8) * mm, "end": v(-31.06, 23.56) * mm});
            skLineSegment(sketch, "E1480", {"start": v(-31.06, 23.56) * mm, "end": v(-31.3, 23.25) * mm});
            skLineSegment(sketch, "E1481", {"start": v(-31.3, 23.25) * mm, "end": v(-31.45, 22.89) * mm});
            skLineSegment(sketch, "E1482", {"start": v(-31.45, 22.89) * mm, "end": v(-31.5, 22.5) * mm});
            skLineSegment(sketch, "E1483", {"start": v(-31.5, 22.5) * mm, "end": v(-31.45, 22.11) * mm});
            skLineSegment(sketch, "E1484", {"start": v(-31.45, 22.11) * mm, "end": v(-31.3, 21.75) * mm});
            skLineSegment(sketch, "E1485", {"start": v(-31.3, 21.75) * mm, "end": v(-31.06, 21.44) * mm});
            skLineSegment(sketch, "E1486", {"start": v(-31.06, 21.44) * mm, "end": v(-30.75, 21.2) * mm});
            skLineSegment(sketch, "E1487", {"start": v(-30.75, 21.2) * mm, "end": v(-30.39, 21.05) * mm});
            skLineSegment(sketch, "E1488", {"start": v(-30.39, 21.05) * mm, "end": v(-30, 21) * mm});
            skLineSegment(sketch, "E1489", {"start": v(-30, 21) * mm, "end": v(-29.61, 21.05) * mm});
            skLineSegment(sketch, "E1490", {"start": v(-29.61, 21.05) * mm, "end": v(-29.25, 21.2) * mm});
            skLineSegment(sketch, "E1491", {"start": v(-29.25, 21.2) * mm, "end": v(-28.94, 21.44) * mm});
            skLineSegment(sketch, "E1492", {"start": v(-28.94, 21.44) * mm, "end": v(-28.7, 21.75) * mm});
            skLineSegment(sketch, "E1493", {"start": v(-28.7, 21.75) * mm, "end": v(-28.55, 22.11) * mm});
            skLineSegment(sketch, "E1494", {"start": v(-28.55, 22.11) * mm, "end": v(-28.5, 22.5) * mm});
            skLineSegment(sketch, "E1495", {"start": v(-28.5, 22.5) * mm, "end": v(-28.55, 22.89) * mm});
            skLineSegment(sketch, "E1496", {"start": v(-28.55, 22.89) * mm, "end": v(-28.7, 23.25) * mm});
            skLineSegment(sketch, "E1497", {"start": v(-28.7, 23.25) * mm, "end": v(-28.94, 23.56) * mm});
            skLineSegment(sketch, "E1498", {"start": v(-28.94, 23.56) * mm, "end": v(-29.25, 23.8) * mm});
            skLineSegment(sketch, "E1499", {"start": v(-38.5, 22.5) * mm, "end": v(-38.55, 22.89) * mm});
            skLineSegment(sketch, "E1500", {"start": v(-38.55, 22.89) * mm, "end": v(-38.7, 23.25) * mm});
            skLineSegment(sketch, "E1501", {"start": v(-38.7, 23.25) * mm, "end": v(-38.94, 23.56) * mm});
            skLineSegment(sketch, "E1502", {"start": v(-38.94, 23.56) * mm, "end": v(-39.25, 23.8) * mm});
            skLineSegment(sketch, "E1503", {"start": v(-39.25, 23.8) * mm, "end": v(-39.61, 23.95) * mm});
            skLineSegment(sketch, "E1504", {"start": v(-39.61, 23.95) * mm, "end": v(-40, 24) * mm});
            skLineSegment(sketch, "E1505", {"start": v(-40, 24) * mm, "end": v(-40.39, 23.95) * mm});
            skLineSegment(sketch, "E1506", {"start": v(-40.39, 23.95) * mm, "end": v(-40.75, 23.8) * mm});
            skLineSegment(sketch, "E1507", {"start": v(-40.75, 23.8) * mm, "end": v(-41.06, 23.56) * mm});
            skLineSegment(sketch, "E1508", {"start": v(-41.06, 23.56) * mm, "end": v(-41.3, 23.25) * mm});
            skLineSegment(sketch, "E1509", {"start": v(-41.3, 23.25) * mm, "end": v(-41.45, 22.89) * mm});
            skLineSegment(sketch, "E1510", {"start": v(-41.45, 22.89) * mm, "end": v(-41.5, 22.5) * mm});
            skLineSegment(sketch, "E1511", {"start": v(-41.5, 22.5) * mm, "end": v(-41.45, 22.11) * mm});
            skLineSegment(sketch, "E1512", {"start": v(-41.45, 22.11) * mm, "end": v(-41.3, 21.75) * mm});
            skLineSegment(sketch, "E1513", {"start": v(-41.3, 21.75) * mm, "end": v(-41.06, 21.44) * mm});
            skLineSegment(sketch, "E1514", {"start": v(-41.06, 21.44) * mm, "end": v(-40.75, 21.2) * mm});
            skLineSegment(sketch, "E1515", {"start": v(-40.75, 21.2) * mm, "end": v(-40.39, 21.05) * mm});
            skLineSegment(sketch, "E1516", {"start": v(-40.39, 21.05) * mm, "end": v(-40, 21) * mm});
            skLineSegment(sketch, "E1517", {"start": v(-40, 21) * mm, "end": v(-39.61, 21.05) * mm});
            skLineSegment(sketch, "E1518", {"start": v(-39.61, 21.05) * mm, "end": v(-39.25, 21.2) * mm});
            skLineSegment(sketch, "E1519", {"start": v(-39.25, 21.2) * mm, "end": v(-38.94, 21.44) * mm});
            skLineSegment(sketch, "E1520", {"start": v(-38.94, 21.44) * mm, "end": v(-38.7, 21.75) * mm});
            skLineSegment(sketch, "E1521", {"start": v(-38.7, 21.75) * mm, "end": v(-38.55, 22.11) * mm});
            skLineSegment(sketch, "E1522", {"start": v(-38.55, 22.11) * mm, "end": v(-38.5, 22.5) * mm});
            skLineSegment(sketch, "E1523", {"start": v(-24, 35) * mm, "end": v(-23.35, 35.09) * mm});
            skLineSegment(sketch, "E1524", {"start": v(-23.35, 35.09) * mm, "end": v(-22.75, 35.33) * mm});
            skLineSegment(sketch, "E1525", {"start": v(-22.75, 35.33) * mm, "end": v(-22.23, 35.73) * mm});
            skLineSegment(sketch, "E1526", {"start": v(-22.23, 35.73) * mm, "end": v(-21.83, 36.25) * mm});
            skLineSegment(sketch, "E1527", {"start": v(-21.83, 36.25) * mm, "end": v(-21.59, 36.85) * mm});
            skLineSegment(sketch, "E1528", {"start": v(-21.59, 36.85) * mm, "end": v(-21.5, 37.5) * mm});
            skLineSegment(sketch, "E1529", {"start": v(-21.5, 37.5) * mm, "end": v(-21.59, 38.15) * mm});
            skLineSegment(sketch, "E1530", {"start": v(-21.59, 38.15) * mm, "end": v(-21.83, 38.75) * mm});
            skLineSegment(sketch, "E1531", {"start": v(-21.83, 38.75) * mm, "end": v(-22.23, 39.27) * mm});
            skLineSegment(sketch, "E1532", {"start": v(-22.23, 39.27) * mm, "end": v(-22.75, 39.67) * mm});
            skLineSegment(sketch, "E1533", {"start": v(-22.75, 39.67) * mm, "end": v(-23.35, 39.91) * mm});
            skLineSegment(sketch, "E1534", {"start": v(-23.35, 39.91) * mm, "end": v(-24, 40) * mm});
            skLineSegment(sketch, "E1535", {"start": v(-24, 40) * mm, "end": v(-24.65, 39.91) * mm});
            skLineSegment(sketch, "E1536", {"start": v(-24.65, 39.91) * mm, "end": v(-25.25, 39.67) * mm});
            skLineSegment(sketch, "E1537", {"start": v(-25.25, 39.67) * mm, "end": v(-25.77, 39.27) * mm});
            skLineSegment(sketch, "E1538", {"start": v(-25.77, 39.27) * mm, "end": v(-26.17, 38.75) * mm});
            skLineSegment(sketch, "E1539", {"start": v(-26.17, 38.75) * mm, "end": v(-26.41, 38.15) * mm});
            skLineSegment(sketch, "E1540", {"start": v(-26.41, 38.15) * mm, "end": v(-26.5, 37.5) * mm});
            skLineSegment(sketch, "E1541", {"start": v(-26.5, 37.5) * mm, "end": v(-26.41, 36.85) * mm});
            skLineSegment(sketch, "E1542", {"start": v(-26.41, 36.85) * mm, "end": v(-26.17, 36.25) * mm});
            skLineSegment(sketch, "E1543", {"start": v(-26.17, 36.25) * mm, "end": v(-25.77, 35.73) * mm});
            skLineSegment(sketch, "E1544", {"start": v(-25.77, 35.73) * mm, "end": v(-25.25, 35.33) * mm});
            skLineSegment(sketch, "E1545", {"start": v(-25.25, 35.33) * mm, "end": v(-24.65, 35.09) * mm});
            skLineSegment(sketch, "E1546", {"start": v(-24.65, 35.09) * mm, "end": v(-24, 35) * mm});
            skLineSegment(sketch, "E1547", {"start": v(25.77, 35.73) * mm, "end": v(26.17, 36.25) * mm});
            skLineSegment(sketch, "E1548", {"start": v(26.17, 36.25) * mm, "end": v(26.41, 36.85) * mm});
            skLineSegment(sketch, "E1549", {"start": v(26.41, 36.85) * mm, "end": v(26.5, 37.5) * mm});
            skLineSegment(sketch, "E1550", {"start": v(26.5, 37.5) * mm, "end": v(26.41, 38.15) * mm});
            skLineSegment(sketch, "E1551", {"start": v(26.41, 38.15) * mm, "end": v(26.17, 38.75) * mm});
            skLineSegment(sketch, "E1552", {"start": v(26.17, 38.75) * mm, "end": v(25.77, 39.27) * mm});
            skLineSegment(sketch, "E1553", {"start": v(25.77, 39.27) * mm, "end": v(25.25, 39.67) * mm});
            skLineSegment(sketch, "E1554", {"start": v(25.25, 39.67) * mm, "end": v(24.65, 39.91) * mm});
            skLineSegment(sketch, "E1555", {"start": v(24.65, 39.91) * mm, "end": v(24, 40) * mm});
            skLineSegment(sketch, "E1556", {"start": v(24, 40) * mm, "end": v(23.35, 39.91) * mm});
            skLineSegment(sketch, "E1557", {"start": v(23.35, 39.91) * mm, "end": v(22.75, 39.67) * mm});
            skLineSegment(sketch, "E1558", {"start": v(22.75, 39.67) * mm, "end": v(22.23, 39.27) * mm});
            skLineSegment(sketch, "E1559", {"start": v(22.23, 39.27) * mm, "end": v(21.83, 38.75) * mm});
            skLineSegment(sketch, "E1560", {"start": v(21.83, 38.75) * mm, "end": v(21.59, 38.15) * mm});
            skLineSegment(sketch, "E1561", {"start": v(21.59, 38.15) * mm, "end": v(21.5, 37.5) * mm});
            skLineSegment(sketch, "E1562", {"start": v(21.5, 37.5) * mm, "end": v(21.59, 36.85) * mm});
            skLineSegment(sketch, "E1563", {"start": v(21.59, 36.85) * mm, "end": v(21.83, 36.25) * mm});
            skLineSegment(sketch, "E1564", {"start": v(21.83, 36.25) * mm, "end": v(22.23, 35.73) * mm});
            skLineSegment(sketch, "E1565", {"start": v(22.23, 35.73) * mm, "end": v(22.75, 35.33) * mm});
            skLineSegment(sketch, "E1566", {"start": v(22.75, 35.33) * mm, "end": v(23.35, 35.09) * mm});
            skLineSegment(sketch, "E1567", {"start": v(23.35, 35.09) * mm, "end": v(24, 35) * mm});
            skLineSegment(sketch, "E1568", {"start": v(24, 35) * mm, "end": v(24.65, 35.09) * mm});
            skLineSegment(sketch, "E1569", {"start": v(24.65, 35.09) * mm, "end": v(25.25, 35.33) * mm});
            skLineSegment(sketch, "E1570", {"start": v(25.25, 35.33) * mm, "end": v(25.77, 35.73) * mm});
            skLineSegment(sketch, "E1571", {"start": v(-26.5, 27.5) * mm, "end": v(-26.41, 26.85) * mm});
            skLineSegment(sketch, "E1572", {"start": v(-26.41, 26.85) * mm, "end": v(-26.17, 26.25) * mm});
            skLineSegment(sketch, "E1573", {"start": v(-26.17, 26.25) * mm, "end": v(-25.77, 25.73) * mm});
            skLineSegment(sketch, "E1574", {"start": v(-25.77, 25.73) * mm, "end": v(-25.25, 25.33) * mm});
            skLineSegment(sketch, "E1575", {"start": v(-25.25, 25.33) * mm, "end": v(-24.65, 25.09) * mm});
            skLineSegment(sketch, "E1576", {"start": v(-24.65, 25.09) * mm, "end": v(-24, 25) * mm});
            skLineSegment(sketch, "E1577", {"start": v(-24, 25) * mm, "end": v(-23.35, 25.09) * mm});
            skLineSegment(sketch, "E1578", {"start": v(-23.35, 25.09) * mm, "end": v(-22.75, 25.33) * mm});
            skLineSegment(sketch, "E1579", {"start": v(-22.75, 25.33) * mm, "end": v(-22.23, 25.73) * mm});
            skLineSegment(sketch, "E1580", {"start": v(-22.23, 25.73) * mm, "end": v(-21.83, 26.25) * mm});
            skLineSegment(sketch, "E1581", {"start": v(-21.83, 26.25) * mm, "end": v(-21.59, 26.85) * mm});
            skLineSegment(sketch, "E1582", {"start": v(-21.59, 26.85) * mm, "end": v(-21.5, 27.5) * mm});
            skLineSegment(sketch, "E1583", {"start": v(-21.5, 27.5) * mm, "end": v(-21.59, 28.15) * mm});
            skLineSegment(sketch, "E1584", {"start": v(-21.59, 28.15) * mm, "end": v(-21.83, 28.75) * mm});
            skLineSegment(sketch, "E1585", {"start": v(-21.83, 28.75) * mm, "end": v(-22.23, 29.27) * mm});
            skLineSegment(sketch, "E1586", {"start": v(-22.23, 29.27) * mm, "end": v(-22.75, 29.67) * mm});
            skLineSegment(sketch, "E1587", {"start": v(-22.75, 29.67) * mm, "end": v(-23.35, 29.91) * mm});
            skLineSegment(sketch, "E1588", {"start": v(-23.35, 29.91) * mm, "end": v(-24, 30) * mm});
            skLineSegment(sketch, "E1589", {"start": v(-24, 30) * mm, "end": v(-24.65, 29.91) * mm});
            skLineSegment(sketch, "E1590", {"start": v(-24.65, 29.91) * mm, "end": v(-25.25, 29.67) * mm});
            skLineSegment(sketch, "E1591", {"start": v(-25.25, 29.67) * mm, "end": v(-25.77, 29.27) * mm});
            skLineSegment(sketch, "E1592", {"start": v(-25.77, 29.27) * mm, "end": v(-26.17, 28.75) * mm});
            skLineSegment(sketch, "E1593", {"start": v(-26.17, 28.75) * mm, "end": v(-26.41, 28.15) * mm});
            skLineSegment(sketch, "E1594", {"start": v(-26.41, 28.15) * mm, "end": v(-26.5, 27.5) * mm});
            skLineSegment(sketch, "E1595", {"start": v(24, 25) * mm, "end": v(24.65, 25.09) * mm});
            skLineSegment(sketch, "E1596", {"start": v(24.65, 25.09) * mm, "end": v(25.25, 25.33) * mm});
            skLineSegment(sketch, "E1597", {"start": v(25.25, 25.33) * mm, "end": v(25.77, 25.73) * mm});
            skLineSegment(sketch, "E1598", {"start": v(25.77, 25.73) * mm, "end": v(26.17, 26.25) * mm});
            skLineSegment(sketch, "E1599", {"start": v(26.17, 26.25) * mm, "end": v(26.41, 26.85) * mm});
            skLineSegment(sketch, "E1600", {"start": v(26.41, 26.85) * mm, "end": v(26.5, 27.5) * mm});
            skLineSegment(sketch, "E1601", {"start": v(26.5, 27.5) * mm, "end": v(26.41, 28.15) * mm});
            skLineSegment(sketch, "E1602", {"start": v(26.41, 28.15) * mm, "end": v(26.17, 28.75) * mm});
            skLineSegment(sketch, "E1603", {"start": v(26.17, 28.75) * mm, "end": v(25.77, 29.27) * mm});
            skLineSegment(sketch, "E1604", {"start": v(25.77, 29.27) * mm, "end": v(25.25, 29.67) * mm});
            skLineSegment(sketch, "E1605", {"start": v(25.25, 29.67) * mm, "end": v(24.65, 29.91) * mm});
            skLineSegment(sketch, "E1606", {"start": v(24.65, 29.91) * mm, "end": v(24, 30) * mm});
            skLineSegment(sketch, "E1607", {"start": v(24, 30) * mm, "end": v(23.35, 29.91) * mm});
            skLineSegment(sketch, "E1608", {"start": v(23.35, 29.91) * mm, "end": v(22.75, 29.67) * mm});
            skLineSegment(sketch, "E1609", {"start": v(22.75, 29.67) * mm, "end": v(22.23, 29.27) * mm});
            skLineSegment(sketch, "E1610", {"start": v(22.23, 29.27) * mm, "end": v(21.83, 28.75) * mm});
            skLineSegment(sketch, "E1611", {"start": v(21.83, 28.75) * mm, "end": v(21.59, 28.15) * mm});
            skLineSegment(sketch, "E1612", {"start": v(21.59, 28.15) * mm, "end": v(21.5, 27.5) * mm});
            skLineSegment(sketch, "E1613", {"start": v(21.5, 27.5) * mm, "end": v(21.59, 26.85) * mm});
            skLineSegment(sketch, "E1614", {"start": v(21.59, 26.85) * mm, "end": v(21.83, 26.25) * mm});
            skLineSegment(sketch, "E1615", {"start": v(21.83, 26.25) * mm, "end": v(22.23, 25.73) * mm});
            skLineSegment(sketch, "E1616", {"start": v(22.23, 25.73) * mm, "end": v(22.75, 25.33) * mm});
            skLineSegment(sketch, "E1617", {"start": v(22.75, 25.33) * mm, "end": v(23.35, 25.09) * mm});
            skLineSegment(sketch, "E1618", {"start": v(23.35, 25.09) * mm, "end": v(24, 25) * mm});
            skLineSegment(sketch, "E1619", {"start": v(-42.61, -3.95) * mm, "end": v(-42.25, -3.8) * mm});
            skLineSegment(sketch, "E1620", {"start": v(-42.25, -3.8) * mm, "end": v(-41.94, -3.56) * mm});
            skLineSegment(sketch, "E1621", {"start": v(-41.94, -3.56) * mm, "end": v(-41.7, -3.25) * mm});
            skLineSegment(sketch, "E1622", {"start": v(-41.7, -3.25) * mm, "end": v(-41.55, -2.89) * mm});
            skLineSegment(sketch, "E1623", {"start": v(-41.55, -2.89) * mm, "end": v(-41.5, -2.5) * mm});
            skLineSegment(sketch, "E1624", {"start": v(-41.5, -2.5) * mm, "end": v(-41.55, -2.11) * mm});
            skLineSegment(sketch, "E1625", {"start": v(-41.55, -2.11) * mm, "end": v(-41.7, -1.75) * mm});
            skLineSegment(sketch, "E1626", {"start": v(-41.7, -1.75) * mm, "end": v(-41.94, -1.44) * mm});
            skLineSegment(sketch, "E1627", {"start": v(-41.94, -1.44) * mm, "end": v(-42.25, -1.2) * mm});
            skLineSegment(sketch, "E1628", {"start": v(-42.25, -1.2) * mm, "end": v(-42.61, -1.05) * mm});
            skLineSegment(sketch, "E1629", {"start": v(-42.61, -1.05) * mm, "end": v(-43, -1) * mm});
            skLineSegment(sketch, "E1630", {"start": v(-43, -1) * mm, "end": v(-43.39, -1.05) * mm});
            skLineSegment(sketch, "E1631", {"start": v(-43.39, -1.05) * mm, "end": v(-43.75, -1.2) * mm});
            skLineSegment(sketch, "E1632", {"start": v(-43.75, -1.2) * mm, "end": v(-44.06, -1.44) * mm});
            skLineSegment(sketch, "E1633", {"start": v(-44.06, -1.44) * mm, "end": v(-44.3, -1.75) * mm});
            skLineSegment(sketch, "E1634", {"start": v(-44.3, -1.75) * mm, "end": v(-44.45, -2.11) * mm});
            skLineSegment(sketch, "E1635", {"start": v(-44.45, -2.11) * mm, "end": v(-44.5, -2.5) * mm});
            skLineSegment(sketch, "E1636", {"start": v(-44.5, -2.5) * mm, "end": v(-44.45, -2.89) * mm});
            skLineSegment(sketch, "E1637", {"start": v(-44.45, -2.89) * mm, "end": v(-44.3, -3.25) * mm});
            skLineSegment(sketch, "E1638", {"start": v(-44.3, -3.25) * mm, "end": v(-44.06, -3.56) * mm});
            skLineSegment(sketch, "E1639", {"start": v(-44.06, -3.56) * mm, "end": v(-43.75, -3.8) * mm});
            skLineSegment(sketch, "E1640", {"start": v(-43.75, -3.8) * mm, "end": v(-43.39, -3.95) * mm});
            skLineSegment(sketch, "E1641", {"start": v(-43.39, -3.95) * mm, "end": v(-43, -4) * mm});
            skLineSegment(sketch, "E1642", {"start": v(-43, -4) * mm, "end": v(-42.61, -3.95) * mm});
            skLineSegment(sketch, "E1643", {"start": v(-41.55, -12.89) * mm, "end": v(-41.5, -12.5) * mm});
            skLineSegment(sketch, "E1644", {"start": v(-41.5, -12.5) * mm, "end": v(-41.55, -12.11) * mm});
            skLineSegment(sketch, "E1645", {"start": v(-41.55, -12.11) * mm, "end": v(-41.7, -11.75) * mm});
            skLineSegment(sketch, "E1646", {"start": v(-41.7, -11.75) * mm, "end": v(-41.94, -11.44) * mm});
            skLineSegment(sketch, "E1647", {"start": v(-41.94, -11.44) * mm, "end": v(-42.25, -11.2) * mm});
            skLineSegment(sketch, "E1648", {"start": v(-42.25, -11.2) * mm, "end": v(-42.61, -11.05) * mm});
            skLineSegment(sketch, "E1649", {"start": v(-42.61, -11.05) * mm, "end": v(-43, -11) * mm});
            skLineSegment(sketch, "E1650", {"start": v(-43, -11) * mm, "end": v(-43.39, -11.05) * mm});
            skLineSegment(sketch, "E1651", {"start": v(-43.39, -11.05) * mm, "end": v(-43.75, -11.2) * mm});
            skLineSegment(sketch, "E1652", {"start": v(-43.75, -11.2) * mm, "end": v(-44.06, -11.44) * mm});
            skLineSegment(sketch, "E1653", {"start": v(-44.06, -11.44) * mm, "end": v(-44.3, -11.75) * mm});
            skLineSegment(sketch, "E1654", {"start": v(-44.3, -11.75) * mm, "end": v(-44.45, -12.11) * mm});
            skLineSegment(sketch, "E1655", {"start": v(-44.45, -12.11) * mm, "end": v(-44.5, -12.5) * mm});
            skLineSegment(sketch, "E1656", {"start": v(-44.5, -12.5) * mm, "end": v(-44.45, -12.89) * mm});
            skLineSegment(sketch, "E1657", {"start": v(-44.45, -12.89) * mm, "end": v(-44.3, -13.25) * mm});
            skLineSegment(sketch, "E1658", {"start": v(-44.3, -13.25) * mm, "end": v(-44.06, -13.56) * mm});
            skLineSegment(sketch, "E1659", {"start": v(-44.06, -13.56) * mm, "end": v(-43.75, -13.8) * mm});
            skLineSegment(sketch, "E1660", {"start": v(-43.75, -13.8) * mm, "end": v(-43.39, -13.95) * mm});
            skLineSegment(sketch, "E1661", {"start": v(-43.39, -13.95) * mm, "end": v(-43, -14) * mm});
            skLineSegment(sketch, "E1662", {"start": v(-43, -14) * mm, "end": v(-42.61, -13.95) * mm});
            skLineSegment(sketch, "E1663", {"start": v(-42.61, -13.95) * mm, "end": v(-42.25, -13.8) * mm});
            skLineSegment(sketch, "E1664", {"start": v(-42.25, -13.8) * mm, "end": v(-41.94, -13.56) * mm});
            skLineSegment(sketch, "E1665", {"start": v(-41.94, -13.56) * mm, "end": v(-41.7, -13.25) * mm});
            skLineSegment(sketch, "E1666", {"start": v(-41.7, -13.25) * mm, "end": v(-41.55, -12.89) * mm});
            skLineSegment(sketch, "E1667", {"start": v(-42.61, -23.95) * mm, "end": v(-42.25, -23.8) * mm});
            skLineSegment(sketch, "E1668", {"start": v(-42.25, -23.8) * mm, "end": v(-41.94, -23.56) * mm});
            skLineSegment(sketch, "E1669", {"start": v(-41.94, -23.56) * mm, "end": v(-41.7, -23.25) * mm});
            skLineSegment(sketch, "E1670", {"start": v(-41.7, -23.25) * mm, "end": v(-41.55, -22.89) * mm});
            skLineSegment(sketch, "E1671", {"start": v(-41.55, -22.89) * mm, "end": v(-41.5, -22.5) * mm});
            skLineSegment(sketch, "E1672", {"start": v(-41.5, -22.5) * mm, "end": v(-41.55, -22.11) * mm});
            skLineSegment(sketch, "E1673", {"start": v(-41.55, -22.11) * mm, "end": v(-41.7, -21.75) * mm});
            skLineSegment(sketch, "E1674", {"start": v(-41.7, -21.75) * mm, "end": v(-41.94, -21.44) * mm});
            skLineSegment(sketch, "E1675", {"start": v(-41.94, -21.44) * mm, "end": v(-42.25, -21.2) * mm});
            skLineSegment(sketch, "E1676", {"start": v(-42.25, -21.2) * mm, "end": v(-42.61, -21.05) * mm});
            skLineSegment(sketch, "E1677", {"start": v(-42.61, -21.05) * mm, "end": v(-43, -21) * mm});
            skLineSegment(sketch, "E1678", {"start": v(-43, -21) * mm, "end": v(-43.39, -21.05) * mm});
            skLineSegment(sketch, "E1679", {"start": v(-43.39, -21.05) * mm, "end": v(-43.75, -21.2) * mm});
            skLineSegment(sketch, "E1680", {"start": v(-43.75, -21.2) * mm, "end": v(-44.06, -21.44) * mm});
            skLineSegment(sketch, "E1681", {"start": v(-44.06, -21.44) * mm, "end": v(-44.3, -21.75) * mm});
            skLineSegment(sketch, "E1682", {"start": v(-44.3, -21.75) * mm, "end": v(-44.45, -22.11) * mm});
            skLineSegment(sketch, "E1683", {"start": v(-44.45, -22.11) * mm, "end": v(-44.5, -22.5) * mm});
            skLineSegment(sketch, "E1684", {"start": v(-44.5, -22.5) * mm, "end": v(-44.45, -22.89) * mm});
            skLineSegment(sketch, "E1685", {"start": v(-44.45, -22.89) * mm, "end": v(-44.3, -23.25) * mm});
            skLineSegment(sketch, "E1686", {"start": v(-44.3, -23.25) * mm, "end": v(-44.06, -23.56) * mm});
            skLineSegment(sketch, "E1687", {"start": v(-44.06, -23.56) * mm, "end": v(-43.75, -23.8) * mm});
            skLineSegment(sketch, "E1688", {"start": v(-43.75, -23.8) * mm, "end": v(-43.39, -23.95) * mm});
            skLineSegment(sketch, "E1689", {"start": v(-43.39, -23.95) * mm, "end": v(-43, -24) * mm});
            skLineSegment(sketch, "E1690", {"start": v(-43, -24) * mm, "end": v(-42.61, -23.95) * mm});
            skLineSegment(sketch, "E1691", {"start": v(-32.59, -40.65) * mm, "end": v(-32.5, -40) * mm});
            skLineSegment(sketch, "E1692", {"start": v(-32.5, -40) * mm, "end": v(-32.5, 10) * mm});
            skLineSegment(sketch, "E1693", {"start": v(-32.5, 10) * mm, "end": v(-32.59, 10.65) * mm});
            skLineSegment(sketch, "E1694", {"start": v(-32.59, 10.65) * mm, "end": v(-32.83, 11.25) * mm});
            skLineSegment(sketch, "E1695", {"start": v(-32.83, 11.25) * mm, "end": v(-33.23, 11.77) * mm});
            skLineSegment(sketch, "E1696", {"start": v(-33.23, 11.77) * mm, "end": v(-33.75, 12.17) * mm});
            skLineSegment(sketch, "E1697", {"start": v(-33.75, 12.17) * mm, "end": v(-34.35, 12.41) * mm});
            skLineSegment(sketch, "E1698", {"start": v(-34.35, 12.41) * mm, "end": v(-35, 12.5) * mm});
            skLineSegment(sketch, "E1699", {"start": v(-35, 12.5) * mm, "end": v(-35.65, 12.41) * mm});
            skLineSegment(sketch, "E1700", {"start": v(-35.65, 12.41) * mm, "end": v(-36.25, 12.17) * mm});
            skLineSegment(sketch, "E1701", {"start": v(-36.25, 12.17) * mm, "end": v(-36.77, 11.77) * mm});
            skLineSegment(sketch, "E1702", {"start": v(-36.77, 11.77) * mm, "end": v(-37.17, 11.25) * mm});
            skLineSegment(sketch, "E1703", {"start": v(-37.17, 11.25) * mm, "end": v(-37.41, 10.65) * mm});
            skLineSegment(sketch, "E1704", {"start": v(-37.41, 10.65) * mm, "end": v(-37.5, 10) * mm});
            skLineSegment(sketch, "E1705", {"start": v(-37.5, 10) * mm, "end": v(-37.5, -40) * mm});
            skLineSegment(sketch, "E1706", {"start": v(-37.5, -40) * mm, "end": v(-37.41, -40.65) * mm});
            skLineSegment(sketch, "E1707", {"start": v(-37.41, -40.65) * mm, "end": v(-37.17, -41.25) * mm});
            skLineSegment(sketch, "E1708", {"start": v(-37.17, -41.25) * mm, "end": v(-36.77, -41.77) * mm});
            skLineSegment(sketch, "E1709", {"start": v(-36.77, -41.77) * mm, "end": v(-36.25, -42.17) * mm});
            skLineSegment(sketch, "E1710", {"start": v(-36.25, -42.17) * mm, "end": v(-35.65, -42.41) * mm});
            skLineSegment(sketch, "E1711", {"start": v(-35.65, -42.41) * mm, "end": v(-35, -42.5) * mm});
            skLineSegment(sketch, "E1712", {"start": v(-35, -42.5) * mm, "end": v(-34.35, -42.41) * mm});
            skLineSegment(sketch, "E1713", {"start": v(-34.35, -42.41) * mm, "end": v(-33.75, -42.17) * mm});
            skLineSegment(sketch, "E1714", {"start": v(-33.75, -42.17) * mm, "end": v(-33.23, -41.77) * mm});
            skLineSegment(sketch, "E1715", {"start": v(-33.23, -41.77) * mm, "end": v(-32.83, -41.25) * mm});
            skLineSegment(sketch, "E1716", {"start": v(-32.83, -41.25) * mm, "end": v(-32.59, -40.65) * mm});
            skLineSegment(sketch, "E1717", {"start": v(42.25, -3.8) * mm, "end": v(42.61, -3.95) * mm});
            skLineSegment(sketch, "E1718", {"start": v(42.61, -3.95) * mm, "end": v(43, -4) * mm});
            skLineSegment(sketch, "E1719", {"start": v(43, -4) * mm, "end": v(43.39, -3.95) * mm});
            skLineSegment(sketch, "E1720", {"start": v(43.39, -3.95) * mm, "end": v(43.75, -3.8) * mm});
            skLineSegment(sketch, "E1721", {"start": v(43.75, -3.8) * mm, "end": v(44.06, -3.56) * mm});
            skLineSegment(sketch, "E1722", {"start": v(44.06, -3.56) * mm, "end": v(44.3, -3.25) * mm});
            skLineSegment(sketch, "E1723", {"start": v(44.3, -3.25) * mm, "end": v(44.45, -2.89) * mm});
            skLineSegment(sketch, "E1724", {"start": v(44.45, -2.89) * mm, "end": v(44.5, -2.5) * mm});
            skLineSegment(sketch, "E1725", {"start": v(44.5, -2.5) * mm, "end": v(44.45, -2.11) * mm});
            skLineSegment(sketch, "E1726", {"start": v(44.45, -2.11) * mm, "end": v(44.3, -1.75) * mm});
            skLineSegment(sketch, "E1727", {"start": v(44.3, -1.75) * mm, "end": v(44.06, -1.44) * mm});
            skLineSegment(sketch, "E1728", {"start": v(44.06, -1.44) * mm, "end": v(43.75, -1.2) * mm});
            skLineSegment(sketch, "E1729", {"start": v(43.75, -1.2) * mm, "end": v(43.39, -1.05) * mm});
            skLineSegment(sketch, "E1730", {"start": v(43.39, -1.05) * mm, "end": v(43, -1) * mm});
            skLineSegment(sketch, "E1731", {"start": v(43, -1) * mm, "end": v(42.61, -1.05) * mm});
            skLineSegment(sketch, "E1732", {"start": v(42.61, -1.05) * mm, "end": v(42.25, -1.2) * mm});
            skLineSegment(sketch, "E1733", {"start": v(42.25, -1.2) * mm, "end": v(41.94, -1.44) * mm});
            skLineSegment(sketch, "E1734", {"start": v(41.94, -1.44) * mm, "end": v(41.7, -1.75) * mm});
            skLineSegment(sketch, "E1735", {"start": v(41.7, -1.75) * mm, "end": v(41.55, -2.11) * mm});
            skLineSegment(sketch, "E1736", {"start": v(41.55, -2.11) * mm, "end": v(41.5, -2.5) * mm});
            skLineSegment(sketch, "E1737", {"start": v(41.5, -2.5) * mm, "end": v(41.55, -2.89) * mm});
            skLineSegment(sketch, "E1738", {"start": v(41.55, -2.89) * mm, "end": v(41.7, -3.25) * mm});
            skLineSegment(sketch, "E1739", {"start": v(41.7, -3.25) * mm, "end": v(41.94, -3.56) * mm});
            skLineSegment(sketch, "E1740", {"start": v(41.94, -3.56) * mm, "end": v(42.25, -3.8) * mm});
            skLineSegment(sketch, "E1741", {"start": v(44.45, -12.89) * mm, "end": v(44.5, -12.5) * mm});
            skLineSegment(sketch, "E1742", {"start": v(44.5, -12.5) * mm, "end": v(44.45, -12.11) * mm});
            skLineSegment(sketch, "E1743", {"start": v(44.45, -12.11) * mm, "end": v(44.3, -11.75) * mm});
            skLineSegment(sketch, "E1744", {"start": v(44.3, -11.75) * mm, "end": v(44.06, -11.44) * mm});
            skLineSegment(sketch, "E1745", {"start": v(44.06, -11.44) * mm, "end": v(43.75, -11.2) * mm});
            skLineSegment(sketch, "E1746", {"start": v(43.75, -11.2) * mm, "end": v(43.39, -11.05) * mm});
            skLineSegment(sketch, "E1747", {"start": v(43.39, -11.05) * mm, "end": v(43, -11) * mm});
            skLineSegment(sketch, "E1748", {"start": v(43, -11) * mm, "end": v(42.61, -11.05) * mm});
            skLineSegment(sketch, "E1749", {"start": v(42.61, -11.05) * mm, "end": v(42.25, -11.2) * mm});
            skLineSegment(sketch, "E1750", {"start": v(42.25, -11.2) * mm, "end": v(41.94, -11.44) * mm});
            skLineSegment(sketch, "E1751", {"start": v(41.94, -11.44) * mm, "end": v(41.7, -11.75) * mm});
            skLineSegment(sketch, "E1752", {"start": v(41.7, -11.75) * mm, "end": v(41.55, -12.11) * mm});
            skLineSegment(sketch, "E1753", {"start": v(41.55, -12.11) * mm, "end": v(41.5, -12.5) * mm});
            skLineSegment(sketch, "E1754", {"start": v(41.5, -12.5) * mm, "end": v(41.55, -12.89) * mm});
            skLineSegment(sketch, "E1755", {"start": v(41.55, -12.89) * mm, "end": v(41.7, -13.25) * mm});
            skLineSegment(sketch, "E1756", {"start": v(41.7, -13.25) * mm, "end": v(41.94, -13.56) * mm});
            skLineSegment(sketch, "E1757", {"start": v(41.94, -13.56) * mm, "end": v(42.25, -13.8) * mm});
            skLineSegment(sketch, "E1758", {"start": v(42.25, -13.8) * mm, "end": v(42.61, -13.95) * mm});
            skLineSegment(sketch, "E1759", {"start": v(42.61, -13.95) * mm, "end": v(43, -14) * mm});
            skLineSegment(sketch, "E1760", {"start": v(43, -14) * mm, "end": v(43.39, -13.95) * mm});
            skLineSegment(sketch, "E1761", {"start": v(43.39, -13.95) * mm, "end": v(43.75, -13.8) * mm});
            skLineSegment(sketch, "E1762", {"start": v(43.75, -13.8) * mm, "end": v(44.06, -13.56) * mm});
            skLineSegment(sketch, "E1763", {"start": v(44.06, -13.56) * mm, "end": v(44.3, -13.25) * mm});
            skLineSegment(sketch, "E1764", {"start": v(44.3, -13.25) * mm, "end": v(44.45, -12.89) * mm});
            skLineSegment(sketch, "E1765", {"start": v(41.5, -22.5) * mm, "end": v(41.55, -22.89) * mm});
            skLineSegment(sketch, "E1766", {"start": v(41.55, -22.89) * mm, "end": v(41.7, -23.25) * mm});
            skLineSegment(sketch, "E1767", {"start": v(41.7, -23.25) * mm, "end": v(41.94, -23.56) * mm});
            skLineSegment(sketch, "E1768", {"start": v(41.94, -23.56) * mm, "end": v(42.25, -23.8) * mm});
            skLineSegment(sketch, "E1769", {"start": v(42.25, -23.8) * mm, "end": v(42.61, -23.95) * mm});
            skLineSegment(sketch, "E1770", {"start": v(42.61, -23.95) * mm, "end": v(43, -24) * mm});
            skLineSegment(sketch, "E1771", {"start": v(43, -24) * mm, "end": v(43.39, -23.95) * mm});
            skLineSegment(sketch, "E1772", {"start": v(43.39, -23.95) * mm, "end": v(43.75, -23.8) * mm});
            skLineSegment(sketch, "E1773", {"start": v(43.75, -23.8) * mm, "end": v(44.06, -23.56) * mm});
            skLineSegment(sketch, "E1774", {"start": v(44.06, -23.56) * mm, "end": v(44.3, -23.25) * mm});
            skLineSegment(sketch, "E1775", {"start": v(44.3, -23.25) * mm, "end": v(44.45, -22.89) * mm});
            skLineSegment(sketch, "E1776", {"start": v(44.45, -22.89) * mm, "end": v(44.5, -22.5) * mm});
            skLineSegment(sketch, "E1777", {"start": v(44.5, -22.5) * mm, "end": v(44.45, -22.11) * mm});
            skLineSegment(sketch, "E1778", {"start": v(44.45, -22.11) * mm, "end": v(44.3, -21.75) * mm});
            skLineSegment(sketch, "E1779", {"start": v(44.3, -21.75) * mm, "end": v(44.06, -21.44) * mm});
            skLineSegment(sketch, "E1780", {"start": v(44.06, -21.44) * mm, "end": v(43.75, -21.2) * mm});
            skLineSegment(sketch, "E1781", {"start": v(43.75, -21.2) * mm, "end": v(43.39, -21.05) * mm});
            skLineSegment(sketch, "E1782", {"start": v(43.39, -21.05) * mm, "end": v(43, -21) * mm});
            skLineSegment(sketch, "E1783", {"start": v(43, -21) * mm, "end": v(42.61, -21.05) * mm});
            skLineSegment(sketch, "E1784", {"start": v(42.61, -21.05) * mm, "end": v(42.25, -21.2) * mm});
            skLineSegment(sketch, "E1785", {"start": v(42.25, -21.2) * mm, "end": v(41.94, -21.44) * mm});
            skLineSegment(sketch, "E1786", {"start": v(41.94, -21.44) * mm, "end": v(41.7, -21.75) * mm});
            skLineSegment(sketch, "E1787", {"start": v(41.7, -21.75) * mm, "end": v(41.55, -22.11) * mm});
            skLineSegment(sketch, "E1788", {"start": v(41.55, -22.11) * mm, "end": v(41.5, -22.5) * mm});
            skLineSegment(sketch, "E1789", {"start": v(37.41, -40.65) * mm, "end": v(37.5, -40) * mm});
            skLineSegment(sketch, "E1790", {"start": v(37.5, -40) * mm, "end": v(37.5, 10) * mm});
            skLineSegment(sketch, "E1791", {"start": v(37.5, 10) * mm, "end": v(37.41, 10.65) * mm});
            skLineSegment(sketch, "E1792", {"start": v(37.41, 10.65) * mm, "end": v(37.17, 11.25) * mm});
            skLineSegment(sketch, "E1793", {"start": v(37.17, 11.25) * mm, "end": v(36.77, 11.77) * mm});
            skLineSegment(sketch, "E1794", {"start": v(36.77, 11.77) * mm, "end": v(36.25, 12.17) * mm});
            skLineSegment(sketch, "E1795", {"start": v(36.25, 12.17) * mm, "end": v(35.65, 12.41) * mm});
            skLineSegment(sketch, "E1796", {"start": v(35.65, 12.41) * mm, "end": v(35, 12.5) * mm});
            skLineSegment(sketch, "E1797", {"start": v(35, 12.5) * mm, "end": v(34.35, 12.41) * mm});
            skLineSegment(sketch, "E1798", {"start": v(34.35, 12.41) * mm, "end": v(33.75, 12.17) * mm});
            skLineSegment(sketch, "E1799", {"start": v(33.75, 12.17) * mm, "end": v(33.23, 11.77) * mm});
            skLineSegment(sketch, "E1800", {"start": v(33.23, 11.77) * mm, "end": v(32.83, 11.25) * mm});
            skLineSegment(sketch, "E1801", {"start": v(32.83, 11.25) * mm, "end": v(32.59, 10.65) * mm});
            skLineSegment(sketch, "E1802", {"start": v(32.59, 10.65) * mm, "end": v(32.5, 10) * mm});
            skLineSegment(sketch, "E1803", {"start": v(32.5, 10) * mm, "end": v(32.5, -40) * mm});
            skLineSegment(sketch, "E1804", {"start": v(32.5, -40) * mm, "end": v(32.59, -40.65) * mm});
            skLineSegment(sketch, "E1805", {"start": v(32.59, -40.65) * mm, "end": v(32.83, -41.25) * mm});
            skLineSegment(sketch, "E1806", {"start": v(32.83, -41.25) * mm, "end": v(33.23, -41.77) * mm});
            skLineSegment(sketch, "E1807", {"start": v(33.23, -41.77) * mm, "end": v(33.75, -42.17) * mm});
            skLineSegment(sketch, "E1808", {"start": v(33.75, -42.17) * mm, "end": v(34.35, -42.41) * mm});
            skLineSegment(sketch, "E1809", {"start": v(34.35, -42.41) * mm, "end": v(35, -42.5) * mm});
            skLineSegment(sketch, "E1810", {"start": v(35, -42.5) * mm, "end": v(35.65, -42.41) * mm});
            skLineSegment(sketch, "E1811", {"start": v(35.65, -42.41) * mm, "end": v(36.25, -42.17) * mm});
            skLineSegment(sketch, "E1812", {"start": v(36.25, -42.17) * mm, "end": v(36.77, -41.77) * mm});
            skLineSegment(sketch, "E1813", {"start": v(36.77, -41.77) * mm, "end": v(37.17, -41.25) * mm});
            skLineSegment(sketch, "E1814", {"start": v(37.17, -41.25) * mm, "end": v(37.41, -40.65) * mm});
            skSolve(sketch);
        }
        {
            var Q0;
            Q0=makeQuery(id+"F15.imprint","IMPRINT",FACE,{"disambiguationData":[TD([[makeQuery(id+"F15.imprint","IMPRINT",EDGE,{"derivedFrom":sQuery(id+"F15.wireOp",EDGE,"E1087")}),-1.0]])]});
            extrude(context, id + "F16", {"entities" : qUnion([Q0]), "depth" : 15 * mm});
        }
        {
            var Q0;
            Q0=makeQuery(id+"F12.opExtrude","SWEPT_FACE",FACE,{"disambiguationData":[OSD([sQuery(id+"F6.wireOp",EDGE,"E810")])]});
            cPlane(context, id + "F17", {"entities" : qUnion([Q0]), "cplaneType" : CPlaneType.OFFSET, "offset" : 25 * mm, "width" : 150 * mm, "height" : 150 * mm});
        }
        {
            var Q0;
            Q0=qCreatedBy(id+"F17.planeOp",FACE);
            var sketch = newSketch(context, id + "F18", { "sketchPlane" : qUnion([Q0])});
            skCircle(sketch, "E1815", {"center": v(-243.65, 0) * mm, "radius": 4 * mm});
            skSolve(sketch);
        }
        {
            var Q0;
            Q0=makeQuery(id+"F18.imprint","IMPRINT",FACE,{"disambiguationData":[TD([[makeQuery(id+"F18.imprint","IMPRINT",EDGE,{"derivedFrom":sQuery(id+"F18.wireOp",EDGE,"E1815")}),1.0]])]});
            extrude(context, id + "F19", {"entities" : qUnion([Q0]), "oppositeDirection" : true, "depth" : 180 * mm});
        }
        {
            var Q0;
            Q0=makeQuery(id+"F19.opExtrude","SWEPT_BODY",BODY,{"disambiguationData":[OSD([sQuery(id+"F18.wireOp",EDGE,"E1815")])]});
            var Q1;
            Q1=makeQuery(id+"F12.opExtrude","CAP_FACE",FACE,{"disambiguationData":[OSD([sQuery(id+"F6.wireOp",EDGE,"E808"),sQuery(id+"F6.wireOp",EDGE,"E809"),sQuery(id+"F6.wireOp",EDGE,"E810"),sQuery(id+"F6.wireOp",EDGE,"E811"),sQuery(id+"F6.wireOp",EDGE,"b6d452ef-2114-4582-968b-06bec4fd55a2"),sQuery(id+"F6.wireOp",EDGE,"71f92113-067b-4937-bfd3-1dd7759bd324"),sQuery(id+"F6.wireOp",EDGE,"8e46fb9e-0ac2-4c18-8b03-988571f8b433"),sQuery(id+"F6.wireOp",EDGE,"008bde56-0bde-43f1-b833-b36f68488381"),sQuery(id+"F6.wireOp",EDGE,"f193bb30-39d9-4188-a952-afafa195bcf1"),sQuery(id+"F6.wireOp",EDGE,"9ad18f80-c851-4079-8b69-a311aa0802b0"),sQuery(id+"F6.wireOp",EDGE,"ee7add19-35a5-49c3-9b2d-66962c6c40c3"),sQuery(id+"F6.wireOp",EDGE,"589c4452-4ef8-4241-9c76-7f8684238935"),sQuery(id+"F6.wireOp",EDGE,"893e2afe-ef83-4e89-b2ed-0f4f57f8dca9"),sQuery(id+"F6.wireOp",EDGE,"3b567ff1-7e48-4153-972e-3eadbefbb171"),sQuery(id+"F6.wireOp",EDGE,"8f94ad23-07c4-4eab-87cd-b2f9e25b2e08"),sQuery(id+"F6.wireOp",EDGE,"a8190b9f-77ea-4595-86aa-b05f21adaa9a"),sQuery(id+"F6.wireOp",EDGE,"56a1d239-4a58-471c-a68c-3ad1c6cba160"),sQuery(id+"F6.wireOp",EDGE,"8495c42c-9516-4941-8d6d-7d6d4307d621"),sQuery(id+"F6.wireOp",EDGE,"dd810acc-e2e6-456c-8933-b1adeaf35203"),sQuery(id+"F6.wireOp",EDGE,"937539ee-8d36-4842-9cd5-339eb6af1340"),sQuery(id+"F6.wireOp",EDGE,"8628945c-ed95-4c31-9e27-22402c2fa5d6"),sQuery(id+"F6.wireOp",EDGE,"3f9f5c61-67b0-4dcb-9805-551f5fa69953"),sQuery(id+"F6.wireOp",EDGE,"8e484488-b106-4039-93a9-32b0e181c9ed"),sQuery(id+"F6.wireOp",EDGE,"ea226030-895c-40bb-8f2d-9dd32b710f30"),sQuery(id+"F6.wireOp",EDGE,"7c8721bc-ce4d-47b8-acf7-121871e3b3a1"),sQuery(id+"F6.wireOp",EDGE,"7b72f06f-e20d-4b42-ae93-d0511621f1f0"),sQuery(id+"F6.wireOp",EDGE,"2691a2b0-5b23-4ddd-9858-c5e1d5566a47"),sQuery(id+"F6.wireOp",EDGE,"fb9d93f2-20ff-40f5-9591-4a86ce6865c7"),sQuery(id+"F6.wireOp",EDGE,"b19f10df-d761-45f0-a23f-615dab911baa"),sQuery(id+"F6.wireOp",EDGE,"93561c31-0ede-4b4f-b4c5-d2196e0de465"),sQuery(id+"F6.wireOp",EDGE,"2790dcad-9b34-438c-8ec2-fba85b40360c"),sQuery(id+"F6.wireOp",EDGE,"a660c751-3638-4c26-8e6e-2f568475b784"),sQuery(id+"F6.wireOp",EDGE,"4373e5ec-77ca-43f5-936e-8ec90f160f20"),sQuery(id+"F6.wireOp",EDGE,"2bf9c229-cadc-4bad-88fc-7a43b9bcefc9"),sQuery(id+"F6.wireOp",EDGE,"a48e34a3-4af2-4a4a-9049-177eac4b3a9c"),sQuery(id+"F6.wireOp",EDGE,"f2c2d45f-9003-4457-b20c-0319e65cd9ac"),sQuery(id+"F6.wireOp",EDGE,"c9f43377-357f-4bd5-8449-64b6f922163f"),sQuery(id+"F6.wireOp",EDGE,"0cfb88e8-429d-4f11-ba15-bd1677f57793"),sQuery(id+"F6.wireOp",EDGE,"e2e0bb18-4dac-4569-be00-5d3d05ec71fa"),sQuery(id+"F6.wireOp",EDGE,"6e2447fa-d2c8-4ca9-ad64-175c526eee5c"),sQuery(id+"F6.wireOp",EDGE,"f3cf6ae0-648e-474e-bb54-3a7c262d6ccb"),sQuery(id+"F6.wireOp",EDGE,"674f2343-78a9-4fae-8802-e36b229328a0"),sQuery(id+"F6.wireOp",EDGE,"61a7d188-ebb4-4ec3-a974-f297c1e26d51"),sQuery(id+"F6.wireOp",EDGE,"1ac7bb48-69b3-4427-b049-8c052b6e0036"),sQuery(id+"F6.wireOp",EDGE,"249f62f8-3842-44d2-b58f-f993784eb49f"),sQuery(id+"F6.wireOp",EDGE,"904c33c7-2660-4853-832b-ba413acce14d"),sQuery(id+"F6.wireOp",EDGE,"e992672b-a4dc-40f7-9735-4295361a8126"),sQuery(id+"F6.wireOp",EDGE,"789c781b-49e2-437c-a2bb-4175a3ec64ed"),sQuery(id+"F6.wireOp",EDGE,"7557bfc7-5f57-48d1-b90a-5fe73bd77af3"),sQuery(id+"F6.wireOp",EDGE,"d1d8ebe8-1383-4224-8181-87d13d4862f9"),sQuery(id+"F6.wireOp",EDGE,"cb63900b-c2e4-47e8-bdb8-3a2b21824665"),sQuery(id+"F6.wireOp",EDGE,"25865b8a-05e1-4742-a7f1-dc252499a678"),sQuery(id+"F6.wireOp",EDGE,"81dfb874-497d-4fbc-90e1-d75731f99f6f"),sQuery(id+"F6.wireOp",EDGE,"E812"),sQuery(id+"F6.wireOp",EDGE,"E813")])],"isStart":false});
            mirror(context, id + "F20", {"entities" : qUnion([Q0]), "mirrorPlane" : qUnion([Q1])});
        }
    });
